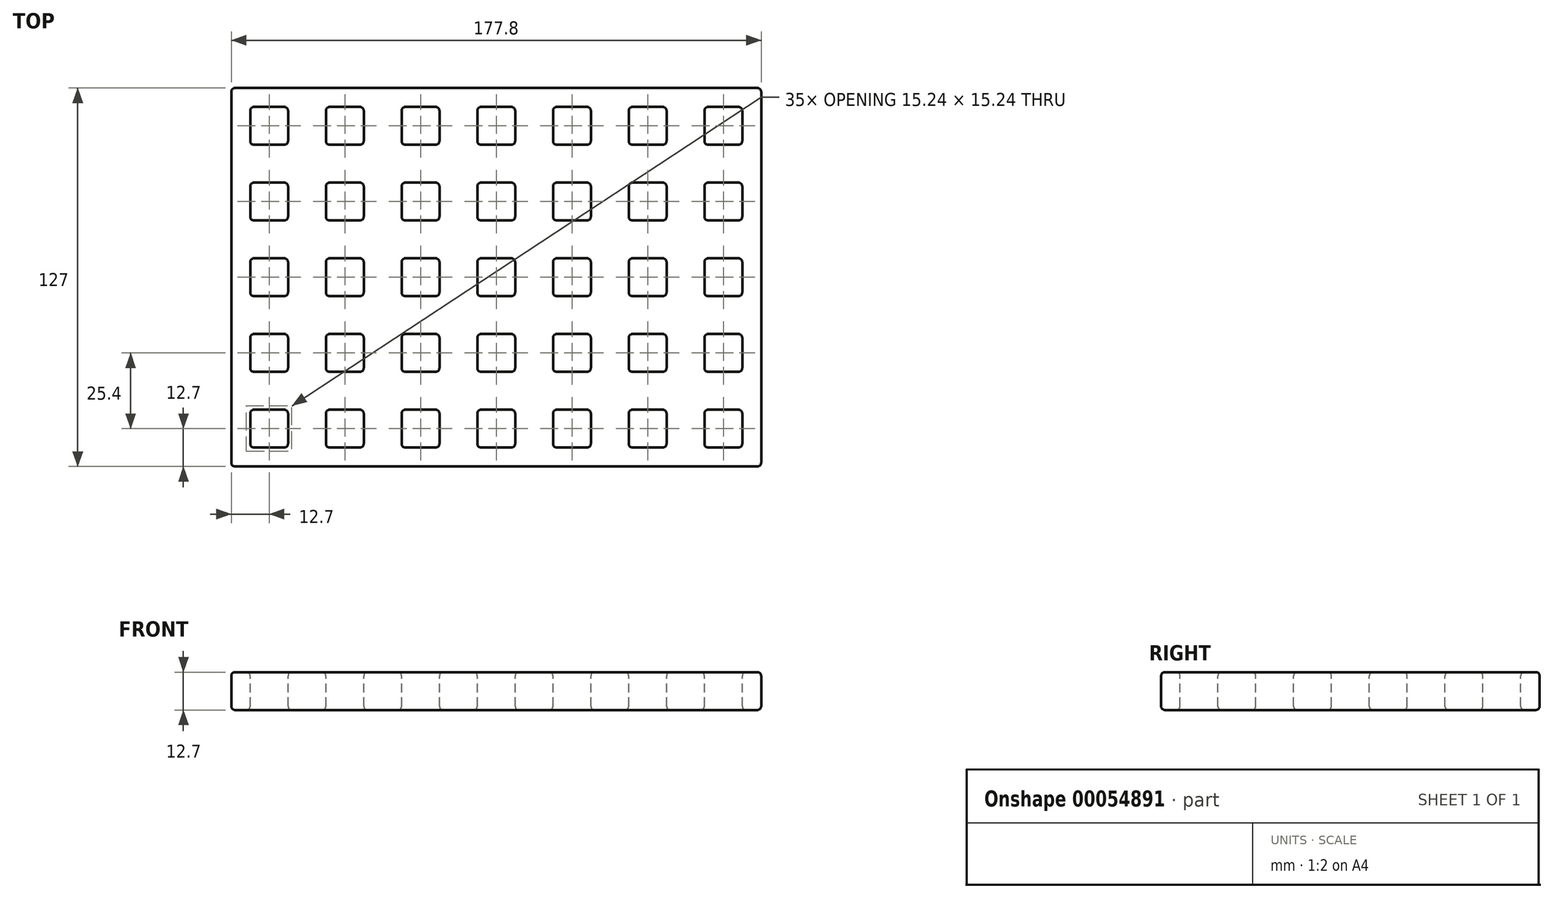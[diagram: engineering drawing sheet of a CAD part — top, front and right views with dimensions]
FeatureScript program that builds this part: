
annotation { "Feature Type Name" : "Feature", "Feature Type Description" : "" }
export const myFeature = defineFeature(function(context is Context, id is Id, definition is map)
    precondition{}
    {
        {
            var Q0;
            Q0=qCreatedBy(makeId("Top.planeOp"),FACE);
            var sketch = newSketch(context, id + "F0", { "sketchPlane" : qUnion([Q0])});
            skLineSegment(sketch, "E0.rect.bottom", {"start": v(88.9, 63.5) * mm, "end": v(-88.9, 63.5) * mm});
            skLineSegment(sketch, "E0.rect.top", {"start": v(88.9, -63.5) * mm, "end": v(-88.9, -63.5) * mm});
            skLineSegment(sketch, "E0.rect.left", {"start": v(88.9, 63.5) * mm, "end": v(88.9, -63.5) * mm});
            skLineSegment(sketch, "E0.rect.right", {"start": v(-88.9, 63.5) * mm, "end": v(-88.9, -63.5) * mm});
            skPoint(sketch, "E0.rect.middle", {"position": v(0, 0) * mm});
            skSolve(sketch);
        }
        {
            var Q0;
            Q0 = qSketchRegion(id + "F0", true);
            extrude(context, id + "F1", {"entities" : qUnion([Q0]), "depth" : 12.7 * mm});
        }
        {
            var Q0;
            Q0=makeQuery(id+"F1.opExtrude","CAP_FACE",FACE,{"disambiguationData":[OSD([sQuery(id+"F0.wireOp",EDGE,"E0.rect.bottom"),sQuery(id+"F0.wireOp",EDGE,"E0.rect.top"),sQuery(id+"F0.wireOp",EDGE,"E0.rect.left"),sQuery(id+"F0.wireOp",EDGE,"E0.rect.right")])],"isStart":false});
            var sketch = newSketch(context, id + "F2", { "sketchPlane" : qUnion([Q0])});
            skLineSegment(sketch, "E1.bottom", {"start": v(-82.55, 57.15) * mm, "end": v(-69.85, 57.15) * mm});
            skLineSegment(sketch, "E1.top", {"start": v(-82.55, 44.45) * mm, "end": v(-69.85, 44.45) * mm});
            skLineSegment(sketch, "E1.left", {"start": v(-82.55, 57.15) * mm, "end": v(-82.55, 44.45) * mm});
            skLineSegment(sketch, "E1.right", {"start": v(-69.85, 57.15) * mm, "end": v(-69.85, 44.45) * mm});
            skLineSegment(sketch, "E2.0.1.0", {"start": v(-82.55, 31.75) * mm, "end": v(-69.85, 31.75) * mm});
            skLineSegment(sketch, "E2.0.1.1", {"start": v(-82.55, 19.05) * mm, "end": v(-69.85, 19.05) * mm});
            skLineSegment(sketch, "E2.0.1.2", {"start": v(-82.55, 31.75) * mm, "end": v(-82.55, 19.05) * mm});
            skLineSegment(sketch, "E2.0.1.3", {"start": v(-69.85, 31.75) * mm, "end": v(-69.85, 19.05) * mm});
            skLineSegment(sketch, "E2.0.2.0", {"start": v(-82.55, 6.35) * mm, "end": v(-69.85, 6.35) * mm});
            skLineSegment(sketch, "E2.0.2.1", {"start": v(-82.55, -6.35) * mm, "end": v(-69.85, -6.35) * mm});
            skLineSegment(sketch, "E2.0.2.2", {"start": v(-82.55, 6.35) * mm, "end": v(-82.55, -6.35) * mm});
            skLineSegment(sketch, "E2.0.2.3", {"start": v(-69.85, 6.35) * mm, "end": v(-69.85, -6.35) * mm});
            skLineSegment(sketch, "E2.0.3.0", {"start": v(-82.55, -19.05) * mm, "end": v(-69.85, -19.05) * mm});
            skLineSegment(sketch, "E2.0.3.1", {"start": v(-82.55, -31.75) * mm, "end": v(-69.85, -31.75) * mm});
            skLineSegment(sketch, "E2.0.3.2", {"start": v(-82.55, -19.05) * mm, "end": v(-82.55, -31.75) * mm});
            skLineSegment(sketch, "E2.0.3.3", {"start": v(-69.85, -19.05) * mm, "end": v(-69.85, -31.75) * mm});
            skLineSegment(sketch, "E2.0.4.0", {"start": v(-82.55, -44.45) * mm, "end": v(-69.85, -44.45) * mm});
            skLineSegment(sketch, "E2.0.4.1", {"start": v(-82.55, -57.15) * mm, "end": v(-69.85, -57.15) * mm});
            skLineSegment(sketch, "E2.0.4.2", {"start": v(-82.55, -44.45) * mm, "end": v(-82.55, -57.15) * mm});
            skLineSegment(sketch, "E2.0.4.3", {"start": v(-69.85, -44.45) * mm, "end": v(-69.85, -57.15) * mm});
            skLineSegment(sketch, "E2.1.0.0", {"start": v(-57.15, 57.15) * mm, "end": v(-44.45, 57.15) * mm});
            skLineSegment(sketch, "E2.1.0.1", {"start": v(-57.15, 44.45) * mm, "end": v(-44.45, 44.45) * mm});
            skLineSegment(sketch, "E2.1.0.2", {"start": v(-57.15, 57.15) * mm, "end": v(-57.15, 44.45) * mm});
            skLineSegment(sketch, "E2.1.0.3", {"start": v(-44.45, 57.15) * mm, "end": v(-44.45, 44.45) * mm});
            skLineSegment(sketch, "E2.1.1.0", {"start": v(-57.15, 31.75) * mm, "end": v(-44.45, 31.75) * mm});
            skLineSegment(sketch, "E2.1.1.1", {"start": v(-57.15, 19.05) * mm, "end": v(-44.45, 19.05) * mm});
            skLineSegment(sketch, "E2.1.1.2", {"start": v(-57.15, 31.75) * mm, "end": v(-57.15, 19.05) * mm});
            skLineSegment(sketch, "E2.1.1.3", {"start": v(-44.45, 31.75) * mm, "end": v(-44.45, 19.05) * mm});
            skLineSegment(sketch, "E2.1.2.0", {"start": v(-57.15, 6.35) * mm, "end": v(-44.45, 6.35) * mm});
            skLineSegment(sketch, "E2.1.2.1", {"start": v(-57.15, -6.35) * mm, "end": v(-44.45, -6.35) * mm});
            skLineSegment(sketch, "E2.1.2.2", {"start": v(-57.15, 6.35) * mm, "end": v(-57.15, -6.35) * mm});
            skLineSegment(sketch, "E2.1.2.3", {"start": v(-44.45, 6.35) * mm, "end": v(-44.45, -6.35) * mm});
            skLineSegment(sketch, "E2.1.3.0", {"start": v(-57.15, -19.05) * mm, "end": v(-44.45, -19.05) * mm});
            skLineSegment(sketch, "E2.1.3.1", {"start": v(-57.15, -31.75) * mm, "end": v(-44.45, -31.75) * mm});
            skLineSegment(sketch, "E2.1.3.2", {"start": v(-57.15, -19.05) * mm, "end": v(-57.15, -31.75) * mm});
            skLineSegment(sketch, "E2.1.3.3", {"start": v(-44.45, -19.05) * mm, "end": v(-44.45, -31.75) * mm});
            skLineSegment(sketch, "E2.1.4.0", {"start": v(-57.15, -44.45) * mm, "end": v(-44.45, -44.45) * mm});
            skLineSegment(sketch, "E2.1.4.1", {"start": v(-57.15, -57.15) * mm, "end": v(-44.45, -57.15) * mm});
            skLineSegment(sketch, "E2.1.4.2", {"start": v(-57.15, -44.45) * mm, "end": v(-57.15, -57.15) * mm});
            skLineSegment(sketch, "E2.1.4.3", {"start": v(-44.45, -44.45) * mm, "end": v(-44.45, -57.15) * mm});
            skLineSegment(sketch, "E2.2.0.0", {"start": v(-31.75, 57.15) * mm, "end": v(-19.05, 57.15) * mm});
            skLineSegment(sketch, "E2.2.0.1", {"start": v(-31.75, 44.45) * mm, "end": v(-19.05, 44.45) * mm});
            skLineSegment(sketch, "E2.2.0.2", {"start": v(-31.75, 57.15) * mm, "end": v(-31.75, 44.45) * mm});
            skLineSegment(sketch, "E2.2.0.3", {"start": v(-19.05, 57.15) * mm, "end": v(-19.05, 44.45) * mm});
            skLineSegment(sketch, "E2.2.1.0", {"start": v(-31.75, 31.75) * mm, "end": v(-19.05, 31.75) * mm});
            skLineSegment(sketch, "E2.2.1.1", {"start": v(-31.75, 19.05) * mm, "end": v(-19.05, 19.05) * mm});
            skLineSegment(sketch, "E2.2.1.2", {"start": v(-31.75, 31.75) * mm, "end": v(-31.75, 19.05) * mm});
            skLineSegment(sketch, "E2.2.1.3", {"start": v(-19.05, 31.75) * mm, "end": v(-19.05, 19.05) * mm});
            skLineSegment(sketch, "E2.2.2.0", {"start": v(-31.75, 6.35) * mm, "end": v(-19.05, 6.35) * mm});
            skLineSegment(sketch, "E2.2.2.1", {"start": v(-31.75, -6.35) * mm, "end": v(-19.05, -6.35) * mm});
            skLineSegment(sketch, "E2.2.2.2", {"start": v(-31.75, 6.35) * mm, "end": v(-31.75, -6.35) * mm});
            skLineSegment(sketch, "E2.2.2.3", {"start": v(-19.05, 6.35) * mm, "end": v(-19.05, -6.35) * mm});
            skLineSegment(sketch, "E2.2.3.0", {"start": v(-31.75, -19.05) * mm, "end": v(-19.05, -19.05) * mm});
            skLineSegment(sketch, "E2.2.3.1", {"start": v(-31.75, -31.75) * mm, "end": v(-19.05, -31.75) * mm});
            skLineSegment(sketch, "E2.2.3.2", {"start": v(-31.75, -19.05) * mm, "end": v(-31.75, -31.75) * mm});
            skLineSegment(sketch, "E2.2.3.3", {"start": v(-19.05, -19.05) * mm, "end": v(-19.05, -31.75) * mm});
            skLineSegment(sketch, "E2.2.4.0", {"start": v(-31.75, -44.45) * mm, "end": v(-19.05, -44.45) * mm});
            skLineSegment(sketch, "E2.2.4.1", {"start": v(-31.75, -57.15) * mm, "end": v(-19.05, -57.15) * mm});
            skLineSegment(sketch, "E2.2.4.2", {"start": v(-31.75, -44.45) * mm, "end": v(-31.75, -57.15) * mm});
            skLineSegment(sketch, "E2.2.4.3", {"start": v(-19.05, -44.45) * mm, "end": v(-19.05, -57.15) * mm});
            skLineSegment(sketch, "E2.3.0.0", {"start": v(-6.35, 57.15) * mm, "end": v(6.35, 57.15) * mm});
            skLineSegment(sketch, "E2.3.0.1", {"start": v(-6.35, 44.45) * mm, "end": v(6.35, 44.45) * mm});
            skLineSegment(sketch, "E2.3.0.2", {"start": v(-6.35, 57.15) * mm, "end": v(-6.35, 44.45) * mm});
            skLineSegment(sketch, "E2.3.0.3", {"start": v(6.35, 57.15) * mm, "end": v(6.35, 44.45) * mm});
            skLineSegment(sketch, "E2.3.1.0", {"start": v(-6.35, 31.75) * mm, "end": v(6.35, 31.75) * mm});
            skLineSegment(sketch, "E2.3.1.1", {"start": v(-6.35, 19.05) * mm, "end": v(6.35, 19.05) * mm});
            skLineSegment(sketch, "E2.3.1.2", {"start": v(-6.35, 31.75) * mm, "end": v(-6.35, 19.05) * mm});
            skLineSegment(sketch, "E2.3.1.3", {"start": v(6.35, 31.75) * mm, "end": v(6.35, 19.05) * mm});
            skLineSegment(sketch, "E2.3.2.0", {"start": v(-6.35, 6.35) * mm, "end": v(6.35, 6.35) * mm});
            skLineSegment(sketch, "E2.3.2.1", {"start": v(-6.35, -6.35) * mm, "end": v(6.35, -6.35) * mm});
            skLineSegment(sketch, "E2.3.2.2", {"start": v(-6.35, 6.35) * mm, "end": v(-6.35, -6.35) * mm});
            skLineSegment(sketch, "E2.3.2.3", {"start": v(6.35, 6.35) * mm, "end": v(6.35, -6.35) * mm});
            skLineSegment(sketch, "E2.3.3.0", {"start": v(-6.35, -19.05) * mm, "end": v(6.35, -19.05) * mm});
            skLineSegment(sketch, "E2.3.3.1", {"start": v(-6.35, -31.75) * mm, "end": v(6.35, -31.75) * mm});
            skLineSegment(sketch, "E2.3.3.2", {"start": v(-6.35, -19.05) * mm, "end": v(-6.35, -31.75) * mm});
            skLineSegment(sketch, "E2.3.3.3", {"start": v(6.35, -19.05) * mm, "end": v(6.35, -31.75) * mm});
            skLineSegment(sketch, "E2.3.4.0", {"start": v(-6.35, -44.45) * mm, "end": v(6.35, -44.45) * mm});
            skLineSegment(sketch, "E2.3.4.1", {"start": v(-6.35, -57.15) * mm, "end": v(6.35, -57.15) * mm});
            skLineSegment(sketch, "E2.3.4.2", {"start": v(-6.35, -44.45) * mm, "end": v(-6.35, -57.15) * mm});
            skLineSegment(sketch, "E2.3.4.3", {"start": v(6.35, -44.45) * mm, "end": v(6.35, -57.15) * mm});
            skLineSegment(sketch, "E2.4.0.0", {"start": v(19.05, 57.15) * mm, "end": v(31.75, 57.15) * mm});
            skLineSegment(sketch, "E2.4.0.1", {"start": v(19.05, 44.45) * mm, "end": v(31.75, 44.45) * mm});
            skLineSegment(sketch, "E2.4.0.2", {"start": v(19.05, 57.15) * mm, "end": v(19.05, 44.45) * mm});
            skLineSegment(sketch, "E2.4.0.3", {"start": v(31.75, 57.15) * mm, "end": v(31.75, 44.45) * mm});
            skLineSegment(sketch, "E2.4.1.0", {"start": v(19.05, 31.75) * mm, "end": v(31.75, 31.75) * mm});
            skLineSegment(sketch, "E2.4.1.1", {"start": v(19.05, 19.05) * mm, "end": v(31.75, 19.05) * mm});
            skLineSegment(sketch, "E2.4.1.2", {"start": v(19.05, 31.75) * mm, "end": v(19.05, 19.05) * mm});
            skLineSegment(sketch, "E2.4.1.3", {"start": v(31.75, 31.75) * mm, "end": v(31.75, 19.05) * mm});
            skLineSegment(sketch, "E2.4.2.0", {"start": v(19.05, 6.35) * mm, "end": v(31.75, 6.35) * mm});
            skLineSegment(sketch, "E2.4.2.1", {"start": v(19.05, -6.35) * mm, "end": v(31.75, -6.35) * mm});
            skLineSegment(sketch, "E2.4.2.2", {"start": v(19.05, 6.35) * mm, "end": v(19.05, -6.35) * mm});
            skLineSegment(sketch, "E2.4.2.3", {"start": v(31.75, 6.35) * mm, "end": v(31.75, -6.35) * mm});
            skLineSegment(sketch, "E2.4.3.0", {"start": v(19.05, -19.05) * mm, "end": v(31.75, -19.05) * mm});
            skLineSegment(sketch, "E2.4.3.1", {"start": v(19.05, -31.75) * mm, "end": v(31.75, -31.75) * mm});
            skLineSegment(sketch, "E2.4.3.2", {"start": v(19.05, -19.05) * mm, "end": v(19.05, -31.75) * mm});
            skLineSegment(sketch, "E2.4.3.3", {"start": v(31.75, -19.05) * mm, "end": v(31.75, -31.75) * mm});
            skLineSegment(sketch, "E2.4.4.0", {"start": v(19.05, -44.45) * mm, "end": v(31.75, -44.45) * mm});
            skLineSegment(sketch, "E2.4.4.1", {"start": v(19.05, -57.15) * mm, "end": v(31.75, -57.15) * mm});
            skLineSegment(sketch, "E2.4.4.2", {"start": v(19.05, -44.45) * mm, "end": v(19.05, -57.15) * mm});
            skLineSegment(sketch, "E2.4.4.3", {"start": v(31.75, -44.45) * mm, "end": v(31.75, -57.15) * mm});
            skLineSegment(sketch, "E2.5.0.0", {"start": v(44.45, 57.15) * mm, "end": v(57.15, 57.15) * mm});
            skLineSegment(sketch, "E2.5.0.1", {"start": v(44.45, 44.45) * mm, "end": v(57.15, 44.45) * mm});
            skLineSegment(sketch, "E2.5.0.2", {"start": v(44.45, 57.15) * mm, "end": v(44.45, 44.45) * mm});
            skLineSegment(sketch, "E2.5.0.3", {"start": v(57.15, 57.15) * mm, "end": v(57.15, 44.45) * mm});
            skLineSegment(sketch, "E2.5.1.0", {"start": v(44.45, 31.75) * mm, "end": v(57.15, 31.75) * mm});
            skLineSegment(sketch, "E2.5.1.1", {"start": v(44.45, 19.05) * mm, "end": v(57.15, 19.05) * mm});
            skLineSegment(sketch, "E2.5.1.2", {"start": v(44.45, 31.75) * mm, "end": v(44.45, 19.05) * mm});
            skLineSegment(sketch, "E2.5.1.3", {"start": v(57.15, 31.75) * mm, "end": v(57.15, 19.05) * mm});
            skLineSegment(sketch, "E2.5.2.0", {"start": v(44.45, 6.35) * mm, "end": v(57.15, 6.35) * mm});
            skLineSegment(sketch, "E2.5.2.1", {"start": v(44.45, -6.35) * mm, "end": v(57.15, -6.35) * mm});
            skLineSegment(sketch, "E2.5.2.2", {"start": v(44.45, 6.35) * mm, "end": v(44.45, -6.35) * mm});
            skLineSegment(sketch, "E2.5.2.3", {"start": v(57.15, 6.35) * mm, "end": v(57.15, -6.35) * mm});
            skLineSegment(sketch, "E2.5.3.0", {"start": v(44.45, -19.05) * mm, "end": v(57.15, -19.05) * mm});
            skLineSegment(sketch, "E2.5.3.1", {"start": v(44.45, -31.75) * mm, "end": v(57.15, -31.75) * mm});
            skLineSegment(sketch, "E2.5.3.2", {"start": v(44.45, -19.05) * mm, "end": v(44.45, -31.75) * mm});
            skLineSegment(sketch, "E2.5.3.3", {"start": v(57.15, -19.05) * mm, "end": v(57.15, -31.75) * mm});
            skLineSegment(sketch, "E2.5.4.0", {"start": v(44.45, -44.45) * mm, "end": v(57.15, -44.45) * mm});
            skLineSegment(sketch, "E2.5.4.1", {"start": v(44.45, -57.15) * mm, "end": v(57.15, -57.15) * mm});
            skLineSegment(sketch, "E2.5.4.2", {"start": v(44.45, -44.45) * mm, "end": v(44.45, -57.15) * mm});
            skLineSegment(sketch, "E2.5.4.3", {"start": v(57.15, -44.45) * mm, "end": v(57.15, -57.15) * mm});
            skLineSegment(sketch, "E2.6.0.0", {"start": v(69.85, 57.15) * mm, "end": v(82.55, 57.15) * mm});
            skLineSegment(sketch, "E2.6.0.1", {"start": v(69.85, 44.45) * mm, "end": v(82.55, 44.45) * mm});
            skLineSegment(sketch, "E2.6.0.2", {"start": v(69.85, 57.15) * mm, "end": v(69.85, 44.45) * mm});
            skLineSegment(sketch, "E2.6.0.3", {"start": v(82.55, 57.15) * mm, "end": v(82.55, 44.45) * mm});
            skLineSegment(sketch, "E2.6.1.0", {"start": v(69.85, 31.75) * mm, "end": v(82.55, 31.75) * mm});
            skLineSegment(sketch, "E2.6.1.1", {"start": v(69.85, 19.05) * mm, "end": v(82.55, 19.05) * mm});
            skLineSegment(sketch, "E2.6.1.2", {"start": v(69.85, 31.75) * mm, "end": v(69.85, 19.05) * mm});
            skLineSegment(sketch, "E2.6.1.3", {"start": v(82.55, 31.75) * mm, "end": v(82.55, 19.05) * mm});
            skLineSegment(sketch, "E2.6.2.0", {"start": v(69.85, 6.35) * mm, "end": v(82.55, 6.35) * mm});
            skLineSegment(sketch, "E2.6.2.1", {"start": v(69.85, -6.35) * mm, "end": v(82.55, -6.35) * mm});
            skLineSegment(sketch, "E2.6.2.2", {"start": v(69.85, 6.35) * mm, "end": v(69.85, -6.35) * mm});
            skLineSegment(sketch, "E2.6.2.3", {"start": v(82.55, 6.35) * mm, "end": v(82.55, -6.35) * mm});
            skLineSegment(sketch, "E2.6.3.0", {"start": v(69.85, -19.05) * mm, "end": v(82.55, -19.05) * mm});
            skLineSegment(sketch, "E2.6.3.1", {"start": v(69.85, -31.75) * mm, "end": v(82.55, -31.75) * mm});
            skLineSegment(sketch, "E2.6.3.2", {"start": v(69.85, -19.05) * mm, "end": v(69.85, -31.75) * mm});
            skLineSegment(sketch, "E2.6.3.3", {"start": v(82.55, -19.05) * mm, "end": v(82.55, -31.75) * mm});
            skLineSegment(sketch, "E2.6.4.0", {"start": v(69.85, -44.45) * mm, "end": v(82.55, -44.45) * mm});
            skLineSegment(sketch, "E2.6.4.1", {"start": v(69.85, -57.15) * mm, "end": v(82.55, -57.15) * mm});
            skLineSegment(sketch, "E2.6.4.2", {"start": v(69.85, -44.45) * mm, "end": v(69.85, -57.15) * mm});
            skLineSegment(sketch, "E2.6.4.3", {"start": v(82.55, -44.45) * mm, "end": v(82.55, -57.15) * mm});
            skLineSegment(sketch, "E2.direction1", {"start": v(-82.55, 57.15) * mm, "end": v(-57.15, 57.15) * mm, "construction": true});
            skLineSegment(sketch, "E2.direction2", {"start": v(-82.55, 57.15) * mm, "end": v(-82.55, 31.75) * mm, "construction": true});
            skSolve(sketch);
        }
        {
            var Q0;
            Q0 = qSketchRegion(id + "F2", true);
            extrude(context, id + "F3", {"entities" : qUnion([Q0]), "operationType" : NewBodyOperationType.REMOVE, "oppositeDirection" : true, "depth" : 25.4 * mm});
        }
        {
            var Q0;
            Q0=makeQuery(id+"F3.boolean.opBoolean","COPY",EDGE,{"derivedFrom":makeQuery(id+"F3.opExtrude","CAP_EDGE",EDGE,{"disambiguationData":[OSD([sQuery(id+"F2.wireOp",EDGE,"E2.5.4.3")])],"isStart":true})});
            var Q1;
            Q1=makeQuery(id+"F3.boolean.opBoolean","COPY",EDGE,{"derivedFrom":makeQuery(id+"F3.opExtrude","CAP_EDGE",EDGE,{"disambiguationData":[OSD([sQuery(id+"F2.wireOp",EDGE,"E2.5.0.3")])],"isStart":true})});
            var Q2;
            Q2=makeQuery(id+"F3.boolean.opBoolean","COPY",FACE,{"derivedFrom":makeQuery(id+"F3.opExtrude","SWEPT_FACE",FACE,{"disambiguationData":[OSD([sQuery(id+"F2.wireOp",EDGE,"E2.5.3.2")])]})});
            var Q3;
            Q3=makeQuery(id+"F3.boolean.opBoolean","COPY",FACE,{"derivedFrom":makeQuery(id+"F3.opExtrude","SWEPT_FACE",FACE,{"disambiguationData":[OSD([sQuery(id+"F2.wireOp",EDGE,"E2.0.4.2")])]})});
            var Q4;
            Q4=makeQuery(id+"F3.boolean.opBoolean","COPY",FACE,{"derivedFrom":makeQuery(id+"F3.opExtrude","SWEPT_FACE",FACE,{"disambiguationData":[OSD([sQuery(id+"F2.wireOp",EDGE,"E2.6.4.0")])]})});
            var Q5;
            Q5=makeQuery(id+"F3.boolean.opBoolean","COPY",FACE,{"derivedFrom":makeQuery(id+"F3.opExtrude","SWEPT_FACE",FACE,{"disambiguationData":[OSD([sQuery(id+"F2.wireOp",EDGE,"E2.6.0.0")])]})});
            var Q6;
            Q6=makeQuery(id+"F3.boolean.opBoolean","COPY",FACE,{"derivedFrom":makeQuery(id+"F3.opExtrude","SWEPT_FACE",FACE,{"disambiguationData":[OSD([sQuery(id+"F2.wireOp",EDGE,"E2.3.3.0")])]})});
            var Q7;
            Q7=makeQuery(id+"F3.boolean.opBoolean","COPY",FACE,{"derivedFrom":makeQuery(id+"F3.opExtrude","SWEPT_FACE",FACE,{"disambiguationData":[OSD([sQuery(id+"F2.wireOp",EDGE,"E2.2.4.0")])]})});
            var Q8;
            Q8=makeQuery(id+"F3.boolean.opBoolean","COPY",EDGE,{"derivedFrom":makeQuery(id+"F3.opExtrude","CAP_EDGE",EDGE,{"disambiguationData":[OSD([sQuery(id+"F2.wireOp",EDGE,"E2.0.3.1")])],"isStart":true})});
            var Q9;
            Q9=makeQuery(id+"F3.boolean.opBoolean","COPY",EDGE,{"derivedFrom":makeQuery(id+"F3.opExtrude","CAP_EDGE",EDGE,{"disambiguationData":[OSD([sQuery(id+"F2.wireOp",EDGE,"E2.0.2.2")])],"isStart":true})});
            var Q10;
            Q10=makeQuery(id+"F3.boolean.opBoolean","COPY",EDGE,{"derivedFrom":makeQuery(id+"F3.opExtrude","CAP_EDGE",EDGE,{"disambiguationData":[OSD([sQuery(id+"F2.wireOp",EDGE,"E2.3.3.2")])],"isStart":true})});
            var Q11;
            Q11=makeQuery(id+"F3.boolean.opBoolean","COPY",EDGE,{"derivedFrom":makeQuery(id+"F3.opExtrude","CAP_EDGE",EDGE,{"disambiguationData":[OSD([sQuery(id+"F2.wireOp",EDGE,"E2.2.4.2")])],"isStart":true})});
            var Q12;
            Q12=makeQuery(id+"F3.boolean.opBoolean","COPY",EDGE,{"derivedFrom":makeQuery(id+"F3.opExtrude","CAP_EDGE",EDGE,{"disambiguationData":[OSD([sQuery(id+"F2.wireOp",EDGE,"E2.6.4.2")])],"isStart":true})});
            var Q13;
            Q13=makeQuery(id+"F3.boolean.opBoolean","COPY",EDGE,{"derivedFrom":makeQuery(id+"F3.opExtrude","CAP_EDGE",EDGE,{"disambiguationData":[OSD([sQuery(id+"F2.wireOp",EDGE,"E2.6.0.2")])],"isStart":true})});
            var Q14;
            Q14=makeQuery(id+"F3.boolean.opBoolean","COPY",FACE,{"derivedFrom":makeQuery(id+"F3.opExtrude","SWEPT_FACE",FACE,{"disambiguationData":[OSD([sQuery(id+"F2.wireOp",EDGE,"E2.1.4.2")])]})});
            var Q15;
            Q15=makeQuery(id+"F3.boolean.opBoolean","COPY",FACE,{"derivedFrom":makeQuery(id+"F3.opExtrude","SWEPT_FACE",FACE,{"disambiguationData":[OSD([sQuery(id+"F2.wireOp",EDGE,"E2.2.3.2")])]})});
            var Q16;
            Q16=makeQuery(id+"F3.boolean.opBoolean","COPY",FACE,{"derivedFrom":makeQuery(id+"F3.opExtrude","SWEPT_FACE",FACE,{"disambiguationData":[OSD([sQuery(id+"F2.wireOp",EDGE,"E2.6.3.2")])]})});
            var Q17;
            Q17=makeQuery(id+"F3.boolean.opBoolean","COPY",FACE,{"derivedFrom":makeQuery(id+"F3.opExtrude","SWEPT_FACE",FACE,{"disambiguationData":[OSD([sQuery(id+"F2.wireOp",EDGE,"E2.5.4.2")])]})});
            var Q18;
            Q18=makeQuery(id+"F3.boolean.opBoolean","COPY",EDGE,{"derivedFrom":makeQuery(id+"F3.opExtrude","CAP_EDGE",EDGE,{"disambiguationData":[OSD([sQuery(id+"F2.wireOp",EDGE,"E2.3.4.1")])],"isStart":true})});
            var Q19;
            Q19=makeQuery(id+"F3.boolean.opBoolean","COPY",EDGE,{"derivedFrom":makeQuery(id+"F3.opExtrude","CAP_EDGE",EDGE,{"disambiguationData":[OSD([sQuery(id+"F2.wireOp",EDGE,"E2.1.2.1")])],"isStart":true})});
            var Q20;
            Q20=makeQuery(id+"F3.boolean.opBoolean","COPY",EDGE,{"derivedFrom":makeQuery(id+"F3.opExtrude","CAP_EDGE",EDGE,{"disambiguationData":[OSD([sQuery(id+"F2.wireOp",EDGE,"E2.6.1.1")])],"isStart":true})});
            var Q21;
            Q21=makeQuery(id+"F3.boolean.opBoolean","COPY",EDGE,{"derivedFrom":makeQuery(id+"F3.opExtrude","CAP_EDGE",EDGE,{"disambiguationData":[OSD([sQuery(id+"F2.wireOp",EDGE,"E2.5.2.1")])],"isStart":true})});
            var Q22;
            Q22=makeQuery(id+"F3.boolean.opBoolean","COPY",FACE,{"derivedFrom":makeQuery(id+"F3.opExtrude","SWEPT_FACE",FACE,{"disambiguationData":[OSD([sQuery(id+"F2.wireOp",EDGE,"E2.2.4.1")])]})});
            var Q23;
            Q23=makeQuery(id+"F3.boolean.opBoolean","COPY",FACE,{"derivedFrom":makeQuery(id+"F3.opExtrude","SWEPT_FACE",FACE,{"disambiguationData":[OSD([sQuery(id+"F2.wireOp",EDGE,"E2.6.4.1")])]})});
            var Q24;
            Q24=makeQuery(id+"F3.boolean.opBoolean","COPY",FACE,{"derivedFrom":makeQuery(id+"F3.opExtrude","SWEPT_FACE",FACE,{"disambiguationData":[OSD([sQuery(id+"F2.wireOp",EDGE,"E2.6.0.1")])]})});
            var Q25;
            Q25=makeQuery(id+"F3.boolean.opBoolean","COPY",EDGE,{"derivedFrom":makeQuery(id+"F3.opExtrude","CAP_EDGE",EDGE,{"disambiguationData":[OSD([sQuery(id+"F2.wireOp",EDGE,"E2.0.3.2")])],"isStart":true})});
            var Q26;
            Q26=makeQuery(id+"F3.boolean.opBoolean","COPY",EDGE,{"derivedFrom":makeQuery(id+"F3.opExtrude","CAP_EDGE",EDGE,{"disambiguationData":[OSD([sQuery(id+"F2.wireOp",EDGE,"E2.3.4.2")])],"isStart":true})});
            var Q27;
            Q27=makeQuery(id+"F3.boolean.opBoolean","COPY",EDGE,{"derivedFrom":makeQuery(id+"F3.opExtrude","CAP_EDGE",EDGE,{"disambiguationData":[OSD([sQuery(id+"F2.wireOp",EDGE,"E2.6.1.2")])],"isStart":true})});
            var Q28;
            Q28=makeQuery(id+"F3.boolean.opBoolean","COPY",FACE,{"derivedFrom":makeQuery(id+"F3.opExtrude","SWEPT_FACE",FACE,{"disambiguationData":[OSD([sQuery(id+"F2.wireOp",EDGE,"E2.3.3.2")])]})});
            var Q29;
            Q29=makeQuery(id+"F3.boolean.opBoolean","COPY",FACE,{"derivedFrom":makeQuery(id+"F3.opExtrude","SWEPT_FACE",FACE,{"disambiguationData":[OSD([sQuery(id+"F2.wireOp",EDGE,"E2.2.4.2")])]})});
            var Q30;
            Q30=makeQuery(id+"F3.boolean.opBoolean","COPY",FACE,{"derivedFrom":makeQuery(id+"F3.opExtrude","SWEPT_FACE",FACE,{"disambiguationData":[OSD([sQuery(id+"F2.wireOp",EDGE,"E2.6.4.2")])]})});
            var Q31;
            Q31=makeQuery(id+"F3.boolean.opBoolean","COPY",FACE,{"derivedFrom":makeQuery(id+"F3.opExtrude","SWEPT_FACE",FACE,{"disambiguationData":[OSD([sQuery(id+"F2.wireOp",EDGE,"E2.6.0.2")])]})});
            var Q32;
            Q32=makeQuery(id+"F3.boolean.opBoolean","COPY",FACE,{"derivedFrom":makeQuery(id+"F3.opExtrude","SWEPT_FACE",FACE,{"disambiguationData":[OSD([sQuery(id+"F2.wireOp",EDGE,"E2.2.4.3")])]})});
            var Q33;
            Q33=makeQuery(id+"F3.boolean.opBoolean","COPY",FACE,{"derivedFrom":makeQuery(id+"F3.opExtrude","SWEPT_FACE",FACE,{"disambiguationData":[OSD([sQuery(id+"F2.wireOp",EDGE,"E2.6.0.3")])]})});
            var Q34;
            Q34=makeQuery(id+"F3.boolean.opBoolean","COPY",FACE,{"derivedFrom":makeQuery(id+"F3.opExtrude","SWEPT_FACE",FACE,{"disambiguationData":[OSD([sQuery(id+"F2.wireOp",EDGE,"E2.6.4.3")])]})});
            var Q35;
            Q35=makeQuery(id+"F3.boolean.opBoolean","COPY",EDGE,{"derivedFrom":makeQuery(id+"F3.opExtrude","CAP_EDGE",EDGE,{"disambiguationData":[OSD([sQuery(id+"F2.wireOp",EDGE,"E2.0.4.0")])],"isStart":true})});
            var Q36;
            Q36=makeQuery(id+"F3.boolean.opBoolean","COPY",EDGE,{"derivedFrom":makeQuery(id+"F3.opExtrude","CAP_EDGE",EDGE,{"disambiguationData":[OSD([sQuery(id+"F2.wireOp",EDGE,"E2.4.4.0")])],"isStart":true})});
            var Q37;
            Q37=makeQuery(id+"F3.boolean.opBoolean","COPY",FACE,{"derivedFrom":makeQuery(id+"F3.opExtrude","SWEPT_FACE",FACE,{"disambiguationData":[OSD([sQuery(id+"F2.wireOp",EDGE,"E2.4.3.0")])]})});
            var Q38;
            Q38=makeQuery(id+"F3.boolean.opBoolean","COPY",FACE,{"derivedFrom":makeQuery(id+"F3.opExtrude","SWEPT_FACE",FACE,{"disambiguationData":[OSD([sQuery(id+"F2.wireOp",EDGE,"E2.3.4.0")])]})});
            var Q39;
            Q39=makeQuery(id+"F1.opExtrude","CAP_FACE",FACE,{"disambiguationData":[OSD([sQuery(id+"F0.wireOp",EDGE,"E0.rect.bottom"),sQuery(id+"F0.wireOp",EDGE,"E0.rect.top"),sQuery(id+"F0.wireOp",EDGE,"E0.rect.left"),sQuery(id+"F0.wireOp",EDGE,"E0.rect.right")])],"isStart":true});
            var Q40;
            Q40=makeQuery(id+"F3.boolean.opBoolean","COPY",FACE,{"derivedFrom":makeQuery(id+"F3.opExtrude","SWEPT_FACE",FACE,{"disambiguationData":[OSD([sQuery(id+"F2.wireOp",EDGE,"E2.6.1.0")])]})});
            var Q41;
            Q41=makeQuery(id+"F3.boolean.opBoolean","COPY",FACE,{"derivedFrom":makeQuery(id+"F3.opExtrude","SWEPT_FACE",FACE,{"disambiguationData":[OSD([sQuery(id+"F2.wireOp",EDGE,"E2.3.4.3")])]})});
            var Q42;
            Q42=makeQuery(id+"F3.boolean.opBoolean","COPY",FACE,{"derivedFrom":makeQuery(id+"F3.opExtrude","SWEPT_FACE",FACE,{"disambiguationData":[OSD([sQuery(id+"F2.wireOp",EDGE,"E2.6.1.3")])]})});
            var Q43;
            Q43=makeQuery(id+"F3.boolean.opBoolean","COPY",FACE,{"derivedFrom":makeQuery(id+"F3.opExtrude","SWEPT_FACE",FACE,{"disambiguationData":[OSD([sQuery(id+"F2.wireOp",EDGE,"E2.4.3.3")])]})});
            var Q44;
            Q44=makeQuery(id+"F3.boolean.opBoolean","COPY",EDGE,{"derivedFrom":makeQuery(id+"F3.opExtrude","CAP_EDGE",EDGE,{"disambiguationData":[OSD([sQuery(id+"F2.wireOp",EDGE,"E2.6.2.1")])],"isStart":true})});
            var Q45;
            Q45=makeQuery(id+"F3.boolean.opBoolean","COPY",EDGE,{"derivedFrom":makeQuery(id+"F3.opExtrude","CAP_EDGE",EDGE,{"disambiguationData":[OSD([sQuery(id+"F2.wireOp",EDGE,"E2.5.3.1")])],"isStart":true})});
            var Q46;
            Q46=makeQuery(id+"F3.boolean.opBoolean","COPY",FACE,{"derivedFrom":makeQuery(id+"F3.opExtrude","SWEPT_FACE",FACE,{"disambiguationData":[OSD([sQuery(id+"F2.wireOp",EDGE,"E2.1.2.1")])]})});
            var Q47;
            Q47=makeQuery(id+"F3.boolean.opBoolean","COPY",FACE,{"derivedFrom":makeQuery(id+"F3.opExtrude","SWEPT_FACE",FACE,{"disambiguationData":[OSD([sQuery(id+"F2.wireOp",EDGE,"E2.6.1.1")])]})});
            var Q48;
            Q48=makeQuery(id+"F3.boolean.opBoolean","COPY",FACE,{"derivedFrom":makeQuery(id+"F3.opExtrude","SWEPT_FACE",FACE,{"disambiguationData":[OSD([sQuery(id+"F2.wireOp",EDGE,"E2.5.0.3")])]})});
            var Q49;
            Q49=makeQuery(id+"F1.opExtrude","CAP_FACE",FACE,{"disambiguationData":[OSD([sQuery(id+"F0.wireOp",EDGE,"E0.rect.bottom"),sQuery(id+"F0.wireOp",EDGE,"E0.rect.top"),sQuery(id+"F0.wireOp",EDGE,"E0.rect.left"),sQuery(id+"F0.wireOp",EDGE,"E0.rect.right")])],"isStart":false});
            var Q50;
            Q50=makeQuery(id+"F3.boolean.opBoolean","COPY",EDGE,{"derivedFrom":makeQuery(id+"F3.opExtrude","CAP_EDGE",EDGE,{"disambiguationData":[OSD([sQuery(id+"F2.wireOp",EDGE,"E2.1.3.1")])],"isStart":true})});
            var Q51;
            Q51=makeQuery(id+"F3.boolean.opBoolean","COPY",EDGE,{"derivedFrom":makeQuery(id+"F3.opExtrude","CAP_EDGE",EDGE,{"disambiguationData":[OSD([sQuery(id+"F2.wireOp",EDGE,"E2.0.4.1")])],"isStart":true})});
            var Q52;
            Q52=makeQuery(id+"F3.boolean.opBoolean","COPY",EDGE,{"derivedFrom":makeQuery(id+"F3.opExtrude","CAP_EDGE",EDGE,{"disambiguationData":[OSD([sQuery(id+"F2.wireOp",EDGE,"E2.4.4.1")])],"isStart":true})});
            var Q53;
            Q53=makeQuery(id+"F3.boolean.opBoolean","COPY",EDGE,{"derivedFrom":makeQuery(id+"F3.opExtrude","CAP_EDGE",EDGE,{"disambiguationData":[OSD([sQuery(id+"F2.wireOp",EDGE,"E2.2.2.1")])],"isStart":true})});
            var Q54;
            Q54=makeQuery(id+"F3.boolean.opBoolean","COPY",FACE,{"derivedFrom":makeQuery(id+"F3.opExtrude","SWEPT_FACE",FACE,{"disambiguationData":[OSD([sQuery(id+"F2.wireOp",EDGE,"E2.6.1.2")])]})});
            var Q55;
            Q55=makeQuery(id+"F3.boolean.opBoolean","COPY",FACE,{"derivedFrom":makeQuery(id+"F3.opExtrude","SWEPT_FACE",FACE,{"disambiguationData":[OSD([sQuery(id+"F2.wireOp",EDGE,"E2.2.3.3")])]})});
            var Q56;
            Q56=makeQuery(id+"F3.boolean.opBoolean","COPY",FACE,{"derivedFrom":makeQuery(id+"F3.opExtrude","SWEPT_FACE",FACE,{"disambiguationData":[OSD([sQuery(id+"F2.wireOp",EDGE,"E2.6.3.3")])]})});
            var Q57;
            Q57=makeQuery(id+"F3.boolean.opBoolean","COPY",FACE,{"derivedFrom":makeQuery(id+"F3.opExtrude","SWEPT_FACE",FACE,{"disambiguationData":[OSD([sQuery(id+"F2.wireOp",EDGE,"E2.5.4.3")])]})});
            var Q58;
            Q58=makeQuery(id+"F3.boolean.opBoolean","COPY",FACE,{"derivedFrom":makeQuery(id+"F3.opExtrude","SWEPT_FACE",FACE,{"disambiguationData":[OSD([sQuery(id+"F2.wireOp",EDGE,"E2.3.4.2")])]})});
            var Q59;
            Q59=makeQuery(id+"F3.boolean.opBoolean","COPY",EDGE,{"derivedFrom":makeQuery(id+"F3.opExtrude","CAP_EDGE",EDGE,{"disambiguationData":[OSD([sQuery(id+"F2.wireOp",EDGE,"E2.2.4.3")])],"isStart":true})});
            var Q60;
            Q60=makeQuery(id+"F3.boolean.opBoolean","COPY",EDGE,{"derivedFrom":makeQuery(id+"F3.opExtrude","CAP_EDGE",EDGE,{"disambiguationData":[OSD([sQuery(id+"F2.wireOp",EDGE,"E2.1.3.2")])],"isStart":true})});
            var Q61;
            Q61=makeQuery(id+"F3.boolean.opBoolean","COPY",EDGE,{"derivedFrom":makeQuery(id+"F3.opExtrude","CAP_EDGE",EDGE,{"disambiguationData":[OSD([sQuery(id+"F2.wireOp",EDGE,"E2.0.4.2")])],"isStart":true})});
            var Q62;
            Q62=makeQuery(id+"F3.boolean.opBoolean","COPY",EDGE,{"derivedFrom":makeQuery(id+"F3.opExtrude","CAP_EDGE",EDGE,{"disambiguationData":[OSD([sQuery(id+"F2.wireOp",EDGE,"E2.4.4.2")])],"isStart":true})});
            var Q63;
            Q63=makeQuery(id+"F3.boolean.opBoolean","COPY",EDGE,{"derivedFrom":makeQuery(id+"F3.opExtrude","CAP_EDGE",EDGE,{"disambiguationData":[OSD([sQuery(id+"F2.wireOp",EDGE,"E2.5.3.2")])],"isStart":true})});
            var Q64;
            Q64=makeQuery(id+"F3.boolean.opBoolean","COPY",FACE,{"derivedFrom":makeQuery(id+"F3.opExtrude","SWEPT_FACE",FACE,{"disambiguationData":[OSD([sQuery(id+"F2.wireOp",EDGE,"E2.1.4.3")])]})});
            var Q65;
            Q65=makeQuery(id+"F3.boolean.opBoolean","COPY",EDGE,{"derivedFrom":makeQuery(id+"F3.opExtrude","CAP_EDGE",EDGE,{"disambiguationData":[OSD([sQuery(id+"F2.wireOp",EDGE,"E2.5.3.3")])],"isStart":true})});
            var Q66;
            Q66=makeQuery(id+"F3.boolean.opBoolean","COPY",FACE,{"derivedFrom":makeQuery(id+"F3.opExtrude","SWEPT_FACE",FACE,{"disambiguationData":[OSD([sQuery(id+"F2.wireOp",EDGE,"E2.1.3.0")])]})});
            var Q67;
            Q67=makeQuery(id+"F3.boolean.opBoolean","COPY",FACE,{"derivedFrom":makeQuery(id+"F3.opExtrude","SWEPT_FACE",FACE,{"disambiguationData":[OSD([sQuery(id+"F2.wireOp",EDGE,"E2.0.4.0")])]})});
            var Q68;
            Q68=makeQuery(id+"F3.boolean.opBoolean","COPY",FACE,{"derivedFrom":makeQuery(id+"F3.opExtrude","SWEPT_FACE",FACE,{"disambiguationData":[OSD([sQuery(id+"F2.wireOp",EDGE,"E2.6.2.0")])]})});
            var Q69;
            Q69=makeQuery(id+"F3.boolean.opBoolean","COPY",FACE,{"derivedFrom":makeQuery(id+"F3.opExtrude","SWEPT_FACE",FACE,{"disambiguationData":[OSD([sQuery(id+"F2.wireOp",EDGE,"E2.4.4.0")])]})});
            var Q70;
            Q70=makeQuery(id+"F3.boolean.opBoolean","COPY",FACE,{"derivedFrom":makeQuery(id+"F3.opExtrude","SWEPT_FACE",FACE,{"disambiguationData":[OSD([sQuery(id+"F2.wireOp",EDGE,"E2.5.3.0")])]})});
            var Q71;
            Q71=makeQuery(id+"F3.boolean.opBoolean","COPY",EDGE,{"derivedFrom":makeQuery(id+"F3.opExtrude","CAP_EDGE",EDGE,{"disambiguationData":[OSD([sQuery(id+"F2.wireOp",EDGE,"E2.1.4.1")])],"isStart":true})});
            var Q72;
            Q72=makeQuery(id+"F3.boolean.opBoolean","COPY",EDGE,{"derivedFrom":makeQuery(id+"F3.opExtrude","CAP_EDGE",EDGE,{"disambiguationData":[OSD([sQuery(id+"F2.wireOp",EDGE,"E2.3.2.1")])],"isStart":true})});
            var Q73;
            Q73=makeQuery(id+"F3.boolean.opBoolean","COPY",EDGE,{"derivedFrom":makeQuery(id+"F3.opExtrude","CAP_EDGE",EDGE,{"disambiguationData":[OSD([sQuery(id+"F2.wireOp",EDGE,"E2.2.3.1")])],"isStart":true})});
            var Q74;
            Q74=makeQuery(id+"F3.boolean.opBoolean","COPY",EDGE,{"derivedFrom":makeQuery(id+"F3.opExtrude","CAP_EDGE",EDGE,{"disambiguationData":[OSD([sQuery(id+"F2.wireOp",EDGE,"E2.6.3.1")])],"isStart":true})});
            var Q75;
            Q75=makeQuery(id+"F3.boolean.opBoolean","COPY",EDGE,{"derivedFrom":makeQuery(id+"F3.opExtrude","CAP_EDGE",EDGE,{"disambiguationData":[OSD([sQuery(id+"F2.wireOp",EDGE,"E2.5.4.1")])],"isStart":true})});
            var Q76;
            Q76=makeQuery(id+"F3.boolean.opBoolean","COPY",FACE,{"derivedFrom":makeQuery(id+"F3.opExtrude","SWEPT_FACE",FACE,{"disambiguationData":[OSD([sQuery(id+"F2.wireOp",EDGE,"E2.2.2.1")])]})});
            var Q77;
            Q77=makeQuery(id+"F3.boolean.opBoolean","COPY",FACE,{"derivedFrom":makeQuery(id+"F3.opExtrude","SWEPT_FACE",FACE,{"disambiguationData":[OSD([sQuery(id+"F2.wireOp",EDGE,"E2.1.3.1")])]})});
            var Q78;
            Q78=makeQuery(id+"F3.boolean.opBoolean","COPY",FACE,{"derivedFrom":makeQuery(id+"F3.opExtrude","SWEPT_FACE",FACE,{"disambiguationData":[OSD([sQuery(id+"F2.wireOp",EDGE,"E2.6.2.1")])]})});
            var Q79;
            Q79=makeQuery(id+"F3.boolean.opBoolean","COPY",EDGE,{"derivedFrom":makeQuery(id+"F3.opExtrude","CAP_EDGE",EDGE,{"disambiguationData":[OSD([sQuery(id+"F2.wireOp",EDGE,"E2.1.4.2")])],"isStart":true})});
            var Q80;
            Q80=makeQuery(id+"F3.boolean.opBoolean","COPY",EDGE,{"derivedFrom":makeQuery(id+"F3.opExtrude","CAP_EDGE",EDGE,{"disambiguationData":[OSD([sQuery(id+"F2.wireOp",EDGE,"E2.2.3.2")])],"isStart":true})});
            var Q81;
            Q81=makeQuery(id+"F3.boolean.opBoolean","COPY",EDGE,{"derivedFrom":makeQuery(id+"F3.opExtrude","CAP_EDGE",EDGE,{"disambiguationData":[OSD([sQuery(id+"F2.wireOp",EDGE,"E2.6.3.2")])],"isStart":true})});
            var Q82;
            Q82=makeQuery(id+"F3.boolean.opBoolean","COPY",EDGE,{"derivedFrom":makeQuery(id+"F3.opExtrude","CAP_EDGE",EDGE,{"disambiguationData":[OSD([sQuery(id+"F2.wireOp",EDGE,"E2.5.4.2")])],"isStart":true})});
            var Q83;
            Q83=makeQuery(id+"F3.boolean.opBoolean","COPY",FACE,{"derivedFrom":makeQuery(id+"F3.opExtrude","SWEPT_FACE",FACE,{"disambiguationData":[OSD([sQuery(id+"F2.wireOp",EDGE,"E2.1.3.2")])]})});
            var Q84;
            Q84=makeQuery(id+"F3.boolean.opBoolean","COPY",FACE,{"derivedFrom":makeQuery(id+"F3.opExtrude","SWEPT_FACE",FACE,{"disambiguationData":[OSD([sQuery(id+"F2.wireOp",EDGE,"E2.4.4.2")])]})});
            var Q85;
            Q85=makeQuery(id+"F3.boolean.opBoolean","COPY",EDGE,{"derivedFrom":makeQuery(id+"F3.opExtrude","CAP_EDGE",EDGE,{"disambiguationData":[OSD([sQuery(id+"F2.wireOp",EDGE,"E2.2.3.3")])],"isStart":true})});
            var Q86;
            Q86=makeQuery(id+"F1.opExtrude","SWEPT_FACE",FACE,{"disambiguationData":[OSD([sQuery(id+"F0.wireOp",EDGE,"E0.rect.bottom")])]});
            var Q87;
            Q87=makeQuery(id+"F1.opExtrude","SWEPT_FACE",FACE,{"disambiguationData":[OSD([sQuery(id+"F0.wireOp",EDGE,"E0.rect.top")])]});
            var Q88;
            Q88=makeQuery(id+"F1.opExtrude","SWEPT_FACE",FACE,{"disambiguationData":[OSD([sQuery(id+"F0.wireOp",EDGE,"E0.rect.left")])]});
            var Q89;
            Q89=makeQuery(id+"F3.boolean.opBoolean","COPY",FACE,{"derivedFrom":makeQuery(id+"F3.opExtrude","SWEPT_FACE",FACE,{"disambiguationData":[OSD([sQuery(id+"F2.wireOp",EDGE,"E2.2.2.3")])]})});
            var Q90;
            Q90=makeQuery(id+"F3.boolean.opBoolean","COPY",FACE,{"derivedFrom":makeQuery(id+"F3.opExtrude","SWEPT_FACE",FACE,{"disambiguationData":[OSD([sQuery(id+"F2.wireOp",EDGE,"E2.1.3.3")])]})});
            var Q91;
            Q91=makeQuery(id+"F3.boolean.opBoolean","COPY",FACE,{"derivedFrom":makeQuery(id+"F3.opExtrude","SWEPT_FACE",FACE,{"disambiguationData":[OSD([sQuery(id+"F2.wireOp",EDGE,"E2.0.4.3")])]})});
            var Q92;
            Q92=makeQuery(id+"F3.boolean.opBoolean","COPY",FACE,{"derivedFrom":makeQuery(id+"F3.opExtrude","SWEPT_FACE",FACE,{"disambiguationData":[OSD([sQuery(id+"F2.wireOp",EDGE,"E2.6.2.3")])]})});
            var Q93;
            Q93=makeQuery(id+"F3.boolean.opBoolean","COPY",FACE,{"derivedFrom":makeQuery(id+"F3.opExtrude","SWEPT_FACE",FACE,{"disambiguationData":[OSD([sQuery(id+"F2.wireOp",EDGE,"E2.5.3.3")])]})});
            var Q94;
            Q94=makeQuery(id+"F1.opExtrude","CAP_EDGE",EDGE,{"disambiguationData":[OSD([sQuery(id+"F0.wireOp",EDGE,"E0.rect.bottom")])],"isStart":false});
            var Q95;
            Q95=makeQuery(id+"F3.boolean.opBoolean","COPY",FACE,{"derivedFrom":makeQuery(id+"F3.opExtrude","SWEPT_FACE",FACE,{"disambiguationData":[OSD([sQuery(id+"F2.wireOp",EDGE,"E2.4.4.3")])]})});
            var Q96;
            Q96=makeQuery(id+"F1.opExtrude","CAP_EDGE",EDGE,{"disambiguationData":[OSD([sQuery(id+"F0.wireOp",EDGE,"E0.rect.top")])],"isStart":true});
            var Q97;
            Q97=makeQuery(id+"F1.opExtrude","CAP_EDGE",EDGE,{"disambiguationData":[OSD([sQuery(id+"F0.wireOp",EDGE,"E0.rect.top")])],"isStart":false});
            var Q98;
            Q98=makeQuery(id+"F1.opExtrude","CAP_EDGE",EDGE,{"disambiguationData":[OSD([sQuery(id+"F0.wireOp",EDGE,"E0.rect.left")])],"isStart":true});
            var Q99;
            Q99=makeQuery(id+"F1.opExtrude","CAP_EDGE",EDGE,{"disambiguationData":[OSD([sQuery(id+"F0.wireOp",EDGE,"E0.rect.left")])],"isStart":false});
            var Q100;
            Q100=makeQuery(id+"F1.opExtrude","CAP_EDGE",EDGE,{"disambiguationData":[OSD([sQuery(id+"F0.wireOp",EDGE,"E0.rect.right")])],"isStart":false});
            var Q101;
            Q101=makeQuery(id+"F3.boolean.opBoolean","COPY",FACE,{"derivedFrom":makeQuery(id+"F3.opExtrude","SWEPT_FACE",FACE,{"disambiguationData":[OSD([sQuery(id+"F2.wireOp",EDGE,"E2.0.3.3")])]})});
            var Q102;
            Q102=makeQuery(id+"F3.boolean.opBoolean","COPY",FACE,{"derivedFrom":makeQuery(id+"F3.opExtrude","SWEPT_FACE",FACE,{"disambiguationData":[OSD([sQuery(id+"F2.wireOp",EDGE,"E2.0.3.1")])]})});
            var Q103;
            Q103=makeQuery(id+"F3.boolean.opBoolean","COPY",FACE,{"derivedFrom":makeQuery(id+"F3.opExtrude","SWEPT_FACE",FACE,{"disambiguationData":[OSD([sQuery(id+"F2.wireOp",EDGE,"E2.0.3.2")])]})});
            var Q104;
            Q104=makeQuery(id+"F3.boolean.opBoolean","COPY",FACE,{"derivedFrom":makeQuery(id+"F3.opExtrude","SWEPT_FACE",FACE,{"disambiguationData":[OSD([sQuery(id+"F2.wireOp",EDGE,"E2.2.3.0")])]})});
            var Q105;
            Q105=makeQuery(id+"F3.boolean.opBoolean","COPY",FACE,{"derivedFrom":makeQuery(id+"F3.opExtrude","SWEPT_FACE",FACE,{"disambiguationData":[OSD([sQuery(id+"F2.wireOp",EDGE,"E2.1.4.0")])]})});
            var Q106;
            Q106=makeQuery(id+"F3.boolean.opBoolean","COPY",FACE,{"derivedFrom":makeQuery(id+"F3.opExtrude","SWEPT_FACE",FACE,{"disambiguationData":[OSD([sQuery(id+"F2.wireOp",EDGE,"E2.6.3.0")])]})});
            var Q107;
            Q107=makeQuery(id+"F3.boolean.opBoolean","COPY",FACE,{"derivedFrom":makeQuery(id+"F3.opExtrude","SWEPT_FACE",FACE,{"disambiguationData":[OSD([sQuery(id+"F2.wireOp",EDGE,"E2.5.4.0")])]})});
            var Q108;
            Q108=makeQuery(id+"F3.boolean.opBoolean","COPY",FACE,{"derivedFrom":makeQuery(id+"F3.opExtrude","SWEPT_FACE",FACE,{"disambiguationData":[OSD([sQuery(id+"F2.wireOp",EDGE,"E2.5.0.0")])]})});
            var Q109;
            Q109=makeQuery(id+"F3.boolean.opBoolean","COPY",FACE,{"derivedFrom":makeQuery(id+"F3.opExtrude","SWEPT_FACE",FACE,{"disambiguationData":[OSD([sQuery(id+"F2.wireOp",EDGE,"E2.0.2.1")])]})});
            var Q110;
            Q110=makeQuery(id+"F3.boolean.opBoolean","COPY",FACE,{"derivedFrom":makeQuery(id+"F3.opExtrude","SWEPT_FACE",FACE,{"disambiguationData":[OSD([sQuery(id+"F2.wireOp",EDGE,"E2.0.2.2")])]})});
            var Q111;
            Q111=makeQuery(id+"F3.boolean.opBoolean","COPY",FACE,{"derivedFrom":makeQuery(id+"F3.opExtrude","SWEPT_FACE",FACE,{"disambiguationData":[OSD([sQuery(id+"F2.wireOp",EDGE,"E2.0.3.0")])]})});
            var Q112;
            Q112=makeQuery(id+"F3.boolean.opBoolean","COPY",FACE,{"derivedFrom":makeQuery(id+"F3.opExtrude","SWEPT_FACE",FACE,{"disambiguationData":[OSD([sQuery(id+"F2.wireOp",EDGE,"E2.6.3.1")])]})});
            var Q113;
            Q113=makeQuery(id+"F3.boolean.opBoolean","COPY",FACE,{"derivedFrom":makeQuery(id+"F3.opExtrude","SWEPT_FACE",FACE,{"disambiguationData":[OSD([sQuery(id+"F2.wireOp",EDGE,"E2.5.0.1")])]})});
            var Q114;
            Q114=makeQuery(id+"F3.boolean.opBoolean","COPY",EDGE,{"derivedFrom":makeQuery(id+"F3.opExtrude","CAP_EDGE",EDGE,{"disambiguationData":[OSD([sQuery(id+"F2.wireOp",EDGE,"E2.0.2.1")])],"isStart":true})});
            var Q115;
            Q115=makeQuery(id+"F3.boolean.opBoolean","COPY",EDGE,{"derivedFrom":makeQuery(id+"F3.opExtrude","CAP_EDGE",EDGE,{"disambiguationData":[OSD([sQuery(id+"F2.wireOp",EDGE,"E2.4.2.1")])],"isStart":true})});
            var Q116;
            Q116=makeQuery(id+"F3.boolean.opBoolean","COPY",EDGE,{"derivedFrom":makeQuery(id+"F3.opExtrude","CAP_EDGE",EDGE,{"disambiguationData":[OSD([sQuery(id+"F2.wireOp",EDGE,"E2.3.3.1")])],"isStart":true})});
            var Q117;
            Q117=makeQuery(id+"F3.boolean.opBoolean","COPY",EDGE,{"derivedFrom":makeQuery(id+"F3.opExtrude","CAP_EDGE",EDGE,{"disambiguationData":[OSD([sQuery(id+"F2.wireOp",EDGE,"E2.2.4.1")])],"isStart":true})});
            var Q118;
            Q118=makeQuery(id+"F3.boolean.opBoolean","COPY",EDGE,{"derivedFrom":makeQuery(id+"F3.opExtrude","CAP_EDGE",EDGE,{"disambiguationData":[OSD([sQuery(id+"F2.wireOp",EDGE,"E2.6.4.1")])],"isStart":true})});
            var Q119;
            Q119=makeQuery(id+"F3.boolean.opBoolean","COPY",EDGE,{"derivedFrom":makeQuery(id+"F3.opExtrude","CAP_EDGE",EDGE,{"disambiguationData":[OSD([sQuery(id+"F2.wireOp",EDGE,"E2.6.0.1")])],"isStart":true})});
            var Q120;
            Q120=makeQuery(id+"F3.boolean.opBoolean","COPY",EDGE,{"derivedFrom":makeQuery(id+"F3.opExtrude","CAP_EDGE",EDGE,{"disambiguationData":[OSD([sQuery(id+"F2.wireOp",EDGE,"E2.6.3.3")])],"isStart":true})});
            var Q121;
            Q121=makeQuery(id+"F3.boolean.opBoolean","COPY",FACE,{"derivedFrom":makeQuery(id+"F3.opExtrude","SWEPT_FACE",FACE,{"disambiguationData":[OSD([sQuery(id+"F2.wireOp",EDGE,"E2.6.2.2")])]})});
            var Q122;
            Q122=makeQuery(id+"F3.boolean.opBoolean","INTERSECT",EDGE,{"derivedFrom":[makeQuery(id+"F1.opExtrude","CAP_FACE",FACE,{"disambiguationData":[OSD([sQuery(id+"F0.wireOp",EDGE,"E0.rect.bottom"),sQuery(id+"F0.wireOp",EDGE,"E0.rect.top"),sQuery(id+"F0.wireOp",EDGE,"E0.rect.left"),sQuery(id+"F0.wireOp",EDGE,"E0.rect.right")])],"isStart":true}),makeQuery(id+"F3.opExtrude","SWEPT_FACE",FACE,{"disambiguationData":[OSD([sQuery(id+"F2.wireOp",EDGE,"E2.6.4.2")])]})]});
            var Q123;
            Q123=makeQuery(id+"F3.boolean.opBoolean","COPY",EDGE,{"derivedFrom":makeQuery(id+"F3.opExtrude","SWEPT_EDGE",EDGE,{"disambiguationData":[OSD([sQuery(id+"F2.wireOp",EDGE,"E2.6.4.0"),sQuery(id+"F2.wireOp",EDGE,"E2.6.4.2")])]})});
            var Q124;
            Q124=makeQuery(id+"F3.boolean.opBoolean","COPY",EDGE,{"derivedFrom":makeQuery(id+"F3.opExtrude","CAP_EDGE",EDGE,{"disambiguationData":[OSD([sQuery(id+"F2.wireOp",EDGE,"E2.0.3.0")])],"isStart":true})});
            var Q125;
            Q125=makeQuery(id+"F3.boolean.opBoolean","COPY",EDGE,{"derivedFrom":makeQuery(id+"F3.opExtrude","SWEPT_EDGE",EDGE,{"disambiguationData":[OSD([sQuery(id+"F2.wireOp",EDGE,"E2.6.0.0"),sQuery(id+"F2.wireOp",EDGE,"E2.6.0.2")])]})});
            var Q126;
            Q126=makeQuery(id+"F3.boolean.opBoolean","COPY",EDGE,{"derivedFrom":makeQuery(id+"F3.opExtrude","CAP_EDGE",EDGE,{"disambiguationData":[OSD([sQuery(id+"F2.wireOp",EDGE,"E2.3.4.0")])],"isStart":true})});
            var Q127;
            Q127=makeQuery(id+"F3.boolean.opBoolean","COPY",EDGE,{"derivedFrom":makeQuery(id+"F3.opExtrude","CAP_EDGE",EDGE,{"disambiguationData":[OSD([sQuery(id+"F2.wireOp",EDGE,"E2.6.1.0")])],"isStart":true})});
            var Q128;
            Q128=makeQuery(id+"F3.boolean.opBoolean","COPY",EDGE,{"derivedFrom":makeQuery(id+"F3.opExtrude","CAP_EDGE",EDGE,{"disambiguationData":[OSD([sQuery(id+"F2.wireOp",EDGE,"E2.4.3.0")])],"isStart":true})});
            var Q129;
            Q129=makeQuery(id+"F3.boolean.opBoolean","INTERSECT",EDGE,{"derivedFrom":[makeQuery(id+"F1.opExtrude","CAP_FACE",FACE,{"disambiguationData":[OSD([sQuery(id+"F0.wireOp",EDGE,"E0.rect.bottom"),sQuery(id+"F0.wireOp",EDGE,"E0.rect.top"),sQuery(id+"F0.wireOp",EDGE,"E0.rect.left"),sQuery(id+"F0.wireOp",EDGE,"E0.rect.right")])],"isStart":true}),makeQuery(id+"F3.opExtrude","SWEPT_FACE",FACE,{"disambiguationData":[OSD([sQuery(id+"F2.wireOp",EDGE,"E2.1.3.0")])]})]});
            var Q130;
            Q130=makeQuery(id+"F3.boolean.opBoolean","INTERSECT",EDGE,{"derivedFrom":[makeQuery(id+"F1.opExtrude","CAP_FACE",FACE,{"disambiguationData":[OSD([sQuery(id+"F0.wireOp",EDGE,"E0.rect.bottom"),sQuery(id+"F0.wireOp",EDGE,"E0.rect.top"),sQuery(id+"F0.wireOp",EDGE,"E0.rect.left"),sQuery(id+"F0.wireOp",EDGE,"E0.rect.right")])],"isStart":true}),makeQuery(id+"F3.opExtrude","SWEPT_FACE",FACE,{"disambiguationData":[OSD([sQuery(id+"F2.wireOp",EDGE,"E2.0.4.0")])]})]});
            var Q131;
            Q131=makeQuery(id+"F3.boolean.opBoolean","INTERSECT",EDGE,{"derivedFrom":[makeQuery(id+"F1.opExtrude","CAP_FACE",FACE,{"disambiguationData":[OSD([sQuery(id+"F0.wireOp",EDGE,"E0.rect.bottom"),sQuery(id+"F0.wireOp",EDGE,"E0.rect.top"),sQuery(id+"F0.wireOp",EDGE,"E0.rect.left"),sQuery(id+"F0.wireOp",EDGE,"E0.rect.right")])],"isStart":true}),makeQuery(id+"F3.opExtrude","SWEPT_FACE",FACE,{"disambiguationData":[OSD([sQuery(id+"F2.wireOp",EDGE,"E2.6.2.0")])]})]});
            var Q132;
            Q132=makeQuery(id+"F3.boolean.opBoolean","INTERSECT",EDGE,{"derivedFrom":[makeQuery(id+"F1.opExtrude","CAP_FACE",FACE,{"disambiguationData":[OSD([sQuery(id+"F0.wireOp",EDGE,"E0.rect.bottom"),sQuery(id+"F0.wireOp",EDGE,"E0.rect.top"),sQuery(id+"F0.wireOp",EDGE,"E0.rect.left"),sQuery(id+"F0.wireOp",EDGE,"E0.rect.right")])],"isStart":true}),makeQuery(id+"F3.opExtrude","SWEPT_FACE",FACE,{"disambiguationData":[OSD([sQuery(id+"F2.wireOp",EDGE,"E2.5.3.0")])]})]});
            var Q133;
            Q133=makeQuery(id+"F3.boolean.opBoolean","INTERSECT",EDGE,{"derivedFrom":[makeQuery(id+"F1.opExtrude","CAP_FACE",FACE,{"disambiguationData":[OSD([sQuery(id+"F0.wireOp",EDGE,"E0.rect.bottom"),sQuery(id+"F0.wireOp",EDGE,"E0.rect.top"),sQuery(id+"F0.wireOp",EDGE,"E0.rect.left"),sQuery(id+"F0.wireOp",EDGE,"E0.rect.right")])],"isStart":true}),makeQuery(id+"F3.opExtrude","SWEPT_FACE",FACE,{"disambiguationData":[OSD([sQuery(id+"F2.wireOp",EDGE,"E2.4.4.0")])]})]});
            var Q134;
            Q134=makeQuery(id+"F3.boolean.opBoolean","COPY",FACE,{"derivedFrom":makeQuery(id+"F3.opExtrude","SWEPT_FACE",FACE,{"disambiguationData":[OSD([sQuery(id+"F2.wireOp",EDGE,"E2.2.0.0")])]})});
            var Q135;
            Q135=makeQuery(id+"F3.boolean.opBoolean","COPY",FACE,{"derivedFrom":makeQuery(id+"F3.opExtrude","SWEPT_FACE",FACE,{"disambiguationData":[OSD([sQuery(id+"F2.wireOp",EDGE,"E2.1.1.0")])]})});
            var Q136;
            Q136=makeQuery(id+"F3.boolean.opBoolean","COPY",FACE,{"derivedFrom":makeQuery(id+"F3.opExtrude","SWEPT_FACE",FACE,{"disambiguationData":[OSD([sQuery(id+"F2.wireOp",EDGE,"E2.5.1.0")])]})});
            var Q137;
            Q137=makeQuery(id+"F3.boolean.opBoolean","COPY",FACE,{"derivedFrom":makeQuery(id+"F3.opExtrude","SWEPT_FACE",FACE,{"disambiguationData":[OSD([sQuery(id+"F2.wireOp",EDGE,"E2.4.2.0")])]})});
            var Q138;
            Q138=makeQuery(id+"F3.boolean.opBoolean","COPY",EDGE,{"derivedFrom":makeQuery(id+"F3.opExtrude","SWEPT_EDGE",EDGE,{"disambiguationData":[OSD([sQuery(id+"F2.wireOp",EDGE,"E2.1.1.0"),sQuery(id+"F2.wireOp",EDGE,"E2.1.1.3")])]})});
            var Q139;
            Q139=makeQuery(id+"F3.boolean.opBoolean","COPY",EDGE,{"derivedFrom":makeQuery(id+"F3.opExtrude","SWEPT_EDGE",EDGE,{"disambiguationData":[OSD([sQuery(id+"F2.wireOp",EDGE,"E2.4.2.0"),sQuery(id+"F2.wireOp",EDGE,"E2.4.2.3")])]})});
            var Q140;
            Q140=makeQuery(id+"F3.boolean.opBoolean","INTERSECT",EDGE,{"derivedFrom":[makeQuery(id+"F1.opExtrude","CAP_FACE",FACE,{"disambiguationData":[OSD([sQuery(id+"F0.wireOp",EDGE,"E0.rect.bottom"),sQuery(id+"F0.wireOp",EDGE,"E0.rect.top"),sQuery(id+"F0.wireOp",EDGE,"E0.rect.left"),sQuery(id+"F0.wireOp",EDGE,"E0.rect.right")])],"isStart":true}),makeQuery(id+"F3.opExtrude","SWEPT_FACE",FACE,{"disambiguationData":[OSD([sQuery(id+"F2.wireOp",EDGE,"E2.6.1.2")])]})]});
            var Q141;
            Q141=makeQuery(id+"F3.boolean.opBoolean","COPY",EDGE,{"derivedFrom":makeQuery(id+"F3.opExtrude","SWEPT_EDGE",EDGE,{"disambiguationData":[OSD([sQuery(id+"F2.wireOp",EDGE,"E2.3.3.0"),sQuery(id+"F2.wireOp",EDGE,"E2.3.3.3")])]})});
            var Q142;
            Q142=makeQuery(id+"F3.boolean.opBoolean","COPY",EDGE,{"derivedFrom":makeQuery(id+"F3.opExtrude","SWEPT_EDGE",EDGE,{"disambiguationData":[OSD([sQuery(id+"F2.wireOp",EDGE,"E2.2.0.0"),sQuery(id+"F2.wireOp",EDGE,"E2.2.0.3")])]})});
            var Q143;
            Q143=makeQuery(id+"F3.boolean.opBoolean","COPY",EDGE,{"derivedFrom":makeQuery(id+"F3.opExtrude","SWEPT_EDGE",EDGE,{"disambiguationData":[OSD([sQuery(id+"F2.wireOp",EDGE,"E2.2.4.0"),sQuery(id+"F2.wireOp",EDGE,"E2.2.4.3")])]})});
            var Q144;
            Q144=makeQuery(id+"F3.boolean.opBoolean","COPY",EDGE,{"derivedFrom":makeQuery(id+"F3.opExtrude","SWEPT_EDGE",EDGE,{"disambiguationData":[OSD([sQuery(id+"F2.wireOp",EDGE,"E2.6.4.0"),sQuery(id+"F2.wireOp",EDGE,"E2.6.4.3")])]})});
            var Q145;
            Q145=makeQuery(id+"F3.boolean.opBoolean","COPY",EDGE,{"derivedFrom":makeQuery(id+"F3.opExtrude","SWEPT_EDGE",EDGE,{"disambiguationData":[OSD([sQuery(id+"F2.wireOp",EDGE,"E2.6.0.0"),sQuery(id+"F2.wireOp",EDGE,"E2.6.0.3")])]})});
            var Q146;
            Q146=makeQuery(id+"F3.boolean.opBoolean","COPY",EDGE,{"derivedFrom":makeQuery(id+"F3.opExtrude","SWEPT_EDGE",EDGE,{"disambiguationData":[OSD([sQuery(id+"F2.wireOp",EDGE,"E2.5.1.0"),sQuery(id+"F2.wireOp",EDGE,"E2.5.1.3")])]})});
            var Q147;
            Q147=makeQuery(id+"F3.boolean.opBoolean","COPY",EDGE,{"derivedFrom":makeQuery(id+"F3.opExtrude","CAP_EDGE",EDGE,{"disambiguationData":[OSD([sQuery(id+"F2.wireOp",EDGE,"E2.2.0.2")])],"isStart":true})});
            var Q148;
            Q148=makeQuery(id+"F3.boolean.opBoolean","COPY",EDGE,{"derivedFrom":makeQuery(id+"F3.opExtrude","CAP_EDGE",EDGE,{"disambiguationData":[OSD([sQuery(id+"F2.wireOp",EDGE,"E2.1.1.2")])],"isStart":true})});
            var Q149;
            Q149=makeQuery(id+"F3.boolean.opBoolean","COPY",EDGE,{"derivedFrom":makeQuery(id+"F3.opExtrude","SWEPT_EDGE",EDGE,{"disambiguationData":[OSD([sQuery(id+"F2.wireOp",EDGE,"E2.6.3.1"),sQuery(id+"F2.wireOp",EDGE,"E2.6.3.2")])]})});
            var Q150;
            Q150=makeQuery(id+"F3.boolean.opBoolean","COPY",EDGE,{"derivedFrom":makeQuery(id+"F3.opExtrude","CAP_EDGE",EDGE,{"disambiguationData":[OSD([sQuery(id+"F2.wireOp",EDGE,"E2.5.1.2")])],"isStart":true})});
            var Q151;
            Q151=makeQuery(id+"F3.boolean.opBoolean","COPY",EDGE,{"derivedFrom":makeQuery(id+"F3.opExtrude","CAP_EDGE",EDGE,{"disambiguationData":[OSD([sQuery(id+"F2.wireOp",EDGE,"E2.4.2.2")])],"isStart":true})});
            var Q152;
            Q152=makeQuery(id+"F3.boolean.opBoolean","INTERSECT",EDGE,{"derivedFrom":[makeQuery(id+"F1.opExtrude","CAP_FACE",FACE,{"disambiguationData":[OSD([sQuery(id+"F0.wireOp",EDGE,"E0.rect.bottom"),sQuery(id+"F0.wireOp",EDGE,"E0.rect.top"),sQuery(id+"F0.wireOp",EDGE,"E0.rect.left"),sQuery(id+"F0.wireOp",EDGE,"E0.rect.right")])],"isStart":true}),makeQuery(id+"F3.opExtrude","SWEPT_FACE",FACE,{"disambiguationData":[OSD([sQuery(id+"F2.wireOp",EDGE,"E2.1.2.2")])]})]});
            var Q153;
            Q153=makeQuery(id+"F3.boolean.opBoolean","INTERSECT",EDGE,{"derivedFrom":[makeQuery(id+"F1.opExtrude","CAP_FACE",FACE,{"disambiguationData":[OSD([sQuery(id+"F0.wireOp",EDGE,"E0.rect.bottom"),sQuery(id+"F0.wireOp",EDGE,"E0.rect.top"),sQuery(id+"F0.wireOp",EDGE,"E0.rect.left"),sQuery(id+"F0.wireOp",EDGE,"E0.rect.right")])],"isStart":true}),makeQuery(id+"F3.opExtrude","SWEPT_FACE",FACE,{"disambiguationData":[OSD([sQuery(id+"F2.wireOp",EDGE,"E2.0.3.2")])]})]});
            var Q154;
            Q154=makeQuery(id+"F3.boolean.opBoolean","COPY",FACE,{"derivedFrom":makeQuery(id+"F3.opExtrude","SWEPT_FACE",FACE,{"disambiguationData":[OSD([sQuery(id+"F2.wireOp",EDGE,"E2.5.0.2")])]})});
            var Q155;
            Q155=makeQuery(id+"F3.boolean.opBoolean","COPY",FACE,{"derivedFrom":makeQuery(id+"F3.opExtrude","SWEPT_FACE",FACE,{"disambiguationData":[OSD([sQuery(id+"F2.wireOp",EDGE,"E2.1.0.2")])]})});
            var Q156;
            Q156=makeQuery(id+"F3.boolean.opBoolean","COPY",FACE,{"derivedFrom":makeQuery(id+"F3.opExtrude","SWEPT_FACE",FACE,{"disambiguationData":[OSD([sQuery(id+"F2.wireOp",EDGE,"E2.4.1.2")])]})});
            var Q157;
            Q157=makeQuery(id+"F3.boolean.opBoolean","COPY",FACE,{"derivedFrom":makeQuery(id+"F3.opExtrude","SWEPT_FACE",FACE,{"disambiguationData":[OSD([sQuery(id+"F2.wireOp",EDGE,"E2.3.2.2")])]})});
            var Q158;
            Q158=makeQuery(id+"F3.boolean.opBoolean","COPY",EDGE,{"derivedFrom":makeQuery(id+"F3.opExtrude","CAP_EDGE",EDGE,{"disambiguationData":[OSD([sQuery(id+"F2.wireOp",EDGE,"E2.3.0.1")])],"isStart":true})});
            var Q159;
            Q159=makeQuery(id+"F3.boolean.opBoolean","COPY",EDGE,{"derivedFrom":makeQuery(id+"F3.opExtrude","CAP_EDGE",EDGE,{"disambiguationData":[OSD([sQuery(id+"F2.wireOp",EDGE,"E2.2.1.1")])],"isStart":true})});
            var Q160;
            Q160=makeQuery(id+"F3.boolean.opBoolean","INTERSECT",EDGE,{"derivedFrom":[makeQuery(id+"F1.opExtrude","CAP_FACE",FACE,{"disambiguationData":[OSD([sQuery(id+"F0.wireOp",EDGE,"E0.rect.bottom"),sQuery(id+"F0.wireOp",EDGE,"E0.rect.top"),sQuery(id+"F0.wireOp",EDGE,"E0.rect.left"),sQuery(id+"F0.wireOp",EDGE,"E0.rect.right")])],"isStart":true}),makeQuery(id+"F3.opExtrude","SWEPT_FACE",FACE,{"disambiguationData":[OSD([sQuery(id+"F2.wireOp",EDGE,"E1.top")])]})]});
            var Q161;
            Q161=makeQuery(id+"F3.boolean.opBoolean","COPY",EDGE,{"derivedFrom":makeQuery(id+"F3.opExtrude","CAP_EDGE",EDGE,{"disambiguationData":[OSD([sQuery(id+"F2.wireOp",EDGE,"E2.4.3.1")])],"isStart":true})});
            var Q162;
            Q162=makeQuery(id+"F3.boolean.opBoolean","INTERSECT",EDGE,{"derivedFrom":[makeQuery(id+"F1.opExtrude","CAP_FACE",FACE,{"disambiguationData":[OSD([sQuery(id+"F0.wireOp",EDGE,"E0.rect.bottom"),sQuery(id+"F0.wireOp",EDGE,"E0.rect.top"),sQuery(id+"F0.wireOp",EDGE,"E0.rect.left"),sQuery(id+"F0.wireOp",EDGE,"E0.rect.right")])],"isStart":true}),makeQuery(id+"F3.opExtrude","SWEPT_FACE",FACE,{"disambiguationData":[OSD([sQuery(id+"F2.wireOp",EDGE,"E2.3.1.1")])]})]});
            var Q163;
            Q163=makeQuery(id+"F3.boolean.opBoolean","INTERSECT",EDGE,{"derivedFrom":[makeQuery(id+"F1.opExtrude","CAP_FACE",FACE,{"disambiguationData":[OSD([sQuery(id+"F0.wireOp",EDGE,"E0.rect.bottom"),sQuery(id+"F0.wireOp",EDGE,"E0.rect.top"),sQuery(id+"F0.wireOp",EDGE,"E0.rect.left"),sQuery(id+"F0.wireOp",EDGE,"E0.rect.right")])],"isStart":true}),makeQuery(id+"F3.opExtrude","SWEPT_FACE",FACE,{"disambiguationData":[OSD([sQuery(id+"F2.wireOp",EDGE,"E2.2.2.1")])]})]});
            var Q164;
            Q164=makeQuery(id+"F3.boolean.opBoolean","INTERSECT",EDGE,{"derivedFrom":[makeQuery(id+"F1.opExtrude","CAP_FACE",FACE,{"disambiguationData":[OSD([sQuery(id+"F0.wireOp",EDGE,"E0.rect.bottom"),sQuery(id+"F0.wireOp",EDGE,"E0.rect.top"),sQuery(id+"F0.wireOp",EDGE,"E0.rect.left"),sQuery(id+"F0.wireOp",EDGE,"E0.rect.right")])],"isStart":true}),makeQuery(id+"F3.opExtrude","SWEPT_FACE",FACE,{"disambiguationData":[OSD([sQuery(id+"F2.wireOp",EDGE,"E2.1.3.1")])]})]});
            var Q165;
            Q165=makeQuery(id+"F3.boolean.opBoolean","INTERSECT",EDGE,{"derivedFrom":[makeQuery(id+"F1.opExtrude","CAP_FACE",FACE,{"disambiguationData":[OSD([sQuery(id+"F0.wireOp",EDGE,"E0.rect.bottom"),sQuery(id+"F0.wireOp",EDGE,"E0.rect.top"),sQuery(id+"F0.wireOp",EDGE,"E0.rect.left"),sQuery(id+"F0.wireOp",EDGE,"E0.rect.right")])],"isStart":true}),makeQuery(id+"F3.opExtrude","SWEPT_FACE",FACE,{"disambiguationData":[OSD([sQuery(id+"F2.wireOp",EDGE,"E2.0.4.1")])]})]});
            var Q166;
            Q166=makeQuery(id+"F3.boolean.opBoolean","INTERSECT",EDGE,{"derivedFrom":[makeQuery(id+"F1.opExtrude","CAP_FACE",FACE,{"disambiguationData":[OSD([sQuery(id+"F0.wireOp",EDGE,"E0.rect.bottom"),sQuery(id+"F0.wireOp",EDGE,"E0.rect.top"),sQuery(id+"F0.wireOp",EDGE,"E0.rect.left"),sQuery(id+"F0.wireOp",EDGE,"E0.rect.right")])],"isStart":true}),makeQuery(id+"F3.opExtrude","SWEPT_FACE",FACE,{"disambiguationData":[OSD([sQuery(id+"F2.wireOp",EDGE,"E2.6.2.1")])]})]});
            var Q167;
            Q167=makeQuery(id+"F3.boolean.opBoolean","INTERSECT",EDGE,{"derivedFrom":[makeQuery(id+"F1.opExtrude","CAP_FACE",FACE,{"disambiguationData":[OSD([sQuery(id+"F0.wireOp",EDGE,"E0.rect.bottom"),sQuery(id+"F0.wireOp",EDGE,"E0.rect.top"),sQuery(id+"F0.wireOp",EDGE,"E0.rect.left"),sQuery(id+"F0.wireOp",EDGE,"E0.rect.right")])],"isStart":true}),makeQuery(id+"F3.opExtrude","SWEPT_FACE",FACE,{"disambiguationData":[OSD([sQuery(id+"F2.wireOp",EDGE,"E2.5.3.1")])]})]});
            var Q168;
            Q168=makeQuery(id+"F3.boolean.opBoolean","INTERSECT",EDGE,{"derivedFrom":[makeQuery(id+"F1.opExtrude","CAP_FACE",FACE,{"disambiguationData":[OSD([sQuery(id+"F0.wireOp",EDGE,"E0.rect.bottom"),sQuery(id+"F0.wireOp",EDGE,"E0.rect.top"),sQuery(id+"F0.wireOp",EDGE,"E0.rect.left"),sQuery(id+"F0.wireOp",EDGE,"E0.rect.right")])],"isStart":true}),makeQuery(id+"F3.opExtrude","SWEPT_FACE",FACE,{"disambiguationData":[OSD([sQuery(id+"F2.wireOp",EDGE,"E2.4.4.1")])]})]});
            var Q169;
            Q169=makeQuery(id+"F3.boolean.opBoolean","INTERSECT",EDGE,{"derivedFrom":[makeQuery(id+"F1.opExtrude","CAP_FACE",FACE,{"disambiguationData":[OSD([sQuery(id+"F0.wireOp",EDGE,"E0.rect.bottom"),sQuery(id+"F0.wireOp",EDGE,"E0.rect.top"),sQuery(id+"F0.wireOp",EDGE,"E0.rect.left"),sQuery(id+"F0.wireOp",EDGE,"E0.rect.right")])],"isStart":true}),makeQuery(id+"F3.opExtrude","SWEPT_FACE",FACE,{"disambiguationData":[OSD([sQuery(id+"F2.wireOp",EDGE,"E2.4.0.1")])]})]});
            var Q170;
            Q170=makeQuery(id+"F3.boolean.opBoolean","COPY",FACE,{"derivedFrom":makeQuery(id+"F3.opExtrude","SWEPT_FACE",FACE,{"disambiguationData":[OSD([sQuery(id+"F2.wireOp",EDGE,"E2.2.0.1")])]})});
            var Q171;
            Q171=makeQuery(id+"F3.boolean.opBoolean","COPY",FACE,{"derivedFrom":makeQuery(id+"F3.opExtrude","SWEPT_FACE",FACE,{"disambiguationData":[OSD([sQuery(id+"F2.wireOp",EDGE,"E2.1.1.1")])]})});
            var Q172;
            Q172=makeQuery(id+"F3.boolean.opBoolean","COPY",FACE,{"derivedFrom":makeQuery(id+"F3.opExtrude","SWEPT_FACE",FACE,{"disambiguationData":[OSD([sQuery(id+"F2.wireOp",EDGE,"E2.5.1.1")])]})});
            var Q173;
            Q173=makeQuery(id+"F3.boolean.opBoolean","COPY",FACE,{"derivedFrom":makeQuery(id+"F3.opExtrude","SWEPT_FACE",FACE,{"disambiguationData":[OSD([sQuery(id+"F2.wireOp",EDGE,"E2.4.2.1")])]})});
            var Q174;
            Q174=makeQuery(id+"F3.boolean.opBoolean","COPY",FACE,{"derivedFrom":makeQuery(id+"F3.opExtrude","SWEPT_FACE",FACE,{"disambiguationData":[OSD([sQuery(id+"F2.wireOp",EDGE,"E2.3.3.1")])]})});
            var Q175;
            Q175=makeQuery(id+"F3.boolean.opBoolean","COPY",EDGE,{"derivedFrom":makeQuery(id+"F3.opExtrude","SWEPT_EDGE",EDGE,{"disambiguationData":[OSD([sQuery(id+"F2.wireOp",EDGE,"E2.2.4.1"),sQuery(id+"F2.wireOp",EDGE,"E2.2.4.2")])]})});
            var Q176;
            Q176=makeQuery(id+"F3.boolean.opBoolean","COPY",EDGE,{"derivedFrom":makeQuery(id+"F3.opExtrude","SWEPT_EDGE",EDGE,{"disambiguationData":[OSD([sQuery(id+"F2.wireOp",EDGE,"E2.6.4.1"),sQuery(id+"F2.wireOp",EDGE,"E2.6.4.2")])]})});
            var Q177;
            Q177=makeQuery(id+"F3.boolean.opBoolean","COPY",EDGE,{"derivedFrom":makeQuery(id+"F3.opExtrude","SWEPT_EDGE",EDGE,{"disambiguationData":[OSD([sQuery(id+"F2.wireOp",EDGE,"E2.6.0.1"),sQuery(id+"F2.wireOp",EDGE,"E2.6.0.2")])]})});
            var Q178;
            Q178=makeQuery(id+"F3.boolean.opBoolean","COPY",EDGE,{"derivedFrom":makeQuery(id+"F3.opExtrude","CAP_EDGE",EDGE,{"disambiguationData":[OSD([sQuery(id+"F2.wireOp",EDGE,"E2.3.0.2")])],"isStart":true})});
            var Q179;
            Q179=makeQuery(id+"F3.boolean.opBoolean","COPY",EDGE,{"derivedFrom":makeQuery(id+"F3.opExtrude","CAP_EDGE",EDGE,{"disambiguationData":[OSD([sQuery(id+"F2.wireOp",EDGE,"E2.2.1.2")])],"isStart":true})});
            var Q180;
            Q180=makeQuery(id+"F3.boolean.opBoolean","COPY",EDGE,{"derivedFrom":makeQuery(id+"F3.opExtrude","CAP_EDGE",EDGE,{"disambiguationData":[OSD([sQuery(id+"F2.wireOp",EDGE,"E2.1.2.2")])],"isStart":true})});
            var Q181;
            Q181=makeQuery(id+"F3.boolean.opBoolean","COPY",EDGE,{"derivedFrom":makeQuery(id+"F3.opExtrude","CAP_EDGE",EDGE,{"disambiguationData":[OSD([sQuery(id+"F2.wireOp",EDGE,"E2.5.2.2")])],"isStart":true})});
            var Q182;
            Q182=makeQuery(id+"F3.boolean.opBoolean","COPY",EDGE,{"derivedFrom":makeQuery(id+"F3.opExtrude","CAP_EDGE",EDGE,{"disambiguationData":[OSD([sQuery(id+"F2.wireOp",EDGE,"E2.4.3.2")])],"isStart":true})});
            var Q183;
            Q183=makeQuery(id+"F3.boolean.opBoolean","INTERSECT",EDGE,{"derivedFrom":[makeQuery(id+"F1.opExtrude","CAP_FACE",FACE,{"disambiguationData":[OSD([sQuery(id+"F0.wireOp",EDGE,"E0.rect.bottom"),sQuery(id+"F0.wireOp",EDGE,"E0.rect.top"),sQuery(id+"F0.wireOp",EDGE,"E0.rect.left"),sQuery(id+"F0.wireOp",EDGE,"E0.rect.right")])],"isStart":true}),makeQuery(id+"F3.opExtrude","SWEPT_FACE",FACE,{"disambiguationData":[OSD([sQuery(id+"F2.wireOp",EDGE,"E2.2.2.2")])]})]});
            var Q184;
            Q184=makeQuery(id+"F3.boolean.opBoolean","INTERSECT",EDGE,{"derivedFrom":[makeQuery(id+"F1.opExtrude","CAP_FACE",FACE,{"disambiguationData":[OSD([sQuery(id+"F0.wireOp",EDGE,"E0.rect.bottom"),sQuery(id+"F0.wireOp",EDGE,"E0.rect.top"),sQuery(id+"F0.wireOp",EDGE,"E0.rect.left"),sQuery(id+"F0.wireOp",EDGE,"E0.rect.right")])],"isStart":true}),makeQuery(id+"F3.opExtrude","SWEPT_FACE",FACE,{"disambiguationData":[OSD([sQuery(id+"F2.wireOp",EDGE,"E2.1.3.2")])]})]});
            var Q185;
            Q185=makeQuery(id+"F3.boolean.opBoolean","INTERSECT",EDGE,{"derivedFrom":[makeQuery(id+"F1.opExtrude","CAP_FACE",FACE,{"disambiguationData":[OSD([sQuery(id+"F0.wireOp",EDGE,"E0.rect.bottom"),sQuery(id+"F0.wireOp",EDGE,"E0.rect.top"),sQuery(id+"F0.wireOp",EDGE,"E0.rect.left"),sQuery(id+"F0.wireOp",EDGE,"E0.rect.right")])],"isStart":true}),makeQuery(id+"F3.opExtrude","SWEPT_FACE",FACE,{"disambiguationData":[OSD([sQuery(id+"F2.wireOp",EDGE,"E2.6.2.2")])]})]});
            var Q186;
            Q186=makeQuery(id+"F3.boolean.opBoolean","COPY",FACE,{"derivedFrom":makeQuery(id+"F3.opExtrude","SWEPT_FACE",FACE,{"disambiguationData":[OSD([sQuery(id+"F2.wireOp",EDGE,"E2.2.0.2")])]})});
            var Q187;
            Q187=makeQuery(id+"F3.boolean.opBoolean","COPY",FACE,{"derivedFrom":makeQuery(id+"F3.opExtrude","SWEPT_FACE",FACE,{"disambiguationData":[OSD([sQuery(id+"F2.wireOp",EDGE,"E2.1.1.2")])]})});
            var Q188;
            Q188=makeQuery(id+"F3.boolean.opBoolean","COPY",FACE,{"derivedFrom":makeQuery(id+"F3.opExtrude","SWEPT_FACE",FACE,{"disambiguationData":[OSD([sQuery(id+"F2.wireOp",EDGE,"E2.5.1.2")])]})});
            var Q189;
            Q189=makeQuery(id+"F3.boolean.opBoolean","COPY",FACE,{"derivedFrom":makeQuery(id+"F3.opExtrude","SWEPT_FACE",FACE,{"disambiguationData":[OSD([sQuery(id+"F2.wireOp",EDGE,"E2.4.2.2")])]})});
            var Q190;
            Q190=makeQuery(id+"F3.boolean.opBoolean","COPY",EDGE,{"derivedFrom":makeQuery(id+"F3.opExtrude","SWEPT_EDGE",EDGE,{"disambiguationData":[OSD([sQuery(id+"F2.wireOp",EDGE,"E2.2.4.1"),sQuery(id+"F2.wireOp",EDGE,"E2.2.4.3")])]})});
            var Q191;
            Q191=makeQuery(id+"F3.boolean.opBoolean","COPY",EDGE,{"derivedFrom":makeQuery(id+"F3.opExtrude","CAP_EDGE",EDGE,{"disambiguationData":[OSD([sQuery(id+"F2.wireOp",EDGE,"E2.0.3.3")])],"isStart":true})});
            var Q192;
            Q192=makeQuery(id+"F3.boolean.opBoolean","COPY",EDGE,{"derivedFrom":makeQuery(id+"F3.opExtrude","SWEPT_EDGE",EDGE,{"disambiguationData":[OSD([sQuery(id+"F2.wireOp",EDGE,"E2.6.4.1"),sQuery(id+"F2.wireOp",EDGE,"E2.6.4.3")])]})});
            var Q193;
            Q193=makeQuery(id+"F3.boolean.opBoolean","COPY",EDGE,{"derivedFrom":makeQuery(id+"F3.opExtrude","SWEPT_EDGE",EDGE,{"disambiguationData":[OSD([sQuery(id+"F2.wireOp",EDGE,"E2.6.0.1"),sQuery(id+"F2.wireOp",EDGE,"E2.6.0.3")])]})});
            var Q194;
            Q194=makeQuery(id+"F3.boolean.opBoolean","COPY",EDGE,{"derivedFrom":makeQuery(id+"F3.opExtrude","CAP_EDGE",EDGE,{"disambiguationData":[OSD([sQuery(id+"F2.wireOp",EDGE,"E2.3.4.3")])],"isStart":true})});
            var Q195;
            Q195=makeQuery(id+"F3.boolean.opBoolean","COPY",EDGE,{"derivedFrom":makeQuery(id+"F3.opExtrude","CAP_EDGE",EDGE,{"disambiguationData":[OSD([sQuery(id+"F2.wireOp",EDGE,"E2.2.1.3")])],"isStart":true})});
            var Q196;
            Q196=makeQuery(id+"F3.boolean.opBoolean","COPY",EDGE,{"derivedFrom":makeQuery(id+"F3.opExtrude","CAP_EDGE",EDGE,{"disambiguationData":[OSD([sQuery(id+"F2.wireOp",EDGE,"E2.1.2.3")])],"isStart":true})});
            var Q197;
            Q197=makeQuery(id+"F3.boolean.opBoolean","COPY",EDGE,{"derivedFrom":makeQuery(id+"F3.opExtrude","CAP_EDGE",EDGE,{"disambiguationData":[OSD([sQuery(id+"F2.wireOp",EDGE,"E2.6.1.3")])],"isStart":true})});
            var Q198;
            Q198=makeQuery(id+"F3.boolean.opBoolean","COPY",EDGE,{"derivedFrom":makeQuery(id+"F3.opExtrude","CAP_EDGE",EDGE,{"disambiguationData":[OSD([sQuery(id+"F2.wireOp",EDGE,"E2.5.2.3")])],"isStart":true})});
            var Q199;
            Q199=makeQuery(id+"F3.boolean.opBoolean","COPY",EDGE,{"derivedFrom":makeQuery(id+"F3.opExtrude","CAP_EDGE",EDGE,{"disambiguationData":[OSD([sQuery(id+"F2.wireOp",EDGE,"E2.4.3.3")])],"isStart":true})});
            var Q200;
            Q200=makeQuery(id+"F3.boolean.opBoolean","INTERSECT",EDGE,{"derivedFrom":[makeQuery(id+"F1.opExtrude","CAP_FACE",FACE,{"disambiguationData":[OSD([sQuery(id+"F0.wireOp",EDGE,"E0.rect.bottom"),sQuery(id+"F0.wireOp",EDGE,"E0.rect.top"),sQuery(id+"F0.wireOp",EDGE,"E0.rect.left"),sQuery(id+"F0.wireOp",EDGE,"E0.rect.right")])],"isStart":true}),makeQuery(id+"F3.opExtrude","SWEPT_FACE",FACE,{"disambiguationData":[OSD([sQuery(id+"F2.wireOp",EDGE,"E2.2.2.3")])]})]});
            var Q201;
            Q201=makeQuery(id+"F3.boolean.opBoolean","INTERSECT",EDGE,{"derivedFrom":[makeQuery(id+"F1.opExtrude","CAP_FACE",FACE,{"disambiguationData":[OSD([sQuery(id+"F0.wireOp",EDGE,"E0.rect.bottom"),sQuery(id+"F0.wireOp",EDGE,"E0.rect.top"),sQuery(id+"F0.wireOp",EDGE,"E0.rect.left"),sQuery(id+"F0.wireOp",EDGE,"E0.rect.right")])],"isStart":true}),makeQuery(id+"F3.opExtrude","SWEPT_FACE",FACE,{"disambiguationData":[OSD([sQuery(id+"F2.wireOp",EDGE,"E2.1.3.3")])]})]});
            var Q202;
            Q202=makeQuery(id+"F3.boolean.opBoolean","INTERSECT",EDGE,{"derivedFrom":[makeQuery(id+"F1.opExtrude","CAP_FACE",FACE,{"disambiguationData":[OSD([sQuery(id+"F0.wireOp",EDGE,"E0.rect.bottom"),sQuery(id+"F0.wireOp",EDGE,"E0.rect.top"),sQuery(id+"F0.wireOp",EDGE,"E0.rect.left"),sQuery(id+"F0.wireOp",EDGE,"E0.rect.right")])],"isStart":true}),makeQuery(id+"F3.opExtrude","SWEPT_FACE",FACE,{"disambiguationData":[OSD([sQuery(id+"F2.wireOp",EDGE,"E2.0.4.3")])]})]});
            var Q203;
            Q203=makeQuery(id+"F3.boolean.opBoolean","INTERSECT",EDGE,{"derivedFrom":[makeQuery(id+"F1.opExtrude","CAP_FACE",FACE,{"disambiguationData":[OSD([sQuery(id+"F0.wireOp",EDGE,"E0.rect.bottom"),sQuery(id+"F0.wireOp",EDGE,"E0.rect.top"),sQuery(id+"F0.wireOp",EDGE,"E0.rect.left"),sQuery(id+"F0.wireOp",EDGE,"E0.rect.right")])],"isStart":true}),makeQuery(id+"F3.opExtrude","SWEPT_FACE",FACE,{"disambiguationData":[OSD([sQuery(id+"F2.wireOp",EDGE,"E2.6.2.3")])]})]});
            var Q204;
            Q204=makeQuery(id+"F3.boolean.opBoolean","INTERSECT",EDGE,{"derivedFrom":[makeQuery(id+"F1.opExtrude","CAP_FACE",FACE,{"disambiguationData":[OSD([sQuery(id+"F0.wireOp",EDGE,"E0.rect.bottom"),sQuery(id+"F0.wireOp",EDGE,"E0.rect.top"),sQuery(id+"F0.wireOp",EDGE,"E0.rect.left"),sQuery(id+"F0.wireOp",EDGE,"E0.rect.right")])],"isStart":true}),makeQuery(id+"F3.opExtrude","SWEPT_FACE",FACE,{"disambiguationData":[OSD([sQuery(id+"F2.wireOp",EDGE,"E2.5.3.3")])]})]});
            var Q205;
            Q205=makeQuery(id+"F3.boolean.opBoolean","INTERSECT",EDGE,{"derivedFrom":[makeQuery(id+"F1.opExtrude","CAP_FACE",FACE,{"disambiguationData":[OSD([sQuery(id+"F0.wireOp",EDGE,"E0.rect.bottom"),sQuery(id+"F0.wireOp",EDGE,"E0.rect.top"),sQuery(id+"F0.wireOp",EDGE,"E0.rect.left"),sQuery(id+"F0.wireOp",EDGE,"E0.rect.right")])],"isStart":true}),makeQuery(id+"F3.opExtrude","SWEPT_FACE",FACE,{"disambiguationData":[OSD([sQuery(id+"F2.wireOp",EDGE,"E2.4.4.3")])]})]});
            var Q206;
            Q206=makeQuery(id+"F3.boolean.opBoolean","COPY",FACE,{"derivedFrom":makeQuery(id+"F3.opExtrude","SWEPT_FACE",FACE,{"disambiguationData":[OSD([sQuery(id+"F2.wireOp",EDGE,"E2.2.0.3")])]})});
            var Q207;
            Q207=makeQuery(id+"F3.boolean.opBoolean","COPY",FACE,{"derivedFrom":makeQuery(id+"F3.opExtrude","SWEPT_FACE",FACE,{"disambiguationData":[OSD([sQuery(id+"F2.wireOp",EDGE,"E2.1.1.3")])]})});
            var Q208;
            Q208=makeQuery(id+"F3.boolean.opBoolean","COPY",FACE,{"derivedFrom":makeQuery(id+"F3.opExtrude","SWEPT_FACE",FACE,{"disambiguationData":[OSD([sQuery(id+"F2.wireOp",EDGE,"E2.5.1.3")])]})});
            var Q209;
            Q209=makeQuery(id+"F3.boolean.opBoolean","COPY",FACE,{"derivedFrom":makeQuery(id+"F3.opExtrude","SWEPT_FACE",FACE,{"disambiguationData":[OSD([sQuery(id+"F2.wireOp",EDGE,"E2.4.2.3")])]})});
            var Q210;
            Q210=makeQuery(id+"F3.boolean.opBoolean","COPY",FACE,{"derivedFrom":makeQuery(id+"F3.opExtrude","SWEPT_FACE",FACE,{"disambiguationData":[OSD([sQuery(id+"F2.wireOp",EDGE,"E2.3.3.3")])]})});
            var Q211;
            Q211=makeQuery(id+"F3.boolean.opBoolean","COPY",EDGE,{"derivedFrom":makeQuery(id+"F3.opExtrude","SWEPT_EDGE",EDGE,{"disambiguationData":[OSD([sQuery(id+"F2.wireOp",EDGE,"E2.3.4.0"),sQuery(id+"F2.wireOp",EDGE,"E2.3.4.2")])]})});
            var Q212;
            Q212=makeQuery(id+"F3.boolean.opBoolean","COPY",EDGE,{"derivedFrom":makeQuery(id+"F3.opExtrude","SWEPT_EDGE",EDGE,{"disambiguationData":[OSD([sQuery(id+"F2.wireOp",EDGE,"E2.6.1.0"),sQuery(id+"F2.wireOp",EDGE,"E2.6.1.2")])]})});
            var Q213;
            Q213=makeQuery(id+"F3.boolean.opBoolean","COPY",EDGE,{"derivedFrom":makeQuery(id+"F3.opExtrude","CAP_EDGE",EDGE,{"disambiguationData":[OSD([sQuery(id+"F2.wireOp",EDGE,"E2.2.2.0")])],"isStart":true})});
            var Q214;
            Q214=makeQuery(id+"F3.boolean.opBoolean","COPY",EDGE,{"derivedFrom":makeQuery(id+"F3.opExtrude","CAP_EDGE",EDGE,{"disambiguationData":[OSD([sQuery(id+"F2.wireOp",EDGE,"E2.1.3.0")])],"isStart":true})});
            var Q215;
            Q215=makeQuery(id+"F3.boolean.opBoolean","COPY",EDGE,{"derivedFrom":makeQuery(id+"F3.opExtrude","CAP_EDGE",EDGE,{"disambiguationData":[OSD([sQuery(id+"F2.wireOp",EDGE,"E2.6.2.0")])],"isStart":true})});
            var Q216;
            Q216=makeQuery(id+"F3.boolean.opBoolean","COPY",EDGE,{"derivedFrom":makeQuery(id+"F3.opExtrude","CAP_EDGE",EDGE,{"disambiguationData":[OSD([sQuery(id+"F2.wireOp",EDGE,"E2.5.3.0")])],"isStart":true})});
            var Q217;
            Q217=makeQuery(id+"F3.boolean.opBoolean","INTERSECT",EDGE,{"derivedFrom":[makeQuery(id+"F1.opExtrude","CAP_FACE",FACE,{"disambiguationData":[OSD([sQuery(id+"F0.wireOp",EDGE,"E0.rect.bottom"),sQuery(id+"F0.wireOp",EDGE,"E0.rect.top"),sQuery(id+"F0.wireOp",EDGE,"E0.rect.left"),sQuery(id+"F0.wireOp",EDGE,"E0.rect.right")])],"isStart":true}),makeQuery(id+"F3.opExtrude","SWEPT_FACE",FACE,{"disambiguationData":[OSD([sQuery(id+"F2.wireOp",EDGE,"E2.2.3.0")])]})]});
            var Q218;
            Q218=makeQuery(id+"F3.boolean.opBoolean","INTERSECT",EDGE,{"derivedFrom":[makeQuery(id+"F1.opExtrude","CAP_FACE",FACE,{"disambiguationData":[OSD([sQuery(id+"F0.wireOp",EDGE,"E0.rect.bottom"),sQuery(id+"F0.wireOp",EDGE,"E0.rect.top"),sQuery(id+"F0.wireOp",EDGE,"E0.rect.left"),sQuery(id+"F0.wireOp",EDGE,"E0.rect.right")])],"isStart":true}),makeQuery(id+"F3.opExtrude","SWEPT_FACE",FACE,{"disambiguationData":[OSD([sQuery(id+"F2.wireOp",EDGE,"E2.1.4.0")])]})]});
            var Q219;
            Q219=makeQuery(id+"F3.boolean.opBoolean","INTERSECT",EDGE,{"derivedFrom":[makeQuery(id+"F1.opExtrude","CAP_FACE",FACE,{"disambiguationData":[OSD([sQuery(id+"F0.wireOp",EDGE,"E0.rect.bottom"),sQuery(id+"F0.wireOp",EDGE,"E0.rect.top"),sQuery(id+"F0.wireOp",EDGE,"E0.rect.left"),sQuery(id+"F0.wireOp",EDGE,"E0.rect.right")])],"isStart":true}),makeQuery(id+"F3.opExtrude","SWEPT_FACE",FACE,{"disambiguationData":[OSD([sQuery(id+"F2.wireOp",EDGE,"E2.6.3.0")])]})]});
            var Q220;
            Q220=makeQuery(id+"F3.boolean.opBoolean","INTERSECT",EDGE,{"derivedFrom":[makeQuery(id+"F1.opExtrude","CAP_FACE",FACE,{"disambiguationData":[OSD([sQuery(id+"F0.wireOp",EDGE,"E0.rect.bottom"),sQuery(id+"F0.wireOp",EDGE,"E0.rect.top"),sQuery(id+"F0.wireOp",EDGE,"E0.rect.left"),sQuery(id+"F0.wireOp",EDGE,"E0.rect.right")])],"isStart":true}),makeQuery(id+"F3.opExtrude","SWEPT_FACE",FACE,{"disambiguationData":[OSD([sQuery(id+"F2.wireOp",EDGE,"E2.5.4.0")])]})]});
            var Q221;
            Q221=makeQuery(id+"F3.boolean.opBoolean","INTERSECT",EDGE,{"derivedFrom":[makeQuery(id+"F1.opExtrude","CAP_FACE",FACE,{"disambiguationData":[OSD([sQuery(id+"F0.wireOp",EDGE,"E0.rect.bottom"),sQuery(id+"F0.wireOp",EDGE,"E0.rect.top"),sQuery(id+"F0.wireOp",EDGE,"E0.rect.left"),sQuery(id+"F0.wireOp",EDGE,"E0.rect.right")])],"isStart":true}),makeQuery(id+"F3.opExtrude","SWEPT_FACE",FACE,{"disambiguationData":[OSD([sQuery(id+"F2.wireOp",EDGE,"E2.5.0.0")])]})]});
            var Q222;
            Q222=makeQuery(id+"F3.boolean.opBoolean","COPY",FACE,{"derivedFrom":makeQuery(id+"F3.opExtrude","SWEPT_FACE",FACE,{"disambiguationData":[OSD([sQuery(id+"F2.wireOp",EDGE,"E2.2.1.0")])]})});
            var Q223;
            Q223=makeQuery(id+"F3.boolean.opBoolean","COPY",FACE,{"derivedFrom":makeQuery(id+"F3.opExtrude","SWEPT_FACE",FACE,{"disambiguationData":[OSD([sQuery(id+"F2.wireOp",EDGE,"E2.5.2.0")])]})});
            var Q224;
            Q224=makeQuery(id+"F3.boolean.opBoolean","COPY",FACE,{"derivedFrom":makeQuery(id+"F3.opExtrude","SWEPT_FACE",FACE,{"disambiguationData":[OSD([sQuery(id+"F2.wireOp",EDGE,"E2.1.2.0")])]})});
            var Q225;
            Q225=makeQuery(id+"F3.boolean.opBoolean","COPY",FACE,{"derivedFrom":makeQuery(id+"F3.opExtrude","SWEPT_FACE",FACE,{"disambiguationData":[OSD([sQuery(id+"F2.wireOp",EDGE,"E2.3.0.0")])]})});
            var Q226;
            Q226=makeQuery(id+"F3.boolean.opBoolean","COPY",FACE,{"derivedFrom":makeQuery(id+"F3.opExtrude","SWEPT_FACE",FACE,{"disambiguationData":[OSD([sQuery(id+"F2.wireOp",EDGE,"E2.3.0.3")])]})});
            var Q227;
            Q227=makeQuery(id+"F3.boolean.opBoolean","COPY",FACE,{"derivedFrom":makeQuery(id+"F3.opExtrude","SWEPT_FACE",FACE,{"disambiguationData":[OSD([sQuery(id+"F2.wireOp",EDGE,"E2.2.1.3")])]})});
            var Q228;
            Q228=makeQuery(id+"F3.boolean.opBoolean","COPY",FACE,{"derivedFrom":makeQuery(id+"F3.opExtrude","SWEPT_FACE",FACE,{"disambiguationData":[OSD([sQuery(id+"F2.wireOp",EDGE,"E2.1.2.3")])]})});
            var Q229;
            Q229=makeQuery(id+"F3.boolean.opBoolean","COPY",FACE,{"derivedFrom":makeQuery(id+"F3.opExtrude","SWEPT_FACE",FACE,{"disambiguationData":[OSD([sQuery(id+"F2.wireOp",EDGE,"E2.5.2.3")])]})});
            var Q230;
            Q230=makeQuery(id+"F3.boolean.opBoolean","INTERSECT",EDGE,{"derivedFrom":[makeQuery(id+"F1.opExtrude","CAP_FACE",FACE,{"disambiguationData":[OSD([sQuery(id+"F0.wireOp",EDGE,"E0.rect.bottom"),sQuery(id+"F0.wireOp",EDGE,"E0.rect.top"),sQuery(id+"F0.wireOp",EDGE,"E0.rect.left"),sQuery(id+"F0.wireOp",EDGE,"E0.rect.right")])],"isStart":true}),makeQuery(id+"F3.opExtrude","SWEPT_FACE",FACE,{"disambiguationData":[OSD([sQuery(id+"F2.wireOp",EDGE,"E2.1.0.1")])]})]});
            var Q231;
            Q231=makeQuery(id+"F3.boolean.opBoolean","INTERSECT",EDGE,{"derivedFrom":[makeQuery(id+"F1.opExtrude","CAP_FACE",FACE,{"disambiguationData":[OSD([sQuery(id+"F0.wireOp",EDGE,"E0.rect.bottom"),sQuery(id+"F0.wireOp",EDGE,"E0.rect.top"),sQuery(id+"F0.wireOp",EDGE,"E0.rect.left"),sQuery(id+"F0.wireOp",EDGE,"E0.rect.right")])],"isStart":true}),makeQuery(id+"F3.opExtrude","SWEPT_FACE",FACE,{"disambiguationData":[OSD([sQuery(id+"F2.wireOp",EDGE,"E2.0.1.1")])]})]});
            var Q232;
            Q232=makeQuery(id+"F3.boolean.opBoolean","INTERSECT",EDGE,{"derivedFrom":[makeQuery(id+"F1.opExtrude","CAP_FACE",FACE,{"disambiguationData":[OSD([sQuery(id+"F0.wireOp",EDGE,"E0.rect.bottom"),sQuery(id+"F0.wireOp",EDGE,"E0.rect.top"),sQuery(id+"F0.wireOp",EDGE,"E0.rect.left"),sQuery(id+"F0.wireOp",EDGE,"E0.rect.right")])],"isStart":true}),makeQuery(id+"F3.opExtrude","SWEPT_FACE",FACE,{"disambiguationData":[OSD([sQuery(id+"F2.wireOp",EDGE,"E2.4.1.1")])]})]});
            var Q233;
            Q233=makeQuery(id+"F3.boolean.opBoolean","INTERSECT",EDGE,{"derivedFrom":[makeQuery(id+"F1.opExtrude","CAP_FACE",FACE,{"disambiguationData":[OSD([sQuery(id+"F0.wireOp",EDGE,"E0.rect.bottom"),sQuery(id+"F0.wireOp",EDGE,"E0.rect.top"),sQuery(id+"F0.wireOp",EDGE,"E0.rect.left"),sQuery(id+"F0.wireOp",EDGE,"E0.rect.right")])],"isStart":true}),makeQuery(id+"F3.opExtrude","SWEPT_FACE",FACE,{"disambiguationData":[OSD([sQuery(id+"F2.wireOp",EDGE,"E2.3.2.1")])]})]});
            var Q234;
            Q234=makeQuery(id+"F3.boolean.opBoolean","INTERSECT",EDGE,{"derivedFrom":[makeQuery(id+"F1.opExtrude","CAP_FACE",FACE,{"disambiguationData":[OSD([sQuery(id+"F0.wireOp",EDGE,"E0.rect.bottom"),sQuery(id+"F0.wireOp",EDGE,"E0.rect.top"),sQuery(id+"F0.wireOp",EDGE,"E0.rect.left"),sQuery(id+"F0.wireOp",EDGE,"E0.rect.right")])],"isStart":true}),makeQuery(id+"F3.opExtrude","SWEPT_FACE",FACE,{"disambiguationData":[OSD([sQuery(id+"F2.wireOp",EDGE,"E2.2.3.1")])]})]});
            var Q235;
            Q235=makeQuery(id+"F3.boolean.opBoolean","INTERSECT",EDGE,{"derivedFrom":[makeQuery(id+"F1.opExtrude","CAP_FACE",FACE,{"disambiguationData":[OSD([sQuery(id+"F0.wireOp",EDGE,"E0.rect.bottom"),sQuery(id+"F0.wireOp",EDGE,"E0.rect.top"),sQuery(id+"F0.wireOp",EDGE,"E0.rect.left"),sQuery(id+"F0.wireOp",EDGE,"E0.rect.right")])],"isStart":true}),makeQuery(id+"F3.opExtrude","SWEPT_FACE",FACE,{"disambiguationData":[OSD([sQuery(id+"F2.wireOp",EDGE,"E2.1.4.1")])]})]});
            var Q236;
            Q236=makeQuery(id+"F3.boolean.opBoolean","INTERSECT",EDGE,{"derivedFrom":[makeQuery(id+"F1.opExtrude","CAP_FACE",FACE,{"disambiguationData":[OSD([sQuery(id+"F0.wireOp",EDGE,"E0.rect.bottom"),sQuery(id+"F0.wireOp",EDGE,"E0.rect.top"),sQuery(id+"F0.wireOp",EDGE,"E0.rect.left"),sQuery(id+"F0.wireOp",EDGE,"E0.rect.right")])],"isStart":true}),makeQuery(id+"F3.opExtrude","SWEPT_FACE",FACE,{"disambiguationData":[OSD([sQuery(id+"F2.wireOp",EDGE,"E2.6.3.1")])]})]});
            var Q237;
            Q237=makeQuery(id+"F3.boolean.opBoolean","INTERSECT",EDGE,{"derivedFrom":[makeQuery(id+"F1.opExtrude","CAP_FACE",FACE,{"disambiguationData":[OSD([sQuery(id+"F0.wireOp",EDGE,"E0.rect.bottom"),sQuery(id+"F0.wireOp",EDGE,"E0.rect.top"),sQuery(id+"F0.wireOp",EDGE,"E0.rect.left"),sQuery(id+"F0.wireOp",EDGE,"E0.rect.right")])],"isStart":true}),makeQuery(id+"F3.opExtrude","SWEPT_FACE",FACE,{"disambiguationData":[OSD([sQuery(id+"F2.wireOp",EDGE,"E2.5.4.1")])]})]});
            var Q238;
            Q238=makeQuery(id+"F3.boolean.opBoolean","INTERSECT",EDGE,{"derivedFrom":[makeQuery(id+"F1.opExtrude","CAP_FACE",FACE,{"disambiguationData":[OSD([sQuery(id+"F0.wireOp",EDGE,"E0.rect.bottom"),sQuery(id+"F0.wireOp",EDGE,"E0.rect.top"),sQuery(id+"F0.wireOp",EDGE,"E0.rect.left"),sQuery(id+"F0.wireOp",EDGE,"E0.rect.right")])],"isStart":true}),makeQuery(id+"F3.opExtrude","SWEPT_FACE",FACE,{"disambiguationData":[OSD([sQuery(id+"F2.wireOp",EDGE,"E2.5.0.1")])]})]});
            var Q239;
            Q239=makeQuery(id+"F3.boolean.opBoolean","COPY",FACE,{"derivedFrom":makeQuery(id+"F3.opExtrude","SWEPT_FACE",FACE,{"disambiguationData":[OSD([sQuery(id+"F2.wireOp",EDGE,"E2.3.0.1")])]})});
            var Q240;
            Q240=makeQuery(id+"F3.boolean.opBoolean","COPY",FACE,{"derivedFrom":makeQuery(id+"F3.opExtrude","SWEPT_FACE",FACE,{"disambiguationData":[OSD([sQuery(id+"F2.wireOp",EDGE,"E2.2.1.1")])]})});
            var Q241;
            Q241=makeQuery(id+"F3.boolean.opBoolean","COPY",FACE,{"derivedFrom":makeQuery(id+"F3.opExtrude","SWEPT_FACE",FACE,{"disambiguationData":[OSD([sQuery(id+"F2.wireOp",EDGE,"E2.5.2.1")])]})});
            var Q242;
            Q242=makeQuery(id+"F3.boolean.opBoolean","COPY",FACE,{"derivedFrom":makeQuery(id+"F3.opExtrude","SWEPT_FACE",FACE,{"disambiguationData":[OSD([sQuery(id+"F2.wireOp",EDGE,"E2.4.3.1")])]})});
            var Q243;
            Q243=makeQuery(id+"F3.boolean.opBoolean","COPY",FACE,{"derivedFrom":makeQuery(id+"F3.opExtrude","SWEPT_FACE",FACE,{"disambiguationData":[OSD([sQuery(id+"F2.wireOp",EDGE,"E2.3.4.1")])]})});
            var Q244;
            Q244=makeQuery(id+"F3.boolean.opBoolean","COPY",EDGE,{"derivedFrom":makeQuery(id+"F3.opExtrude","SWEPT_EDGE",EDGE,{"disambiguationData":[OSD([sQuery(id+"F2.wireOp",EDGE,"E2.2.1.0"),sQuery(id+"F2.wireOp",EDGE,"E2.2.1.3")])]})});
            var Q245;
            Q245=makeQuery(id+"F3.boolean.opBoolean","COPY",EDGE,{"derivedFrom":makeQuery(id+"F3.opExtrude","SWEPT_EDGE",EDGE,{"disambiguationData":[OSD([sQuery(id+"F2.wireOp",EDGE,"E2.1.2.0"),sQuery(id+"F2.wireOp",EDGE,"E2.1.2.3")])]})});
            var Q246;
            Q246=makeQuery(id+"F3.boolean.opBoolean","COPY",EDGE,{"derivedFrom":makeQuery(id+"F3.opExtrude","SWEPT_EDGE",EDGE,{"disambiguationData":[OSD([sQuery(id+"F2.wireOp",EDGE,"E2.5.2.0"),sQuery(id+"F2.wireOp",EDGE,"E2.5.2.3")])]})});
            var Q247;
            Q247=makeQuery(id+"F3.boolean.opBoolean","COPY",EDGE,{"derivedFrom":makeQuery(id+"F3.opExtrude","SWEPT_EDGE",EDGE,{"disambiguationData":[OSD([sQuery(id+"F2.wireOp",EDGE,"E2.4.3.0"),sQuery(id+"F2.wireOp",EDGE,"E2.4.3.3")])]})});
            var Q248;
            Q248=makeQuery(id+"F3.boolean.opBoolean","COPY",EDGE,{"derivedFrom":makeQuery(id+"F3.opExtrude","SWEPT_EDGE",EDGE,{"disambiguationData":[OSD([sQuery(id+"F2.wireOp",EDGE,"E2.3.4.0"),sQuery(id+"F2.wireOp",EDGE,"E2.3.4.3")])]})});
            var Q249;
            Q249=makeQuery(id+"F3.boolean.opBoolean","COPY",EDGE,{"derivedFrom":makeQuery(id+"F3.opExtrude","SWEPT_EDGE",EDGE,{"disambiguationData":[OSD([sQuery(id+"F2.wireOp",EDGE,"E2.3.0.0"),sQuery(id+"F2.wireOp",EDGE,"E2.3.0.3")])]})});
            var Q250;
            Q250=makeQuery(id+"F3.boolean.opBoolean","COPY",EDGE,{"derivedFrom":makeQuery(id+"F3.opExtrude","CAP_EDGE",EDGE,{"disambiguationData":[OSD([sQuery(id+"F2.wireOp",EDGE,"E1.top")])],"isStart":true})});
            var Q251;
            Q251=makeQuery(id+"F3.boolean.opBoolean","COPY",EDGE,{"derivedFrom":makeQuery(id+"F3.opExtrude","SWEPT_EDGE",EDGE,{"disambiguationData":[OSD([sQuery(id+"F2.wireOp",EDGE,"E2.6.1.0"),sQuery(id+"F2.wireOp",EDGE,"E2.6.1.3")])]})});
            var Q252;
            Q252=makeQuery(id+"F3.boolean.opBoolean","COPY",EDGE,{"derivedFrom":makeQuery(id+"F3.opExtrude","CAP_EDGE",EDGE,{"disambiguationData":[OSD([sQuery(id+"F2.wireOp",EDGE,"E2.4.0.1")])],"isStart":true})});
            var Q253;
            Q253=makeQuery(id+"F3.boolean.opBoolean","COPY",EDGE,{"derivedFrom":makeQuery(id+"F3.opExtrude","CAP_EDGE",EDGE,{"disambiguationData":[OSD([sQuery(id+"F2.wireOp",EDGE,"E2.3.1.1")])],"isStart":true})});
            var Q254;
            Q254=makeQuery(id+"F3.boolean.opBoolean","COPY",FACE,{"derivedFrom":makeQuery(id+"F3.opExtrude","SWEPT_FACE",FACE,{"disambiguationData":[OSD([sQuery(id+"F2.wireOp",EDGE,"E2.4.1.3")])]})});
            var Q255;
            Q255=makeQuery(id+"F3.boolean.opBoolean","COPY",FACE,{"derivedFrom":makeQuery(id+"F3.opExtrude","SWEPT_FACE",FACE,{"disambiguationData":[OSD([sQuery(id+"F2.wireOp",EDGE,"E2.3.2.3")])]})});
            var Q256;
            Q256=makeQuery(id+"F3.boolean.opBoolean","INTERSECT",EDGE,{"derivedFrom":[makeQuery(id+"F1.opExtrude","CAP_FACE",FACE,{"disambiguationData":[OSD([sQuery(id+"F0.wireOp",EDGE,"E0.rect.bottom"),sQuery(id+"F0.wireOp",EDGE,"E0.rect.top"),sQuery(id+"F0.wireOp",EDGE,"E0.rect.left"),sQuery(id+"F0.wireOp",EDGE,"E0.rect.right")])],"isStart":true}),makeQuery(id+"F3.opExtrude","SWEPT_FACE",FACE,{"disambiguationData":[OSD([sQuery(id+"F2.wireOp",EDGE,"E2.6.3.2")])]})]});
            var Q257;
            Q257=makeQuery(id+"F3.boolean.opBoolean","INTERSECT",EDGE,{"derivedFrom":[makeQuery(id+"F1.opExtrude","CAP_FACE",FACE,{"disambiguationData":[OSD([sQuery(id+"F0.wireOp",EDGE,"E0.rect.bottom"),sQuery(id+"F0.wireOp",EDGE,"E0.rect.top"),sQuery(id+"F0.wireOp",EDGE,"E0.rect.left"),sQuery(id+"F0.wireOp",EDGE,"E0.rect.right")])],"isStart":true}),makeQuery(id+"F3.opExtrude","SWEPT_FACE",FACE,{"disambiguationData":[OSD([sQuery(id+"F2.wireOp",EDGE,"E2.5.0.2")])]})]});
            var Q258;
            Q258=makeQuery(id+"F3.boolean.opBoolean","COPY",FACE,{"derivedFrom":makeQuery(id+"F3.opExtrude","SWEPT_FACE",FACE,{"disambiguationData":[OSD([sQuery(id+"F2.wireOp",EDGE,"E2.3.0.2")])]})});
            var Q259;
            Q259=makeQuery(id+"F3.boolean.opBoolean","COPY",FACE,{"derivedFrom":makeQuery(id+"F3.opExtrude","SWEPT_FACE",FACE,{"disambiguationData":[OSD([sQuery(id+"F2.wireOp",EDGE,"E2.2.1.2")])]})});
            var Q260;
            Q260=makeQuery(id+"F3.boolean.opBoolean","COPY",FACE,{"derivedFrom":makeQuery(id+"F3.opExtrude","SWEPT_FACE",FACE,{"disambiguationData":[OSD([sQuery(id+"F2.wireOp",EDGE,"E2.1.2.2")])]})});
            var Q261;
            Q261=makeQuery(id+"F3.boolean.opBoolean","COPY",FACE,{"derivedFrom":makeQuery(id+"F3.opExtrude","SWEPT_FACE",FACE,{"disambiguationData":[OSD([sQuery(id+"F2.wireOp",EDGE,"E2.5.2.2")])]})});
            var Q262;
            Q262=makeQuery(id+"F3.boolean.opBoolean","COPY",FACE,{"derivedFrom":makeQuery(id+"F3.opExtrude","SWEPT_FACE",FACE,{"disambiguationData":[OSD([sQuery(id+"F2.wireOp",EDGE,"E2.4.3.2")])]})});
            var Q263;
            Q263=makeQuery(id+"F3.boolean.opBoolean","COPY",EDGE,{"derivedFrom":makeQuery(id+"F3.opExtrude","SWEPT_EDGE",EDGE,{"disambiguationData":[OSD([sQuery(id+"F2.wireOp",EDGE,"E2.6.3.1"),sQuery(id+"F2.wireOp",EDGE,"E2.6.3.3")])]})});
            var Q264;
            Q264=makeQuery(id+"F3.boolean.opBoolean","COPY",EDGE,{"derivedFrom":makeQuery(id+"F3.opExtrude","SWEPT_EDGE",EDGE,{"disambiguationData":[OSD([sQuery(id+"F2.wireOp",EDGE,"E2.5.0.1"),sQuery(id+"F2.wireOp",EDGE,"E2.5.0.3")])]})});
            var Q265;
            Q265=makeQuery(id+"F3.boolean.opBoolean","COPY",EDGE,{"derivedFrom":makeQuery(id+"F3.opExtrude","CAP_EDGE",EDGE,{"disambiguationData":[OSD([sQuery(id+"F2.wireOp",EDGE,"E2.2.0.3")])],"isStart":true})});
            var Q266;
            Q266=makeQuery(id+"F3.boolean.opBoolean","COPY",EDGE,{"derivedFrom":makeQuery(id+"F3.opExtrude","CAP_EDGE",EDGE,{"disambiguationData":[OSD([sQuery(id+"F2.wireOp",EDGE,"E2.1.1.3")])],"isStart":true})});
            var Q267;
            Q267=makeQuery(id+"F3.boolean.opBoolean","COPY",EDGE,{"derivedFrom":makeQuery(id+"F3.opExtrude","CAP_EDGE",EDGE,{"disambiguationData":[OSD([sQuery(id+"F2.wireOp",EDGE,"E2.6.4.3")])],"isStart":true})});
            var Q268;
            Q268=makeQuery(id+"F3.boolean.opBoolean","COPY",EDGE,{"derivedFrom":makeQuery(id+"F3.opExtrude","CAP_EDGE",EDGE,{"disambiguationData":[OSD([sQuery(id+"F2.wireOp",EDGE,"E2.6.0.3")])],"isStart":true})});
            var Q269;
            Q269=makeQuery(id+"F3.boolean.opBoolean","COPY",EDGE,{"derivedFrom":makeQuery(id+"F3.opExtrude","CAP_EDGE",EDGE,{"disambiguationData":[OSD([sQuery(id+"F2.wireOp",EDGE,"E2.5.1.3")])],"isStart":true})});
            var Q270;
            Q270=makeQuery(id+"F3.boolean.opBoolean","COPY",EDGE,{"derivedFrom":makeQuery(id+"F3.opExtrude","CAP_EDGE",EDGE,{"disambiguationData":[OSD([sQuery(id+"F2.wireOp",EDGE,"E2.4.2.3")])],"isStart":true})});
            var Q271;
            Q271=makeQuery(id+"F3.boolean.opBoolean","INTERSECT",EDGE,{"derivedFrom":[makeQuery(id+"F1.opExtrude","CAP_FACE",FACE,{"disambiguationData":[OSD([sQuery(id+"F0.wireOp",EDGE,"E0.rect.bottom"),sQuery(id+"F0.wireOp",EDGE,"E0.rect.top"),sQuery(id+"F0.wireOp",EDGE,"E0.rect.left"),sQuery(id+"F0.wireOp",EDGE,"E0.rect.right")])],"isStart":true}),makeQuery(id+"F3.opExtrude","SWEPT_FACE",FACE,{"disambiguationData":[OSD([sQuery(id+"F2.wireOp",EDGE,"E2.0.3.3")])]})]});
            var Q272;
            Q272=makeQuery(id+"F3.boolean.opBoolean","INTERSECT",EDGE,{"derivedFrom":[makeQuery(id+"F1.opExtrude","CAP_FACE",FACE,{"disambiguationData":[OSD([sQuery(id+"F0.wireOp",EDGE,"E0.rect.bottom"),sQuery(id+"F0.wireOp",EDGE,"E0.rect.top"),sQuery(id+"F0.wireOp",EDGE,"E0.rect.left"),sQuery(id+"F0.wireOp",EDGE,"E0.rect.right")])],"isStart":true}),makeQuery(id+"F3.opExtrude","SWEPT_FACE",FACE,{"disambiguationData":[OSD([sQuery(id+"F2.wireOp",EDGE,"E2.6.1.3")])]})]});
            var Q273;
            Q273=makeQuery(id+"F3.boolean.opBoolean","COPY",EDGE,{"derivedFrom":makeQuery(id+"F3.opExtrude","CAP_EDGE",EDGE,{"disambiguationData":[OSD([sQuery(id+"F2.wireOp",EDGE,"E1.left")])],"isStart":true})});
            var Q274;
            Q274=makeQuery(id+"F3.boolean.opBoolean","COPY",EDGE,{"derivedFrom":makeQuery(id+"F3.opExtrude","SWEPT_EDGE",EDGE,{"disambiguationData":[OSD([sQuery(id+"F2.wireOp",EDGE,"E2.6.1.1"),sQuery(id+"F2.wireOp",EDGE,"E2.6.1.2")])]})});
            var Q275;
            Q275=makeQuery(id+"F3.boolean.opBoolean","COPY",EDGE,{"derivedFrom":makeQuery(id+"F3.opExtrude","CAP_EDGE",EDGE,{"disambiguationData":[OSD([sQuery(id+"F2.wireOp",EDGE,"E2.4.0.2")])],"isStart":true})});
            var Q276;
            Q276=makeQuery(id+"F3.boolean.opBoolean","COPY",EDGE,{"derivedFrom":makeQuery(id+"F3.opExtrude","CAP_EDGE",EDGE,{"disambiguationData":[OSD([sQuery(id+"F2.wireOp",EDGE,"E2.3.1.2")])],"isStart":true})});
            var Q277;
            Q277=makeQuery(id+"F3.boolean.opBoolean","COPY",EDGE,{"derivedFrom":makeQuery(id+"F3.opExtrude","CAP_EDGE",EDGE,{"disambiguationData":[OSD([sQuery(id+"F2.wireOp",EDGE,"E2.2.2.2")])],"isStart":true})});
            var Q278;
            Q278=makeQuery(id+"F3.boolean.opBoolean","COPY",EDGE,{"derivedFrom":makeQuery(id+"F3.opExtrude","CAP_EDGE",EDGE,{"disambiguationData":[OSD([sQuery(id+"F2.wireOp",EDGE,"E2.6.2.2")])],"isStart":true})});
            var Q279;
            Q279=makeQuery(id+"F3.boolean.opBoolean","INTERSECT",EDGE,{"derivedFrom":[makeQuery(id+"F1.opExtrude","CAP_FACE",FACE,{"disambiguationData":[OSD([sQuery(id+"F0.wireOp",EDGE,"E0.rect.bottom"),sQuery(id+"F0.wireOp",EDGE,"E0.rect.top"),sQuery(id+"F0.wireOp",EDGE,"E0.rect.left"),sQuery(id+"F0.wireOp",EDGE,"E0.rect.right")])],"isStart":true}),makeQuery(id+"F3.opExtrude","SWEPT_FACE",FACE,{"disambiguationData":[OSD([sQuery(id+"F2.wireOp",EDGE,"E2.5.2.3")])]})]});
            var Q280;
            Q280=makeQuery(id+"F3.boolean.opBoolean","INTERSECT",EDGE,{"derivedFrom":[makeQuery(id+"F1.opExtrude","CAP_FACE",FACE,{"disambiguationData":[OSD([sQuery(id+"F0.wireOp",EDGE,"E0.rect.bottom"),sQuery(id+"F0.wireOp",EDGE,"E0.rect.top"),sQuery(id+"F0.wireOp",EDGE,"E0.rect.left"),sQuery(id+"F0.wireOp",EDGE,"E0.rect.right")])],"isStart":true}),makeQuery(id+"F3.opExtrude","SWEPT_FACE",FACE,{"disambiguationData":[OSD([sQuery(id+"F2.wireOp",EDGE,"E2.4.3.3")])]})]});
            var Q281;
            Q281=makeQuery(id+"F3.boolean.opBoolean","INTERSECT",EDGE,{"derivedFrom":[makeQuery(id+"F1.opExtrude","CAP_FACE",FACE,{"disambiguationData":[OSD([sQuery(id+"F0.wireOp",EDGE,"E0.rect.bottom"),sQuery(id+"F0.wireOp",EDGE,"E0.rect.top"),sQuery(id+"F0.wireOp",EDGE,"E0.rect.left"),sQuery(id+"F0.wireOp",EDGE,"E0.rect.right")])],"isStart":true}),makeQuery(id+"F3.opExtrude","SWEPT_FACE",FACE,{"disambiguationData":[OSD([sQuery(id+"F2.wireOp",EDGE,"E2.3.4.3")])]})]});
            var Q282;
            Q282=makeQuery(id+"F3.boolean.opBoolean","COPY",FACE,{"derivedFrom":makeQuery(id+"F3.opExtrude","SWEPT_FACE",FACE,{"disambiguationData":[OSD([sQuery(id+"F2.wireOp",EDGE,"E2.1.0.3")])]})});
            var Q283;
            Q283=makeQuery(id+"F3.boolean.opBoolean","COPY",EDGE,{"derivedFrom":makeQuery(id+"F3.opExtrude","SWEPT_EDGE",EDGE,{"disambiguationData":[OSD([sQuery(id+"F2.wireOp",EDGE,"E2.3.3.0"),sQuery(id+"F2.wireOp",EDGE,"E2.3.3.2")])]})});
            var Q284;
            Q284=makeQuery(id+"F3.boolean.opBoolean","COPY",EDGE,{"derivedFrom":makeQuery(id+"F3.opExtrude","SWEPT_EDGE",EDGE,{"disambiguationData":[OSD([sQuery(id+"F2.wireOp",EDGE,"E2.2.4.0"),sQuery(id+"F2.wireOp",EDGE,"E2.2.4.2")])]})});
            var Q285;
            Q285=makeQuery(id+"F3.boolean.opBoolean","INTERSECT",EDGE,{"derivedFrom":[makeQuery(id+"F1.opExtrude","CAP_FACE",FACE,{"disambiguationData":[OSD([sQuery(id+"F0.wireOp",EDGE,"E0.rect.bottom"),sQuery(id+"F0.wireOp",EDGE,"E0.rect.top"),sQuery(id+"F0.wireOp",EDGE,"E0.rect.left"),sQuery(id+"F0.wireOp",EDGE,"E0.rect.right")])],"isStart":true}),makeQuery(id+"F3.opExtrude","SWEPT_FACE",FACE,{"disambiguationData":[OSD([sQuery(id+"F2.wireOp",EDGE,"E2.6.3.3")])]})]});
            var Q286;
            Q286=makeQuery(id+"F3.boolean.opBoolean","INTERSECT",EDGE,{"derivedFrom":[makeQuery(id+"F1.opExtrude","CAP_FACE",FACE,{"disambiguationData":[OSD([sQuery(id+"F0.wireOp",EDGE,"E0.rect.bottom"),sQuery(id+"F0.wireOp",EDGE,"E0.rect.top"),sQuery(id+"F0.wireOp",EDGE,"E0.rect.left"),sQuery(id+"F0.wireOp",EDGE,"E0.rect.right")])],"isStart":true}),makeQuery(id+"F3.opExtrude","SWEPT_FACE",FACE,{"disambiguationData":[OSD([sQuery(id+"F2.wireOp",EDGE,"E2.5.4.3")])]})]});
            var Q287;
            Q287=makeQuery(id+"F3.boolean.opBoolean","INTERSECT",EDGE,{"derivedFrom":[makeQuery(id+"F1.opExtrude","CAP_FACE",FACE,{"disambiguationData":[OSD([sQuery(id+"F0.wireOp",EDGE,"E0.rect.bottom"),sQuery(id+"F0.wireOp",EDGE,"E0.rect.top"),sQuery(id+"F0.wireOp",EDGE,"E0.rect.left"),sQuery(id+"F0.wireOp",EDGE,"E0.rect.right")])],"isStart":true}),makeQuery(id+"F3.opExtrude","SWEPT_FACE",FACE,{"disambiguationData":[OSD([sQuery(id+"F2.wireOp",EDGE,"E2.5.0.3")])]})]});
            var Q288;
            Q288=makeQuery(id+"F3.boolean.opBoolean","COPY",EDGE,{"derivedFrom":makeQuery(id+"F3.opExtrude","SWEPT_EDGE",EDGE,{"disambiguationData":[OSD([sQuery(id+"F2.wireOp",EDGE,"E2.1.2.1"),sQuery(id+"F2.wireOp",EDGE,"E2.1.2.3")])]})});
            var Q289;
            Q289=makeQuery(id+"F3.boolean.opBoolean","COPY",EDGE,{"derivedFrom":makeQuery(id+"F3.opExtrude","CAP_EDGE",EDGE,{"disambiguationData":[OSD([sQuery(id+"F2.wireOp",EDGE,"E2.1.3.3")])],"isStart":true})});
            var Q290;
            Q290=makeQuery(id+"F3.boolean.opBoolean","COPY",EDGE,{"derivedFrom":makeQuery(id+"F3.opExtrude","CAP_EDGE",EDGE,{"disambiguationData":[OSD([sQuery(id+"F2.wireOp",EDGE,"E2.0.4.3")])],"isStart":true})});
            var Q291;
            Q291=makeQuery(id+"F3.boolean.opBoolean","COPY",EDGE,{"derivedFrom":makeQuery(id+"F3.opExtrude","SWEPT_EDGE",EDGE,{"disambiguationData":[OSD([sQuery(id+"F2.wireOp",EDGE,"E2.6.1.1"),sQuery(id+"F2.wireOp",EDGE,"E2.6.1.3")])]})});
            var Q292;
            Q292=makeQuery(id+"F3.boolean.opBoolean","COPY",EDGE,{"derivedFrom":makeQuery(id+"F3.opExtrude","CAP_EDGE",EDGE,{"disambiguationData":[OSD([sQuery(id+"F2.wireOp",EDGE,"E2.4.4.3")])],"isStart":true})});
            var Q293;
            Q293=makeQuery(id+"F3.boolean.opBoolean","COPY",EDGE,{"derivedFrom":makeQuery(id+"F3.opExtrude","CAP_EDGE",EDGE,{"disambiguationData":[OSD([sQuery(id+"F2.wireOp",EDGE,"E2.2.2.3")])],"isStart":true})});
            var Q294;
            Q294=makeQuery(id+"F3.boolean.opBoolean","COPY",EDGE,{"derivedFrom":makeQuery(id+"F3.opExtrude","CAP_EDGE",EDGE,{"disambiguationData":[OSD([sQuery(id+"F2.wireOp",EDGE,"E2.6.2.3")])],"isStart":true})});
            var Q295;
            Q295=makeQuery(id+"F3.boolean.opBoolean","INTERSECT",EDGE,{"derivedFrom":[makeQuery(id+"F1.opExtrude","CAP_FACE",FACE,{"disambiguationData":[OSD([sQuery(id+"F0.wireOp",EDGE,"E0.rect.bottom"),sQuery(id+"F0.wireOp",EDGE,"E0.rect.top"),sQuery(id+"F0.wireOp",EDGE,"E0.rect.left"),sQuery(id+"F0.wireOp",EDGE,"E0.rect.right")])],"isStart":true}),makeQuery(id+"F3.opExtrude","SWEPT_FACE",FACE,{"disambiguationData":[OSD([sQuery(id+"F2.wireOp",EDGE,"E2.2.3.3")])]})]});
            var Q296;
            Q296=makeQuery(id+"F3.boolean.opBoolean","INTERSECT",EDGE,{"derivedFrom":[makeQuery(id+"F1.opExtrude","CAP_FACE",FACE,{"disambiguationData":[OSD([sQuery(id+"F0.wireOp",EDGE,"E0.rect.bottom"),sQuery(id+"F0.wireOp",EDGE,"E0.rect.top"),sQuery(id+"F0.wireOp",EDGE,"E0.rect.left"),sQuery(id+"F0.wireOp",EDGE,"E0.rect.right")])],"isStart":true}),makeQuery(id+"F3.opExtrude","SWEPT_FACE",FACE,{"disambiguationData":[OSD([sQuery(id+"F2.wireOp",EDGE,"E2.1.4.3")])]})]});
            var Q297;
            Q297=makeQuery(id+"F3.boolean.opBoolean","COPY",EDGE,{"derivedFrom":makeQuery(id+"F3.opExtrude","SWEPT_EDGE",EDGE,{"disambiguationData":[OSD([sQuery(id+"F2.wireOp",EDGE,"E2.1.3.0"),sQuery(id+"F2.wireOp",EDGE,"E2.1.3.2")])]})});
            var Q298;
            Q298=makeQuery(id+"F3.boolean.opBoolean","COPY",EDGE,{"derivedFrom":makeQuery(id+"F3.opExtrude","SWEPT_EDGE",EDGE,{"disambiguationData":[OSD([sQuery(id+"F2.wireOp",EDGE,"E2.0.4.0"),sQuery(id+"F2.wireOp",EDGE,"E2.0.4.2")])]})});
            var Q299;
            Q299=makeQuery(id+"F3.boolean.opBoolean","COPY",EDGE,{"derivedFrom":makeQuery(id+"F3.opExtrude","SWEPT_EDGE",EDGE,{"disambiguationData":[OSD([sQuery(id+"F2.wireOp",EDGE,"E2.5.3.0"),sQuery(id+"F2.wireOp",EDGE,"E2.5.3.2")])]})});
            var Q300;
            Q300=makeQuery(id+"F3.boolean.opBoolean","COPY",EDGE,{"derivedFrom":makeQuery(id+"F3.opExtrude","SWEPT_EDGE",EDGE,{"disambiguationData":[OSD([sQuery(id+"F2.wireOp",EDGE,"E2.4.4.0"),sQuery(id+"F2.wireOp",EDGE,"E2.4.4.2")])]})});
            var Q301;
            Q301=makeQuery(id+"F3.boolean.opBoolean","COPY",EDGE,{"derivedFrom":makeQuery(id+"F3.opExtrude","CAP_EDGE",EDGE,{"disambiguationData":[OSD([sQuery(id+"F2.wireOp",EDGE,"E2.1.4.0")])],"isStart":true})});
            var Q302;
            Q302=makeQuery(id+"F3.boolean.opBoolean","COPY",EDGE,{"derivedFrom":makeQuery(id+"F3.opExtrude","CAP_EDGE",EDGE,{"disambiguationData":[OSD([sQuery(id+"F2.wireOp",EDGE,"E2.5.0.0")])],"isStart":true})});
            var Q303;
            Q303=makeQuery(id+"F3.boolean.opBoolean","COPY",EDGE,{"derivedFrom":makeQuery(id+"F3.opExtrude","CAP_EDGE",EDGE,{"disambiguationData":[OSD([sQuery(id+"F2.wireOp",EDGE,"E2.2.3.0")])],"isStart":true})});
            var Q304;
            Q304=makeQuery(id+"F3.boolean.opBoolean","COPY",EDGE,{"derivedFrom":makeQuery(id+"F3.opExtrude","CAP_EDGE",EDGE,{"disambiguationData":[OSD([sQuery(id+"F2.wireOp",EDGE,"E2.6.3.0")])],"isStart":true})});
            var Q305;
            Q305=makeQuery(id+"F3.boolean.opBoolean","COPY",EDGE,{"derivedFrom":makeQuery(id+"F3.opExtrude","CAP_EDGE",EDGE,{"disambiguationData":[OSD([sQuery(id+"F2.wireOp",EDGE,"E2.5.4.0")])],"isStart":true})});
            var Q306;
            Q306=makeQuery(id+"F3.boolean.opBoolean","INTERSECT",EDGE,{"derivedFrom":[makeQuery(id+"F1.opExtrude","CAP_FACE",FACE,{"disambiguationData":[OSD([sQuery(id+"F0.wireOp",EDGE,"E0.rect.bottom"),sQuery(id+"F0.wireOp",EDGE,"E0.rect.top"),sQuery(id+"F0.wireOp",EDGE,"E0.rect.left"),sQuery(id+"F0.wireOp",EDGE,"E0.rect.right")])],"isStart":true}),makeQuery(id+"F3.opExtrude","SWEPT_FACE",FACE,{"disambiguationData":[OSD([sQuery(id+"F2.wireOp",EDGE,"E2.2.4.0")])]})]});
            var Q307;
            Q307=makeQuery(id+"F3.boolean.opBoolean","INTERSECT",EDGE,{"derivedFrom":[makeQuery(id+"F1.opExtrude","CAP_FACE",FACE,{"disambiguationData":[OSD([sQuery(id+"F0.wireOp",EDGE,"E0.rect.bottom"),sQuery(id+"F0.wireOp",EDGE,"E0.rect.top"),sQuery(id+"F0.wireOp",EDGE,"E0.rect.left"),sQuery(id+"F0.wireOp",EDGE,"E0.rect.right")])],"isStart":true}),makeQuery(id+"F3.opExtrude","SWEPT_FACE",FACE,{"disambiguationData":[OSD([sQuery(id+"F2.wireOp",EDGE,"E2.6.0.0")])]})]});
            var Q308;
            Q308=makeQuery(id+"F3.boolean.opBoolean","COPY",FACE,{"derivedFrom":makeQuery(id+"F3.opExtrude","SWEPT_FACE",FACE,{"disambiguationData":[OSD([sQuery(id+"F2.wireOp",EDGE,"E2.3.1.0")])]})});
            var Q309;
            Q309=makeQuery(id+"F3.boolean.opBoolean","COPY",FACE,{"derivedFrom":makeQuery(id+"F3.opExtrude","SWEPT_FACE",FACE,{"disambiguationData":[OSD([sQuery(id+"F2.wireOp",EDGE,"E2.2.2.0")])]})});
            var Q310;
            Q310=makeQuery(id+"F3.boolean.opBoolean","INTERSECT",EDGE,{"derivedFrom":[makeQuery(id+"F1.opExtrude","CAP_FACE",FACE,{"disambiguationData":[OSD([sQuery(id+"F0.wireOp",EDGE,"E0.rect.bottom"),sQuery(id+"F0.wireOp",EDGE,"E0.rect.top"),sQuery(id+"F0.wireOp",EDGE,"E0.rect.left"),sQuery(id+"F0.wireOp",EDGE,"E0.rect.right")])],"isStart":true}),makeQuery(id+"F3.opExtrude","SWEPT_FACE",FACE,{"disambiguationData":[OSD([sQuery(id+"F2.wireOp",EDGE,"E2.6.4.0")])]})]});
            var Q311;
            Q311=makeQuery(id+"F3.boolean.opBoolean","COPY",FACE,{"derivedFrom":makeQuery(id+"F3.opExtrude","SWEPT_FACE",FACE,{"disambiguationData":[OSD([sQuery(id+"F2.wireOp",EDGE,"E2.4.0.0")])]})});
            var Q312;
            Q312=makeQuery(id+"F3.boolean.opBoolean","COPY",EDGE,{"derivedFrom":makeQuery(id+"F3.opExtrude","SWEPT_EDGE",EDGE,{"disambiguationData":[OSD([sQuery(id+"F2.wireOp",EDGE,"E2.5.3.0"),sQuery(id+"F2.wireOp",EDGE,"E2.5.3.3")])]})});
            var Q313;
            Q313=makeQuery(id+"F3.boolean.opBoolean","COPY",EDGE,{"derivedFrom":makeQuery(id+"F3.opExtrude","SWEPT_EDGE",EDGE,{"disambiguationData":[OSD([sQuery(id+"F2.wireOp",EDGE,"E2.4.4.0"),sQuery(id+"F2.wireOp",EDGE,"E2.4.4.3")])]})});
            var Q314;
            Q314=makeQuery(id+"F3.boolean.opBoolean","COPY",EDGE,{"derivedFrom":makeQuery(id+"F3.opExtrude","SWEPT_EDGE",EDGE,{"disambiguationData":[OSD([sQuery(id+"F2.wireOp",EDGE,"E2.4.0.0"),sQuery(id+"F2.wireOp",EDGE,"E2.4.0.3")])]})});
            var Q315;
            Q315=makeQuery(id+"F3.boolean.opBoolean","COPY",EDGE,{"derivedFrom":makeQuery(id+"F3.opExtrude","SWEPT_EDGE",EDGE,{"disambiguationData":[OSD([sQuery(id+"F2.wireOp",EDGE,"E2.3.1.0"),sQuery(id+"F2.wireOp",EDGE,"E2.3.1.3")])]})});
            var Q316;
            Q316=makeQuery(id+"F3.boolean.opBoolean","COPY",EDGE,{"derivedFrom":makeQuery(id+"F3.opExtrude","CAP_EDGE",EDGE,{"disambiguationData":[OSD([sQuery(id+"F2.wireOp",EDGE,"E2.1.0.1")])],"isStart":true})});
            var Q317;
            Q317=makeQuery(id+"F3.boolean.opBoolean","COPY",EDGE,{"derivedFrom":makeQuery(id+"F3.opExtrude","CAP_EDGE",EDGE,{"disambiguationData":[OSD([sQuery(id+"F2.wireOp",EDGE,"E2.0.1.1")])],"isStart":true})});
            var Q318;
            Q318=makeQuery(id+"F3.boolean.opBoolean","COPY",EDGE,{"derivedFrom":makeQuery(id+"F3.opExtrude","SWEPT_EDGE",EDGE,{"disambiguationData":[OSD([sQuery(id+"F2.wireOp",EDGE,"E2.6.2.0"),sQuery(id+"F2.wireOp",EDGE,"E2.6.2.3")])]})});
            var Q319;
            Q319=makeQuery(id+"F3.boolean.opBoolean","COPY",EDGE,{"derivedFrom":makeQuery(id+"F3.opExtrude","CAP_EDGE",EDGE,{"disambiguationData":[OSD([sQuery(id+"F2.wireOp",EDGE,"E2.5.0.1")])],"isStart":true})});
            var Q320;
            Q320=makeQuery(id+"F3.boolean.opBoolean","COPY",EDGE,{"derivedFrom":makeQuery(id+"F3.opExtrude","CAP_EDGE",EDGE,{"disambiguationData":[OSD([sQuery(id+"F2.wireOp",EDGE,"E2.4.1.1")])],"isStart":true})});
            var Q321;
            Q321=makeQuery(id+"F3.boolean.opBoolean","INTERSECT",EDGE,{"derivedFrom":[makeQuery(id+"F1.opExtrude","CAP_FACE",FACE,{"disambiguationData":[OSD([sQuery(id+"F0.wireOp",EDGE,"E0.rect.bottom"),sQuery(id+"F0.wireOp",EDGE,"E0.rect.top"),sQuery(id+"F0.wireOp",EDGE,"E0.rect.left"),sQuery(id+"F0.wireOp",EDGE,"E0.rect.right")])],"isStart":true}),makeQuery(id+"F3.opExtrude","SWEPT_FACE",FACE,{"disambiguationData":[OSD([sQuery(id+"F2.wireOp",EDGE,"E2.1.1.1")])]})]});
            var Q322;
            Q322=makeQuery(id+"F3.boolean.opBoolean","INTERSECT",EDGE,{"derivedFrom":[makeQuery(id+"F1.opExtrude","CAP_FACE",FACE,{"disambiguationData":[OSD([sQuery(id+"F0.wireOp",EDGE,"E0.rect.bottom"),sQuery(id+"F0.wireOp",EDGE,"E0.rect.top"),sQuery(id+"F0.wireOp",EDGE,"E0.rect.left"),sQuery(id+"F0.wireOp",EDGE,"E0.rect.right")])],"isStart":true}),makeQuery(id+"F3.opExtrude","SWEPT_FACE",FACE,{"disambiguationData":[OSD([sQuery(id+"F2.wireOp",EDGE,"E2.0.2.1")])]})]});
            var Q323;
            Q323=makeQuery(id+"F3.boolean.opBoolean","INTERSECT",EDGE,{"derivedFrom":[makeQuery(id+"F1.opExtrude","CAP_FACE",FACE,{"disambiguationData":[OSD([sQuery(id+"F0.wireOp",EDGE,"E0.rect.bottom"),sQuery(id+"F0.wireOp",EDGE,"E0.rect.top"),sQuery(id+"F0.wireOp",EDGE,"E0.rect.left"),sQuery(id+"F0.wireOp",EDGE,"E0.rect.right")])],"isStart":true}),makeQuery(id+"F3.opExtrude","SWEPT_FACE",FACE,{"disambiguationData":[OSD([sQuery(id+"F2.wireOp",EDGE,"E2.4.2.1")])]})]});
            var Q324;
            Q324=makeQuery(id+"F3.boolean.opBoolean","INTERSECT",EDGE,{"derivedFrom":[makeQuery(id+"F1.opExtrude","CAP_FACE",FACE,{"disambiguationData":[OSD([sQuery(id+"F0.wireOp",EDGE,"E0.rect.bottom"),sQuery(id+"F0.wireOp",EDGE,"E0.rect.top"),sQuery(id+"F0.wireOp",EDGE,"E0.rect.left"),sQuery(id+"F0.wireOp",EDGE,"E0.rect.right")])],"isStart":true}),makeQuery(id+"F3.opExtrude","SWEPT_FACE",FACE,{"disambiguationData":[OSD([sQuery(id+"F2.wireOp",EDGE,"E2.2.4.1")])]})]});
            var Q325;
            Q325=makeQuery(id+"F3.boolean.opBoolean","INTERSECT",EDGE,{"derivedFrom":[makeQuery(id+"F1.opExtrude","CAP_FACE",FACE,{"disambiguationData":[OSD([sQuery(id+"F0.wireOp",EDGE,"E0.rect.bottom"),sQuery(id+"F0.wireOp",EDGE,"E0.rect.top"),sQuery(id+"F0.wireOp",EDGE,"E0.rect.left"),sQuery(id+"F0.wireOp",EDGE,"E0.rect.right")])],"isStart":true}),makeQuery(id+"F3.opExtrude","SWEPT_FACE",FACE,{"disambiguationData":[OSD([sQuery(id+"F2.wireOp",EDGE,"E2.3.3.1")])]})]});
            var Q326;
            Q326=makeQuery(id+"F3.boolean.opBoolean","INTERSECT",EDGE,{"derivedFrom":[makeQuery(id+"F1.opExtrude","CAP_FACE",FACE,{"disambiguationData":[OSD([sQuery(id+"F0.wireOp",EDGE,"E0.rect.bottom"),sQuery(id+"F0.wireOp",EDGE,"E0.rect.top"),sQuery(id+"F0.wireOp",EDGE,"E0.rect.left"),sQuery(id+"F0.wireOp",EDGE,"E0.rect.right")])],"isStart":true}),makeQuery(id+"F3.opExtrude","SWEPT_FACE",FACE,{"disambiguationData":[OSD([sQuery(id+"F2.wireOp",EDGE,"E2.2.0.1")])]})]});
            var Q327;
            Q327=makeQuery(id+"F3.boolean.opBoolean","INTERSECT",EDGE,{"derivedFrom":[makeQuery(id+"F1.opExtrude","CAP_FACE",FACE,{"disambiguationData":[OSD([sQuery(id+"F0.wireOp",EDGE,"E0.rect.bottom"),sQuery(id+"F0.wireOp",EDGE,"E0.rect.top"),sQuery(id+"F0.wireOp",EDGE,"E0.rect.left"),sQuery(id+"F0.wireOp",EDGE,"E0.rect.right")])],"isStart":true}),makeQuery(id+"F3.opExtrude","SWEPT_FACE",FACE,{"disambiguationData":[OSD([sQuery(id+"F2.wireOp",EDGE,"E2.6.0.1")])]})]});
            var Q328;
            Q328=makeQuery(id+"F3.boolean.opBoolean","INTERSECT",EDGE,{"derivedFrom":[makeQuery(id+"F1.opExtrude","CAP_FACE",FACE,{"disambiguationData":[OSD([sQuery(id+"F0.wireOp",EDGE,"E0.rect.bottom"),sQuery(id+"F0.wireOp",EDGE,"E0.rect.top"),sQuery(id+"F0.wireOp",EDGE,"E0.rect.left"),sQuery(id+"F0.wireOp",EDGE,"E0.rect.right")])],"isStart":true}),makeQuery(id+"F3.opExtrude","SWEPT_FACE",FACE,{"disambiguationData":[OSD([sQuery(id+"F2.wireOp",EDGE,"E2.5.1.1")])]})]});
            var Q329;
            Q329=makeQuery(id+"F3.boolean.opBoolean","COPY",FACE,{"derivedFrom":makeQuery(id+"F3.opExtrude","SWEPT_FACE",FACE,{"disambiguationData":[OSD([sQuery(id+"F2.wireOp",EDGE,"E2.3.1.1")])]})});
            var Q330;
            Q330=makeQuery(id+"F3.boolean.opBoolean","INTERSECT",EDGE,{"derivedFrom":[makeQuery(id+"F1.opExtrude","CAP_FACE",FACE,{"disambiguationData":[OSD([sQuery(id+"F0.wireOp",EDGE,"E0.rect.bottom"),sQuery(id+"F0.wireOp",EDGE,"E0.rect.top"),sQuery(id+"F0.wireOp",EDGE,"E0.rect.left"),sQuery(id+"F0.wireOp",EDGE,"E0.rect.right")])],"isStart":true}),makeQuery(id+"F3.opExtrude","SWEPT_FACE",FACE,{"disambiguationData":[OSD([sQuery(id+"F2.wireOp",EDGE,"E2.6.4.1")])]})]});
            var Q331;
            Q331=makeQuery(id+"F3.boolean.opBoolean","COPY",FACE,{"derivedFrom":makeQuery(id+"F3.opExtrude","SWEPT_FACE",FACE,{"disambiguationData":[OSD([sQuery(id+"F2.wireOp",EDGE,"E2.0.4.1")])]})});
            var Q332;
            Q332=makeQuery(id+"F3.boolean.opBoolean","COPY",EDGE,{"derivedFrom":makeQuery(id+"F3.opExtrude","SWEPT_EDGE",EDGE,{"disambiguationData":[OSD([sQuery(id+"F2.wireOp",EDGE,"E2.2.2.0"),sQuery(id+"F2.wireOp",EDGE,"E2.2.2.3")])]})});
            var Q333;
            Q333=makeQuery(id+"F3.boolean.opBoolean","COPY",EDGE,{"derivedFrom":makeQuery(id+"F3.opExtrude","SWEPT_EDGE",EDGE,{"disambiguationData":[OSD([sQuery(id+"F2.wireOp",EDGE,"E2.1.3.0"),sQuery(id+"F2.wireOp",EDGE,"E2.1.3.3")])]})});
            var Q334;
            Q334=makeQuery(id+"F3.boolean.opBoolean","COPY",EDGE,{"derivedFrom":makeQuery(id+"F3.opExtrude","SWEPT_EDGE",EDGE,{"disambiguationData":[OSD([sQuery(id+"F2.wireOp",EDGE,"E2.0.4.0"),sQuery(id+"F2.wireOp",EDGE,"E2.0.4.3")])]})});
            var Q335;
            Q335=makeQuery(id+"F3.boolean.opBoolean","COPY",FACE,{"derivedFrom":makeQuery(id+"F3.opExtrude","SWEPT_FACE",FACE,{"disambiguationData":[OSD([sQuery(id+"F2.wireOp",EDGE,"E2.5.3.1")])]})});
            var Q336;
            Q336=makeQuery(id+"F3.boolean.opBoolean","COPY",FACE,{"derivedFrom":makeQuery(id+"F3.opExtrude","SWEPT_FACE",FACE,{"disambiguationData":[OSD([sQuery(id+"F2.wireOp",EDGE,"E2.4.4.1")])]})});
            var Q337;
            Q337=makeQuery(id+"F3.boolean.opBoolean","COPY",FACE,{"derivedFrom":makeQuery(id+"F3.opExtrude","SWEPT_FACE",FACE,{"disambiguationData":[OSD([sQuery(id+"F2.wireOp",EDGE,"E2.4.0.1")])]})});
            var Q338;
            Q338=makeQuery(id+"F3.boolean.opBoolean","COPY",EDGE,{"derivedFrom":makeQuery(id+"F3.opExtrude","CAP_EDGE",EDGE,{"disambiguationData":[OSD([sQuery(id+"F2.wireOp",EDGE,"E2.1.0.2")])],"isStart":true})});
            var Q339;
            Q339=makeQuery(id+"F3.boolean.opBoolean","COPY",EDGE,{"derivedFrom":makeQuery(id+"F3.opExtrude","CAP_EDGE",EDGE,{"disambiguationData":[OSD([sQuery(id+"F2.wireOp",EDGE,"E2.0.1.2")])],"isStart":true})});
            var Q340;
            Q340=makeQuery(id+"F3.boolean.opBoolean","COPY",EDGE,{"derivedFrom":makeQuery(id+"F3.opExtrude","CAP_EDGE",EDGE,{"disambiguationData":[OSD([sQuery(id+"F2.wireOp",EDGE,"E2.5.0.2")])],"isStart":true})});
            var Q341;
            Q341=makeQuery(id+"F3.boolean.opBoolean","COPY",EDGE,{"derivedFrom":makeQuery(id+"F3.opExtrude","CAP_EDGE",EDGE,{"disambiguationData":[OSD([sQuery(id+"F2.wireOp",EDGE,"E2.4.1.2")])],"isStart":true})});
            var Q342;
            Q342=makeQuery(id+"F3.boolean.opBoolean","COPY",EDGE,{"derivedFrom":makeQuery(id+"F3.opExtrude","CAP_EDGE",EDGE,{"disambiguationData":[OSD([sQuery(id+"F2.wireOp",EDGE,"E2.3.2.2")])],"isStart":true})});
            var Q343;
            Q343=makeQuery(id+"F3.boolean.opBoolean","INTERSECT",EDGE,{"derivedFrom":[makeQuery(id+"F1.opExtrude","CAP_FACE",FACE,{"disambiguationData":[OSD([sQuery(id+"F0.wireOp",EDGE,"E0.rect.bottom"),sQuery(id+"F0.wireOp",EDGE,"E0.rect.top"),sQuery(id+"F0.wireOp",EDGE,"E0.rect.left"),sQuery(id+"F0.wireOp",EDGE,"E0.rect.right")])],"isStart":true}),makeQuery(id+"F3.opExtrude","SWEPT_FACE",FACE,{"disambiguationData":[OSD([sQuery(id+"F2.wireOp",EDGE,"E2.0.2.2")])]})]});
            var Q344;
            Q344=makeQuery(id+"F3.boolean.opBoolean","INTERSECT",EDGE,{"derivedFrom":[makeQuery(id+"F1.opExtrude","CAP_FACE",FACE,{"disambiguationData":[OSD([sQuery(id+"F0.wireOp",EDGE,"E0.rect.bottom"),sQuery(id+"F0.wireOp",EDGE,"E0.rect.top"),sQuery(id+"F0.wireOp",EDGE,"E0.rect.left"),sQuery(id+"F0.wireOp",EDGE,"E0.rect.right")])],"isStart":true}),makeQuery(id+"F3.opExtrude","SWEPT_FACE",FACE,{"disambiguationData":[OSD([sQuery(id+"F2.wireOp",EDGE,"E2.2.4.2")])]})]});
            var Q345;
            Q345=makeQuery(id+"F3.boolean.opBoolean","INTERSECT",EDGE,{"derivedFrom":[makeQuery(id+"F1.opExtrude","CAP_FACE",FACE,{"disambiguationData":[OSD([sQuery(id+"F0.wireOp",EDGE,"E0.rect.bottom"),sQuery(id+"F0.wireOp",EDGE,"E0.rect.top"),sQuery(id+"F0.wireOp",EDGE,"E0.rect.left"),sQuery(id+"F0.wireOp",EDGE,"E0.rect.right")])],"isStart":true}),makeQuery(id+"F3.opExtrude","SWEPT_FACE",FACE,{"disambiguationData":[OSD([sQuery(id+"F2.wireOp",EDGE,"E2.6.0.2")])]})]});
            var Q346;
            Q346=makeQuery(id+"F3.boolean.opBoolean","COPY",FACE,{"derivedFrom":makeQuery(id+"F3.opExtrude","SWEPT_FACE",FACE,{"disambiguationData":[OSD([sQuery(id+"F2.wireOp",EDGE,"E2.3.1.2")])]})});
            var Q347;
            Q347=makeQuery(id+"F3.boolean.opBoolean","COPY",FACE,{"derivedFrom":makeQuery(id+"F3.opExtrude","SWEPT_FACE",FACE,{"disambiguationData":[OSD([sQuery(id+"F2.wireOp",EDGE,"E2.2.2.2")])]})});
            var Q348;
            Q348=makeQuery(id+"F3.boolean.opBoolean","COPY",FACE,{"derivedFrom":makeQuery(id+"F3.opExtrude","SWEPT_FACE",FACE,{"disambiguationData":[OSD([sQuery(id+"F2.wireOp",EDGE,"E2.4.0.2")])]})});
            var Q349;
            Q349=makeQuery(id+"F3.boolean.opBoolean","COPY",EDGE,{"derivedFrom":makeQuery(id+"F3.opExtrude","SWEPT_EDGE",EDGE,{"disambiguationData":[OSD([sQuery(id+"F2.wireOp",EDGE,"E2.1.3.1"),sQuery(id+"F2.wireOp",EDGE,"E2.1.3.2")])]})});
            var Q350;
            Q350=makeQuery(id+"F1.opExtrude","SWEPT_EDGE",EDGE,{"disambiguationData":[OSD([sQuery(id+"F0.wireOp",EDGE,"E0.rect.bottom"),sQuery(id+"F0.wireOp",EDGE,"E0.rect.left")])]});
            var Q351;
            Q351=makeQuery(id+"F3.boolean.opBoolean","INTERSECT",EDGE,{"derivedFrom":[makeQuery(id+"F1.opExtrude","CAP_FACE",FACE,{"disambiguationData":[OSD([sQuery(id+"F0.wireOp",EDGE,"E0.rect.bottom"),sQuery(id+"F0.wireOp",EDGE,"E0.rect.top"),sQuery(id+"F0.wireOp",EDGE,"E0.rect.left"),sQuery(id+"F0.wireOp",EDGE,"E0.rect.right")])],"isStart":true}),makeQuery(id+"F3.opExtrude","SWEPT_FACE",FACE,{"disambiguationData":[OSD([sQuery(id+"F2.wireOp",EDGE,"E2.2.4.3")])]})]});
            var Q352;
            Q352=makeQuery(id+"F1.opExtrude","SWEPT_EDGE",EDGE,{"disambiguationData":[OSD([sQuery(id+"F0.wireOp",EDGE,"E0.rect.top"),sQuery(id+"F0.wireOp",EDGE,"E0.rect.left")])]});
            var Q353;
            Q353=makeQuery(id+"F3.boolean.opBoolean","INTERSECT",EDGE,{"derivedFrom":[makeQuery(id+"F1.opExtrude","CAP_FACE",FACE,{"disambiguationData":[OSD([sQuery(id+"F0.wireOp",EDGE,"E0.rect.bottom"),sQuery(id+"F0.wireOp",EDGE,"E0.rect.top"),sQuery(id+"F0.wireOp",EDGE,"E0.rect.left"),sQuery(id+"F0.wireOp",EDGE,"E0.rect.right")])],"isStart":true}),makeQuery(id+"F3.opExtrude","SWEPT_FACE",FACE,{"disambiguationData":[OSD([sQuery(id+"F2.wireOp",EDGE,"E2.6.0.3")])]})]});
            var Q354;
            Q354=makeQuery(id+"F3.boolean.opBoolean","COPY",FACE,{"derivedFrom":makeQuery(id+"F3.opExtrude","SWEPT_FACE",FACE,{"disambiguationData":[OSD([sQuery(id+"F2.wireOp",EDGE,"E2.3.1.3")])]})});
            var Q355;
            Q355=makeQuery(id+"F1.opExtrude","CAP_EDGE",EDGE,{"disambiguationData":[OSD([sQuery(id+"F0.wireOp",EDGE,"E0.rect.bottom")])],"isStart":true});
            var Q356;
            Q356=makeQuery(id+"F3.boolean.opBoolean","INTERSECT",EDGE,{"derivedFrom":[makeQuery(id+"F1.opExtrude","CAP_FACE",FACE,{"disambiguationData":[OSD([sQuery(id+"F0.wireOp",EDGE,"E0.rect.bottom"),sQuery(id+"F0.wireOp",EDGE,"E0.rect.top"),sQuery(id+"F0.wireOp",EDGE,"E0.rect.left"),sQuery(id+"F0.wireOp",EDGE,"E0.rect.right")])],"isStart":true}),makeQuery(id+"F3.opExtrude","SWEPT_FACE",FACE,{"disambiguationData":[OSD([sQuery(id+"F2.wireOp",EDGE,"E2.6.4.3")])]})]});
            var Q357;
            Q357=makeQuery(id+"F1.opExtrude","SWEPT_FACE",FACE,{"disambiguationData":[OSD([sQuery(id+"F0.wireOp",EDGE,"E0.rect.right")])]});
            var Q358;
            Q358=makeQuery(id+"F3.boolean.opBoolean","COPY",FACE,{"derivedFrom":makeQuery(id+"F3.opExtrude","SWEPT_FACE",FACE,{"disambiguationData":[OSD([sQuery(id+"F2.wireOp",EDGE,"E2.4.0.3")])]})});
            var Q359;
            Q359=makeQuery(id+"F1.opExtrude","CAP_EDGE",EDGE,{"disambiguationData":[OSD([sQuery(id+"F0.wireOp",EDGE,"E0.rect.right")])],"isStart":true});
            var Q360;
            Q360=makeQuery(id+"F3.boolean.opBoolean","COPY",EDGE,{"derivedFrom":makeQuery(id+"F3.opExtrude","SWEPT_EDGE",EDGE,{"disambiguationData":[OSD([sQuery(id+"F2.wireOp",EDGE,"E2.2.2.1"),sQuery(id+"F2.wireOp",EDGE,"E2.2.2.3")])]})});
            var Q361;
            Q361=makeQuery(id+"F3.boolean.opBoolean","COPY",EDGE,{"derivedFrom":makeQuery(id+"F3.opExtrude","SWEPT_EDGE",EDGE,{"disambiguationData":[OSD([sQuery(id+"F2.wireOp",EDGE,"E2.1.3.1"),sQuery(id+"F2.wireOp",EDGE,"E2.1.3.3")])]})});
            var Q362;
            Q362=makeQuery(id+"F3.boolean.opBoolean","COPY",EDGE,{"derivedFrom":makeQuery(id+"F3.opExtrude","CAP_EDGE",EDGE,{"disambiguationData":[OSD([sQuery(id+"F2.wireOp",EDGE,"E2.1.4.3")])],"isStart":true})});
            var Q363;
            Q363=makeQuery(id+"F3.boolean.opBoolean","COPY",EDGE,{"derivedFrom":makeQuery(id+"F3.opExtrude","CAP_EDGE",EDGE,{"disambiguationData":[OSD([sQuery(id+"F2.wireOp",EDGE,"E2.1.0.3")])],"isStart":true})});
            var Q364;
            Q364=makeQuery(id+"F3.boolean.opBoolean","COPY",EDGE,{"derivedFrom":makeQuery(id+"F3.opExtrude","SWEPT_EDGE",EDGE,{"disambiguationData":[OSD([sQuery(id+"F2.wireOp",EDGE,"E2.6.2.1"),sQuery(id+"F2.wireOp",EDGE,"E2.6.2.3")])]})});
            var Q365;
            Q365=makeQuery(id+"F3.boolean.opBoolean","COPY",EDGE,{"derivedFrom":makeQuery(id+"F3.opExtrude","SWEPT_EDGE",EDGE,{"disambiguationData":[OSD([sQuery(id+"F2.wireOp",EDGE,"E2.0.3.0"),sQuery(id+"F2.wireOp",EDGE,"E2.0.3.3")])]})});
            var Q366;
            Q366=makeQuery(id+"F3.boolean.opBoolean","COPY",EDGE,{"derivedFrom":makeQuery(id+"F3.opExtrude","SWEPT_EDGE",EDGE,{"disambiguationData":[OSD([sQuery(id+"F2.wireOp",EDGE,"E2.0.3.1"),sQuery(id+"F2.wireOp",EDGE,"E2.0.3.2")])]})});
            var Q367;
            Q367=makeQuery(id+"F3.boolean.opBoolean","COPY",EDGE,{"derivedFrom":makeQuery(id+"F3.opExtrude","SWEPT_EDGE",EDGE,{"disambiguationData":[OSD([sQuery(id+"F2.wireOp",EDGE,"E2.0.3.1"),sQuery(id+"F2.wireOp",EDGE,"E2.0.3.3")])]})});
            var Q368;
            Q368=makeQuery(id+"F3.boolean.opBoolean","COPY",FACE,{"derivedFrom":makeQuery(id+"F3.opExtrude","SWEPT_FACE",FACE,{"disambiguationData":[OSD([sQuery(id+"F2.wireOp",EDGE,"E1.bottom")])]})});
            var Q369;
            Q369=makeQuery(id+"F3.boolean.opBoolean","INTERSECT",EDGE,{"derivedFrom":[makeQuery(id+"F1.opExtrude","CAP_FACE",FACE,{"disambiguationData":[OSD([sQuery(id+"F0.wireOp",EDGE,"E0.rect.bottom"),sQuery(id+"F0.wireOp",EDGE,"E0.rect.top"),sQuery(id+"F0.wireOp",EDGE,"E0.rect.left"),sQuery(id+"F0.wireOp",EDGE,"E0.rect.right")])],"isStart":true}),makeQuery(id+"F3.opExtrude","SWEPT_FACE",FACE,{"disambiguationData":[OSD([sQuery(id+"F2.wireOp",EDGE,"E2.0.3.0")])]})]});
            var Q370;
            Q370=makeQuery(id+"F3.boolean.opBoolean","COPY",EDGE,{"derivedFrom":makeQuery(id+"F3.opExtrude","CAP_EDGE",EDGE,{"disambiguationData":[OSD([sQuery(id+"F2.wireOp",EDGE,"E2.6.4.0")])],"isStart":true})});
            var Q371;
            Q371=makeQuery(id+"F3.boolean.opBoolean","COPY",EDGE,{"derivedFrom":makeQuery(id+"F3.opExtrude","CAP_EDGE",EDGE,{"disambiguationData":[OSD([sQuery(id+"F2.wireOp",EDGE,"E2.6.0.0")])],"isStart":true})});
            var Q372;
            Q372=makeQuery(id+"F3.boolean.opBoolean","INTERSECT",EDGE,{"derivedFrom":[makeQuery(id+"F1.opExtrude","CAP_FACE",FACE,{"disambiguationData":[OSD([sQuery(id+"F0.wireOp",EDGE,"E0.rect.bottom"),sQuery(id+"F0.wireOp",EDGE,"E0.rect.top"),sQuery(id+"F0.wireOp",EDGE,"E0.rect.left"),sQuery(id+"F0.wireOp",EDGE,"E0.rect.right")])],"isStart":true}),makeQuery(id+"F3.opExtrude","SWEPT_FACE",FACE,{"disambiguationData":[OSD([sQuery(id+"F2.wireOp",EDGE,"E2.4.3.0")])]})]});
            var Q373;
            Q373=makeQuery(id+"F3.boolean.opBoolean","COPY",FACE,{"derivedFrom":makeQuery(id+"F3.opExtrude","SWEPT_FACE",FACE,{"disambiguationData":[OSD([sQuery(id+"F2.wireOp",EDGE,"E1.top")])]})});
            var Q374;
            Q374=makeQuery(id+"F3.boolean.opBoolean","COPY",EDGE,{"derivedFrom":makeQuery(id+"F3.opExtrude","SWEPT_EDGE",EDGE,{"disambiguationData":[OSD([sQuery(id+"F2.wireOp",EDGE,"E1.bottom"),sQuery(id+"F2.wireOp",EDGE,"E1.right")])]})});
            var Q375;
            Q375=makeQuery(id+"F3.boolean.opBoolean","INTERSECT",EDGE,{"derivedFrom":[makeQuery(id+"F1.opExtrude","CAP_FACE",FACE,{"disambiguationData":[OSD([sQuery(id+"F0.wireOp",EDGE,"E0.rect.bottom"),sQuery(id+"F0.wireOp",EDGE,"E0.rect.top"),sQuery(id+"F0.wireOp",EDGE,"E0.rect.left"),sQuery(id+"F0.wireOp",EDGE,"E0.rect.right")])],"isStart":true}),makeQuery(id+"F3.opExtrude","SWEPT_FACE",FACE,{"disambiguationData":[OSD([sQuery(id+"F2.wireOp",EDGE,"E2.3.4.0")])]})]});
            var Q376;
            Q376=makeQuery(id+"F3.boolean.opBoolean","COPY",FACE,{"derivedFrom":makeQuery(id+"F3.opExtrude","SWEPT_FACE",FACE,{"disambiguationData":[OSD([sQuery(id+"F2.wireOp",EDGE,"E1.left")])]})});
            var Q377;
            Q377=makeQuery(id+"F3.boolean.opBoolean","INTERSECT",EDGE,{"derivedFrom":[makeQuery(id+"F1.opExtrude","CAP_FACE",FACE,{"disambiguationData":[OSD([sQuery(id+"F0.wireOp",EDGE,"E0.rect.bottom"),sQuery(id+"F0.wireOp",EDGE,"E0.rect.top"),sQuery(id+"F0.wireOp",EDGE,"E0.rect.left"),sQuery(id+"F0.wireOp",EDGE,"E0.rect.right")])],"isStart":true}),makeQuery(id+"F3.opExtrude","SWEPT_FACE",FACE,{"disambiguationData":[OSD([sQuery(id+"F2.wireOp",EDGE,"E2.6.1.0")])]})]});
            var Q378;
            Q378=makeQuery(id+"F3.boolean.opBoolean","COPY",FACE,{"derivedFrom":makeQuery(id+"F3.opExtrude","SWEPT_FACE",FACE,{"disambiguationData":[OSD([sQuery(id+"F2.wireOp",EDGE,"E1.right")])]})});
            var Q379;
            Q379=makeQuery(id+"F3.boolean.opBoolean","COPY",FACE,{"derivedFrom":makeQuery(id+"F3.opExtrude","SWEPT_FACE",FACE,{"disambiguationData":[OSD([sQuery(id+"F2.wireOp",EDGE,"E2.0.1.0")])]})});
            var Q380;
            Q380=makeQuery(id+"F3.boolean.opBoolean","COPY",FACE,{"derivedFrom":makeQuery(id+"F3.opExtrude","SWEPT_FACE",FACE,{"disambiguationData":[OSD([sQuery(id+"F2.wireOp",EDGE,"E2.3.2.0")])]})});
            var Q381;
            Q381=makeQuery(id+"F3.boolean.opBoolean","COPY",FACE,{"derivedFrom":makeQuery(id+"F3.opExtrude","SWEPT_FACE",FACE,{"disambiguationData":[OSD([sQuery(id+"F2.wireOp",EDGE,"E2.1.0.0")])]})});
            var Q382;
            Q382=makeQuery(id+"F3.boolean.opBoolean","COPY",FACE,{"derivedFrom":makeQuery(id+"F3.opExtrude","SWEPT_FACE",FACE,{"disambiguationData":[OSD([sQuery(id+"F2.wireOp",EDGE,"E2.0.1.1")])]})});
            var Q383;
            Q383=makeQuery(id+"F3.boolean.opBoolean","COPY",EDGE,{"derivedFrom":makeQuery(id+"F3.opExtrude","SWEPT_EDGE",EDGE,{"disambiguationData":[OSD([sQuery(id+"F2.wireOp",EDGE,"E2.0.1.0"),sQuery(id+"F2.wireOp",EDGE,"E2.0.1.3")])]})});
            var Q384;
            Q384=makeQuery(id+"F3.boolean.opBoolean","COPY",FACE,{"derivedFrom":makeQuery(id+"F3.opExtrude","SWEPT_FACE",FACE,{"disambiguationData":[OSD([sQuery(id+"F2.wireOp",EDGE,"E2.4.1.0")])]})});
            var Q385;
            Q385=makeQuery(id+"F3.boolean.opBoolean","COPY",FACE,{"derivedFrom":makeQuery(id+"F3.opExtrude","SWEPT_FACE",FACE,{"disambiguationData":[OSD([sQuery(id+"F2.wireOp",EDGE,"E2.0.1.2")])]})});
            var Q386;
            Q386=makeQuery(id+"F3.boolean.opBoolean","COPY",FACE,{"derivedFrom":makeQuery(id+"F3.opExtrude","SWEPT_FACE",FACE,{"disambiguationData":[OSD([sQuery(id+"F2.wireOp",EDGE,"E2.0.1.3")])]})});
            var Q387;
            Q387=makeQuery(id+"F3.boolean.opBoolean","COPY",FACE,{"derivedFrom":makeQuery(id+"F3.opExtrude","SWEPT_FACE",FACE,{"disambiguationData":[OSD([sQuery(id+"F2.wireOp",EDGE,"E2.0.2.0")])]})});
            var Q388;
            Q388=makeQuery(id+"F3.boolean.opBoolean","COPY",EDGE,{"derivedFrom":makeQuery(id+"F3.opExtrude","SWEPT_EDGE",EDGE,{"disambiguationData":[OSD([sQuery(id+"F2.wireOp",EDGE,"E2.0.2.0"),sQuery(id+"F2.wireOp",EDGE,"E2.0.2.2")])]})});
            var Q389;
            Q389=makeQuery(id+"F3.boolean.opBoolean","COPY",EDGE,{"derivedFrom":makeQuery(id+"F3.opExtrude","SWEPT_EDGE",EDGE,{"disambiguationData":[OSD([sQuery(id+"F2.wireOp",EDGE,"E2.0.2.0"),sQuery(id+"F2.wireOp",EDGE,"E2.0.2.3")])]})});
            var Q390;
            Q390=makeQuery(id+"F3.boolean.opBoolean","COPY",EDGE,{"derivedFrom":makeQuery(id+"F3.opExtrude","SWEPT_EDGE",EDGE,{"disambiguationData":[OSD([sQuery(id+"F2.wireOp",EDGE,"E2.0.2.1"),sQuery(id+"F2.wireOp",EDGE,"E2.0.2.2")])]})});
            var Q391;
            Q391=makeQuery(id+"F3.boolean.opBoolean","COPY",EDGE,{"derivedFrom":makeQuery(id+"F3.opExtrude","SWEPT_EDGE",EDGE,{"disambiguationData":[OSD([sQuery(id+"F2.wireOp",EDGE,"E2.2.3.0"),sQuery(id+"F2.wireOp",EDGE,"E2.2.3.2")])]})});
            var Q392;
            Q392=makeQuery(id+"F3.boolean.opBoolean","COPY",EDGE,{"derivedFrom":makeQuery(id+"F3.opExtrude","SWEPT_EDGE",EDGE,{"disambiguationData":[OSD([sQuery(id+"F2.wireOp",EDGE,"E2.1.4.0"),sQuery(id+"F2.wireOp",EDGE,"E2.1.4.2")])]})});
            var Q393;
            Q393=makeQuery(id+"F3.boolean.opBoolean","COPY",FACE,{"derivedFrom":makeQuery(id+"F3.opExtrude","SWEPT_FACE",FACE,{"disambiguationData":[OSD([sQuery(id+"F2.wireOp",EDGE,"E2.0.2.3")])]})});
            var Q394;
            Q394=makeQuery(id+"F3.boolean.opBoolean","COPY",EDGE,{"derivedFrom":makeQuery(id+"F3.opExtrude","SWEPT_EDGE",EDGE,{"disambiguationData":[OSD([sQuery(id+"F2.wireOp",EDGE,"E2.0.2.1"),sQuery(id+"F2.wireOp",EDGE,"E2.0.2.3")])]})});
            var Q395;
            Q395=makeQuery(id+"F3.boolean.opBoolean","COPY",EDGE,{"derivedFrom":makeQuery(id+"F3.opExtrude","SWEPT_EDGE",EDGE,{"disambiguationData":[OSD([sQuery(id+"F2.wireOp",EDGE,"E2.5.4.0"),sQuery(id+"F2.wireOp",EDGE,"E2.5.4.2")])]})});
            var Q396;
            Q396=makeQuery(id+"F3.boolean.opBoolean","COPY",EDGE,{"derivedFrom":makeQuery(id+"F3.opExtrude","SWEPT_EDGE",EDGE,{"disambiguationData":[OSD([sQuery(id+"F2.wireOp",EDGE,"E2.0.3.0"),sQuery(id+"F2.wireOp",EDGE,"E2.0.3.2")])]})});
            var Q397;
            Q397=makeQuery(id+"F3.boolean.opBoolean","COPY",EDGE,{"derivedFrom":makeQuery(id+"F3.opExtrude","CAP_EDGE",EDGE,{"disambiguationData":[OSD([sQuery(id+"F2.wireOp",EDGE,"E2.1.1.0")])],"isStart":true})});
            var Q398;
            Q398=makeQuery(id+"F3.boolean.opBoolean","COPY",EDGE,{"derivedFrom":makeQuery(id+"F3.opExtrude","SWEPT_EDGE",EDGE,{"disambiguationData":[OSD([sQuery(id+"F2.wireOp",EDGE,"E2.6.3.0"),sQuery(id+"F2.wireOp",EDGE,"E2.6.3.2")])]})});
            var Q399;
            Q399=makeQuery(id+"F3.boolean.opBoolean","COPY",EDGE,{"derivedFrom":makeQuery(id+"F3.opExtrude","CAP_EDGE",EDGE,{"disambiguationData":[OSD([sQuery(id+"F2.wireOp",EDGE,"E2.3.3.0")])],"isStart":true})});
            var Q400;
            Q400=makeQuery(id+"F3.boolean.opBoolean","COPY",EDGE,{"derivedFrom":makeQuery(id+"F3.opExtrude","CAP_EDGE",EDGE,{"disambiguationData":[OSD([sQuery(id+"F2.wireOp",EDGE,"E2.2.4.0")])],"isStart":true})});
            var Q401;
            Q401=makeQuery(id+"F3.boolean.opBoolean","INTERSECT",EDGE,{"derivedFrom":[makeQuery(id+"F1.opExtrude","CAP_FACE",FACE,{"disambiguationData":[OSD([sQuery(id+"F0.wireOp",EDGE,"E0.rect.bottom"),sQuery(id+"F0.wireOp",EDGE,"E0.rect.top"),sQuery(id+"F0.wireOp",EDGE,"E0.rect.left"),sQuery(id+"F0.wireOp",EDGE,"E0.rect.right")])],"isStart":true}),makeQuery(id+"F3.opExtrude","SWEPT_FACE",FACE,{"disambiguationData":[OSD([sQuery(id+"F2.wireOp",EDGE,"E2.4.3.1")])]})]});
            var Q402;
            Q402=makeQuery(id+"F3.boolean.opBoolean","INTERSECT",EDGE,{"derivedFrom":[makeQuery(id+"F1.opExtrude","CAP_FACE",FACE,{"disambiguationData":[OSD([sQuery(id+"F0.wireOp",EDGE,"E0.rect.bottom"),sQuery(id+"F0.wireOp",EDGE,"E0.rect.top"),sQuery(id+"F0.wireOp",EDGE,"E0.rect.left"),sQuery(id+"F0.wireOp",EDGE,"E0.rect.right")])],"isStart":true}),makeQuery(id+"F3.opExtrude","SWEPT_FACE",FACE,{"disambiguationData":[OSD([sQuery(id+"F2.wireOp",EDGE,"E2.3.4.1")])]})]});
            var Q403;
            Q403=makeQuery(id+"F3.boolean.opBoolean","INTERSECT",EDGE,{"derivedFrom":[makeQuery(id+"F1.opExtrude","CAP_FACE",FACE,{"disambiguationData":[OSD([sQuery(id+"F0.wireOp",EDGE,"E0.rect.bottom"),sQuery(id+"F0.wireOp",EDGE,"E0.rect.top"),sQuery(id+"F0.wireOp",EDGE,"E0.rect.left"),sQuery(id+"F0.wireOp",EDGE,"E0.rect.right")])],"isStart":true}),makeQuery(id+"F3.opExtrude","SWEPT_FACE",FACE,{"disambiguationData":[OSD([sQuery(id+"F2.wireOp",EDGE,"E2.3.0.1")])]})]});
            var Q404;
            Q404=makeQuery(id+"F3.boolean.opBoolean","INTERSECT",EDGE,{"derivedFrom":[makeQuery(id+"F1.opExtrude","CAP_FACE",FACE,{"disambiguationData":[OSD([sQuery(id+"F0.wireOp",EDGE,"E0.rect.bottom"),sQuery(id+"F0.wireOp",EDGE,"E0.rect.top"),sQuery(id+"F0.wireOp",EDGE,"E0.rect.left"),sQuery(id+"F0.wireOp",EDGE,"E0.rect.right")])],"isStart":true}),makeQuery(id+"F3.opExtrude","SWEPT_FACE",FACE,{"disambiguationData":[OSD([sQuery(id+"F2.wireOp",EDGE,"E2.2.1.1")])]})]});
            var Q405;
            Q405=makeQuery(id+"F3.boolean.opBoolean","INTERSECT",EDGE,{"derivedFrom":[makeQuery(id+"F1.opExtrude","CAP_FACE",FACE,{"disambiguationData":[OSD([sQuery(id+"F0.wireOp",EDGE,"E0.rect.bottom"),sQuery(id+"F0.wireOp",EDGE,"E0.rect.top"),sQuery(id+"F0.wireOp",EDGE,"E0.rect.left"),sQuery(id+"F0.wireOp",EDGE,"E0.rect.right")])],"isStart":true}),makeQuery(id+"F3.opExtrude","SWEPT_FACE",FACE,{"disambiguationData":[OSD([sQuery(id+"F2.wireOp",EDGE,"E2.6.1.1")])]})]});
            var Q406;
            Q406=makeQuery(id+"F3.boolean.opBoolean","INTERSECT",EDGE,{"derivedFrom":[makeQuery(id+"F1.opExtrude","CAP_FACE",FACE,{"disambiguationData":[OSD([sQuery(id+"F0.wireOp",EDGE,"E0.rect.bottom"),sQuery(id+"F0.wireOp",EDGE,"E0.rect.top"),sQuery(id+"F0.wireOp",EDGE,"E0.rect.left"),sQuery(id+"F0.wireOp",EDGE,"E0.rect.right")])],"isStart":true}),makeQuery(id+"F3.opExtrude","SWEPT_FACE",FACE,{"disambiguationData":[OSD([sQuery(id+"F2.wireOp",EDGE,"E2.5.2.1")])]})]});
            var Q407;
            Q407=makeQuery(id+"F3.boolean.opBoolean","COPY",FACE,{"derivedFrom":makeQuery(id+"F3.opExtrude","SWEPT_FACE",FACE,{"disambiguationData":[OSD([sQuery(id+"F2.wireOp",EDGE,"E2.3.2.1")])]})});
            var Q408;
            Q408=makeQuery(id+"F3.boolean.opBoolean","COPY",FACE,{"derivedFrom":makeQuery(id+"F3.opExtrude","SWEPT_FACE",FACE,{"disambiguationData":[OSD([sQuery(id+"F2.wireOp",EDGE,"E2.2.3.1")])]})});
            var Q409;
            Q409=makeQuery(id+"F3.boolean.opBoolean","COPY",FACE,{"derivedFrom":makeQuery(id+"F3.opExtrude","SWEPT_FACE",FACE,{"disambiguationData":[OSD([sQuery(id+"F2.wireOp",EDGE,"E2.1.4.1")])]})});
            var Q410;
            Q410=makeQuery(id+"F3.boolean.opBoolean","COPY",FACE,{"derivedFrom":makeQuery(id+"F3.opExtrude","SWEPT_FACE",FACE,{"disambiguationData":[OSD([sQuery(id+"F2.wireOp",EDGE,"E2.1.0.1")])]})});
            var Q411;
            Q411=makeQuery(id+"F3.boolean.opBoolean","COPY",FACE,{"derivedFrom":makeQuery(id+"F3.opExtrude","SWEPT_FACE",FACE,{"disambiguationData":[OSD([sQuery(id+"F2.wireOp",EDGE,"E2.5.4.1")])]})});
            var Q412;
            Q412=makeQuery(id+"F3.boolean.opBoolean","COPY",FACE,{"derivedFrom":makeQuery(id+"F3.opExtrude","SWEPT_FACE",FACE,{"disambiguationData":[OSD([sQuery(id+"F2.wireOp",EDGE,"E2.4.1.1")])]})});
            var Q413;
            Q413=makeQuery(id+"F3.boolean.opBoolean","COPY",EDGE,{"derivedFrom":makeQuery(id+"F3.opExtrude","SWEPT_EDGE",EDGE,{"disambiguationData":[OSD([sQuery(id+"F2.wireOp",EDGE,"E2.2.3.0"),sQuery(id+"F2.wireOp",EDGE,"E2.2.3.3")])]})});
            var Q414;
            Q414=makeQuery(id+"F3.boolean.opBoolean","COPY",EDGE,{"derivedFrom":makeQuery(id+"F3.opExtrude","SWEPT_EDGE",EDGE,{"disambiguationData":[OSD([sQuery(id+"F2.wireOp",EDGE,"E2.1.4.0"),sQuery(id+"F2.wireOp",EDGE,"E2.1.4.3")])]})});
            var Q415;
            Q415=makeQuery(id+"F3.boolean.opBoolean","COPY",EDGE,{"derivedFrom":makeQuery(id+"F3.opExtrude","SWEPT_EDGE",EDGE,{"disambiguationData":[OSD([sQuery(id+"F2.wireOp",EDGE,"E2.1.0.0"),sQuery(id+"F2.wireOp",EDGE,"E2.1.0.3")])]})});
            var Q416;
            Q416=makeQuery(id+"F3.boolean.opBoolean","COPY",EDGE,{"derivedFrom":makeQuery(id+"F3.opExtrude","SWEPT_EDGE",EDGE,{"disambiguationData":[OSD([sQuery(id+"F2.wireOp",EDGE,"E2.5.4.0"),sQuery(id+"F2.wireOp",EDGE,"E2.5.4.3")])]})});
            var Q417;
            Q417=makeQuery(id+"F3.boolean.opBoolean","COPY",EDGE,{"derivedFrom":makeQuery(id+"F3.opExtrude","SWEPT_EDGE",EDGE,{"disambiguationData":[OSD([sQuery(id+"F2.wireOp",EDGE,"E2.5.0.0"),sQuery(id+"F2.wireOp",EDGE,"E2.5.0.3")])]})});
            var Q418;
            Q418=makeQuery(id+"F3.boolean.opBoolean","COPY",EDGE,{"derivedFrom":makeQuery(id+"F3.opExtrude","SWEPT_EDGE",EDGE,{"disambiguationData":[OSD([sQuery(id+"F2.wireOp",EDGE,"E2.4.1.0"),sQuery(id+"F2.wireOp",EDGE,"E2.4.1.3")])]})});
            var Q419;
            Q419=makeQuery(id+"F3.boolean.opBoolean","COPY",EDGE,{"derivedFrom":makeQuery(id+"F3.opExtrude","SWEPT_EDGE",EDGE,{"disambiguationData":[OSD([sQuery(id+"F2.wireOp",EDGE,"E2.3.2.0"),sQuery(id+"F2.wireOp",EDGE,"E2.3.2.3")])]})});
            var Q420;
            Q420=makeQuery(id+"F3.boolean.opBoolean","COPY",EDGE,{"derivedFrom":makeQuery(id+"F3.opExtrude","CAP_EDGE",EDGE,{"disambiguationData":[OSD([sQuery(id+"F2.wireOp",EDGE,"E2.2.0.1")])],"isStart":true})});
            var Q421;
            Q421=makeQuery(id+"F3.boolean.opBoolean","COPY",EDGE,{"derivedFrom":makeQuery(id+"F3.opExtrude","CAP_EDGE",EDGE,{"disambiguationData":[OSD([sQuery(id+"F2.wireOp",EDGE,"E2.1.1.1")])],"isStart":true})});
            var Q422;
            Q422=makeQuery(id+"F3.boolean.opBoolean","COPY",EDGE,{"derivedFrom":makeQuery(id+"F3.opExtrude","SWEPT_EDGE",EDGE,{"disambiguationData":[OSD([sQuery(id+"F2.wireOp",EDGE,"E2.6.3.0"),sQuery(id+"F2.wireOp",EDGE,"E2.6.3.3")])]})});
            var Q423;
            Q423=makeQuery(id+"F3.boolean.opBoolean","COPY",EDGE,{"derivedFrom":makeQuery(id+"F3.opExtrude","CAP_EDGE",EDGE,{"disambiguationData":[OSD([sQuery(id+"F2.wireOp",EDGE,"E2.5.1.1")])],"isStart":true})});
            var Q424;
            Q424=makeQuery(id+"F3.boolean.opBoolean","INTERSECT",EDGE,{"derivedFrom":[makeQuery(id+"F1.opExtrude","CAP_FACE",FACE,{"disambiguationData":[OSD([sQuery(id+"F0.wireOp",EDGE,"E0.rect.bottom"),sQuery(id+"F0.wireOp",EDGE,"E0.rect.top"),sQuery(id+"F0.wireOp",EDGE,"E0.rect.left"),sQuery(id+"F0.wireOp",EDGE,"E0.rect.right")])],"isStart":true}),makeQuery(id+"F3.opExtrude","SWEPT_FACE",FACE,{"disambiguationData":[OSD([sQuery(id+"F2.wireOp",EDGE,"E2.1.2.1")])]})]});
            var Q425;
            Q425=makeQuery(id+"F3.boolean.opBoolean","INTERSECT",EDGE,{"derivedFrom":[makeQuery(id+"F1.opExtrude","CAP_FACE",FACE,{"disambiguationData":[OSD([sQuery(id+"F0.wireOp",EDGE,"E0.rect.bottom"),sQuery(id+"F0.wireOp",EDGE,"E0.rect.top"),sQuery(id+"F0.wireOp",EDGE,"E0.rect.left"),sQuery(id+"F0.wireOp",EDGE,"E0.rect.right")])],"isStart":true}),makeQuery(id+"F3.opExtrude","SWEPT_FACE",FACE,{"disambiguationData":[OSD([sQuery(id+"F2.wireOp",EDGE,"E2.0.3.1")])]})]});
            var Q426;
            Q426=makeQuery(id+"F3.boolean.opBoolean","INTERSECT",EDGE,{"derivedFrom":[makeQuery(id+"F1.opExtrude","CAP_FACE",FACE,{"disambiguationData":[OSD([sQuery(id+"F0.wireOp",EDGE,"E0.rect.bottom"),sQuery(id+"F0.wireOp",EDGE,"E0.rect.top"),sQuery(id+"F0.wireOp",EDGE,"E0.rect.left"),sQuery(id+"F0.wireOp",EDGE,"E0.rect.right")])],"isStart":true}),makeQuery(id+"F3.opExtrude","SWEPT_FACE",FACE,{"disambiguationData":[OSD([sQuery(id+"F2.wireOp",EDGE,"E2.3.3.3")])]})]});
            var Q427;
            Q427=makeQuery(id+"F3.boolean.opBoolean","INTERSECT",EDGE,{"derivedFrom":[makeQuery(id+"F1.opExtrude","CAP_FACE",FACE,{"disambiguationData":[OSD([sQuery(id+"F0.wireOp",EDGE,"E0.rect.bottom"),sQuery(id+"F0.wireOp",EDGE,"E0.rect.top"),sQuery(id+"F0.wireOp",EDGE,"E0.rect.left"),sQuery(id+"F0.wireOp",EDGE,"E0.rect.right")])],"isStart":true}),makeQuery(id+"F3.opExtrude","SWEPT_FACE",FACE,{"disambiguationData":[OSD([sQuery(id+"F2.wireOp",EDGE,"E2.1.1.3")])]})]});
            var Q428;
            Q428=makeQuery(id+"F3.boolean.opBoolean","COPY",EDGE,{"derivedFrom":makeQuery(id+"F3.opExtrude","CAP_EDGE",EDGE,{"disambiguationData":[OSD([sQuery(id+"F2.wireOp",EDGE,"E2.3.2.3")])],"isStart":true})});
            var Q429;
            Q429=makeQuery(id+"F3.boolean.opBoolean","COPY",EDGE,{"derivedFrom":makeQuery(id+"F3.opExtrude","SWEPT_EDGE",EDGE,{"disambiguationData":[OSD([sQuery(id+"F2.wireOp",EDGE,"E2.3.1.1"),sQuery(id+"F2.wireOp",EDGE,"E2.3.1.2")])]})});
            var Q430;
            Q430=makeQuery(id+"F3.boolean.opBoolean","COPY",EDGE,{"derivedFrom":makeQuery(id+"F3.opExtrude","SWEPT_EDGE",EDGE,{"disambiguationData":[OSD([sQuery(id+"F2.wireOp",EDGE,"E2.0.4.1"),sQuery(id+"F2.wireOp",EDGE,"E2.0.4.2")])]})});
            var Q431;
            Q431=makeQuery(id+"F3.boolean.opBoolean","COPY",EDGE,{"derivedFrom":makeQuery(id+"F3.opExtrude","SWEPT_EDGE",EDGE,{"disambiguationData":[OSD([sQuery(id+"F2.wireOp",EDGE,"E2.5.1.0"),sQuery(id+"F2.wireOp",EDGE,"E2.5.1.2")])]})});
            var Q432;
            Q432=makeQuery(id+"F3.boolean.opBoolean","COPY",EDGE,{"derivedFrom":makeQuery(id+"F3.opExtrude","CAP_EDGE",EDGE,{"disambiguationData":[OSD([sQuery(id+"F2.wireOp",EDGE,"E2.3.0.0")])],"isStart":true})});
            var Q433;
            Q433=makeQuery(id+"F3.boolean.opBoolean","COPY",EDGE,{"derivedFrom":makeQuery(id+"F3.opExtrude","CAP_EDGE",EDGE,{"disambiguationData":[OSD([sQuery(id+"F2.wireOp",EDGE,"E2.2.1.0")])],"isStart":true})});
            var Q434;
            Q434=makeQuery(id+"F3.boolean.opBoolean","INTERSECT",EDGE,{"derivedFrom":[makeQuery(id+"F1.opExtrude","CAP_FACE",FACE,{"disambiguationData":[OSD([sQuery(id+"F0.wireOp",EDGE,"E0.rect.bottom"),sQuery(id+"F0.wireOp",EDGE,"E0.rect.top"),sQuery(id+"F0.wireOp",EDGE,"E0.rect.left"),sQuery(id+"F0.wireOp",EDGE,"E0.rect.right")])],"isStart":true}),makeQuery(id+"F3.opExtrude","SWEPT_FACE",FACE,{"disambiguationData":[OSD([sQuery(id+"F2.wireOp",EDGE,"E1.bottom")])]})]});
            var Q435;
            Q435=makeQuery(id+"F3.boolean.opBoolean","COPY",EDGE,{"derivedFrom":makeQuery(id+"F3.opExtrude","CAP_EDGE",EDGE,{"disambiguationData":[OSD([sQuery(id+"F2.wireOp",EDGE,"E2.1.2.0")])],"isStart":true})});
            var Q436;
            Q436=makeQuery(id+"F3.boolean.opBoolean","COPY",EDGE,{"derivedFrom":makeQuery(id+"F3.opExtrude","CAP_EDGE",EDGE,{"disambiguationData":[OSD([sQuery(id+"F2.wireOp",EDGE,"E2.5.2.0")])],"isStart":true})});
            var Q437;
            Q437=makeQuery(id+"F3.boolean.opBoolean","INTERSECT",EDGE,{"derivedFrom":[makeQuery(id+"F1.opExtrude","CAP_FACE",FACE,{"disambiguationData":[OSD([sQuery(id+"F0.wireOp",EDGE,"E0.rect.bottom"),sQuery(id+"F0.wireOp",EDGE,"E0.rect.top"),sQuery(id+"F0.wireOp",EDGE,"E0.rect.left"),sQuery(id+"F0.wireOp",EDGE,"E0.rect.right")])],"isStart":true}),makeQuery(id+"F3.opExtrude","SWEPT_FACE",FACE,{"disambiguationData":[OSD([sQuery(id+"F2.wireOp",EDGE,"E2.3.1.0")])]})]});
            var Q438;
            Q438=makeQuery(id+"F3.boolean.opBoolean","INTERSECT",EDGE,{"derivedFrom":[makeQuery(id+"F1.opExtrude","CAP_FACE",FACE,{"disambiguationData":[OSD([sQuery(id+"F0.wireOp",EDGE,"E0.rect.bottom"),sQuery(id+"F0.wireOp",EDGE,"E0.rect.top"),sQuery(id+"F0.wireOp",EDGE,"E0.rect.left"),sQuery(id+"F0.wireOp",EDGE,"E0.rect.right")])],"isStart":true}),makeQuery(id+"F3.opExtrude","SWEPT_FACE",FACE,{"disambiguationData":[OSD([sQuery(id+"F2.wireOp",EDGE,"E2.2.2.0")])]})]});
            var Q439;
            Q439=makeQuery(id+"F3.boolean.opBoolean","INTERSECT",EDGE,{"derivedFrom":[makeQuery(id+"F1.opExtrude","CAP_FACE",FACE,{"disambiguationData":[OSD([sQuery(id+"F0.wireOp",EDGE,"E0.rect.bottom"),sQuery(id+"F0.wireOp",EDGE,"E0.rect.top"),sQuery(id+"F0.wireOp",EDGE,"E0.rect.left"),sQuery(id+"F0.wireOp",EDGE,"E0.rect.right")])],"isStart":true}),makeQuery(id+"F3.opExtrude","SWEPT_FACE",FACE,{"disambiguationData":[OSD([sQuery(id+"F2.wireOp",EDGE,"E2.4.0.0")])]})]});
            var Q440;
            Q440=makeQuery(id+"F3.boolean.opBoolean","INTERSECT",EDGE,{"derivedFrom":[makeQuery(id+"F1.opExtrude","CAP_FACE",FACE,{"disambiguationData":[OSD([sQuery(id+"F0.wireOp",EDGE,"E0.rect.bottom"),sQuery(id+"F0.wireOp",EDGE,"E0.rect.top"),sQuery(id+"F0.wireOp",EDGE,"E0.rect.left"),sQuery(id+"F0.wireOp",EDGE,"E0.rect.right")])],"isStart":true}),makeQuery(id+"F3.opExtrude","SWEPT_FACE",FACE,{"disambiguationData":[OSD([sQuery(id+"F2.wireOp",EDGE,"E2.5.2.2")])]})]});
            var Q441;
            Q441=makeQuery(id+"F3.boolean.opBoolean","COPY",EDGE,{"derivedFrom":makeQuery(id+"F3.opExtrude","SWEPT_EDGE",EDGE,{"disambiguationData":[OSD([sQuery(id+"F2.wireOp",EDGE,"E2.2.3.1"),sQuery(id+"F2.wireOp",EDGE,"E2.2.3.2")])]})});
            var Q442;
            Q442=makeQuery(id+"F3.boolean.opBoolean","COPY",EDGE,{"derivedFrom":makeQuery(id+"F3.opExtrude","SWEPT_EDGE",EDGE,{"disambiguationData":[OSD([sQuery(id+"F2.wireOp",EDGE,"E2.1.4.1"),sQuery(id+"F2.wireOp",EDGE,"E2.1.4.2")])]})});
            var Q443;
            Q443=makeQuery(id+"F3.boolean.opBoolean","COPY",EDGE,{"derivedFrom":makeQuery(id+"F3.opExtrude","SWEPT_EDGE",EDGE,{"disambiguationData":[OSD([sQuery(id+"F2.wireOp",EDGE,"E2.1.0.1"),sQuery(id+"F2.wireOp",EDGE,"E2.1.0.2")])]})});
            var Q444;
            Q444=makeQuery(id+"F3.boolean.opBoolean","COPY",EDGE,{"derivedFrom":makeQuery(id+"F3.opExtrude","SWEPT_EDGE",EDGE,{"disambiguationData":[OSD([sQuery(id+"F2.wireOp",EDGE,"E2.5.4.1"),sQuery(id+"F2.wireOp",EDGE,"E2.5.4.2")])]})});
            var Q445;
            Q445=makeQuery(id+"F3.boolean.opBoolean","COPY",EDGE,{"derivedFrom":makeQuery(id+"F3.opExtrude","SWEPT_EDGE",EDGE,{"disambiguationData":[OSD([sQuery(id+"F2.wireOp",EDGE,"E2.5.0.1"),sQuery(id+"F2.wireOp",EDGE,"E2.5.0.2")])]})});
            var Q446;
            Q446=makeQuery(id+"F3.boolean.opBoolean","COPY",EDGE,{"derivedFrom":makeQuery(id+"F3.opExtrude","SWEPT_EDGE",EDGE,{"disambiguationData":[OSD([sQuery(id+"F2.wireOp",EDGE,"E2.4.1.1"),sQuery(id+"F2.wireOp",EDGE,"E2.4.1.2")])]})});
            var Q447;
            Q447=makeQuery(id+"F3.boolean.opBoolean","COPY",EDGE,{"derivedFrom":makeQuery(id+"F3.opExtrude","SWEPT_EDGE",EDGE,{"disambiguationData":[OSD([sQuery(id+"F2.wireOp",EDGE,"E2.3.2.1"),sQuery(id+"F2.wireOp",EDGE,"E2.3.2.2")])]})});
            var Q448;
            Q448=makeQuery(id+"F3.boolean.opBoolean","INTERSECT",EDGE,{"derivedFrom":[makeQuery(id+"F1.opExtrude","CAP_FACE",FACE,{"disambiguationData":[OSD([sQuery(id+"F0.wireOp",EDGE,"E0.rect.bottom"),sQuery(id+"F0.wireOp",EDGE,"E0.rect.top"),sQuery(id+"F0.wireOp",EDGE,"E0.rect.left"),sQuery(id+"F0.wireOp",EDGE,"E0.rect.right")])],"isStart":true}),makeQuery(id+"F3.opExtrude","SWEPT_FACE",FACE,{"disambiguationData":[OSD([sQuery(id+"F2.wireOp",EDGE,"E2.4.3.2")])]})]});
            var Q449;
            Q449=makeQuery(id+"F3.boolean.opBoolean","INTERSECT",EDGE,{"derivedFrom":[makeQuery(id+"F1.opExtrude","CAP_FACE",FACE,{"disambiguationData":[OSD([sQuery(id+"F0.wireOp",EDGE,"E0.rect.bottom"),sQuery(id+"F0.wireOp",EDGE,"E0.rect.top"),sQuery(id+"F0.wireOp",EDGE,"E0.rect.left"),sQuery(id+"F0.wireOp",EDGE,"E0.rect.right")])],"isStart":true}),makeQuery(id+"F3.opExtrude","SWEPT_FACE",FACE,{"disambiguationData":[OSD([sQuery(id+"F2.wireOp",EDGE,"E2.3.4.2")])]})]});
            var Q450;
            Q450=makeQuery(id+"F3.boolean.opBoolean","INTERSECT",EDGE,{"derivedFrom":[makeQuery(id+"F1.opExtrude","CAP_FACE",FACE,{"disambiguationData":[OSD([sQuery(id+"F0.wireOp",EDGE,"E0.rect.bottom"),sQuery(id+"F0.wireOp",EDGE,"E0.rect.top"),sQuery(id+"F0.wireOp",EDGE,"E0.rect.left"),sQuery(id+"F0.wireOp",EDGE,"E0.rect.right")])],"isStart":true}),makeQuery(id+"F3.opExtrude","SWEPT_FACE",FACE,{"disambiguationData":[OSD([sQuery(id+"F2.wireOp",EDGE,"E2.3.0.2")])]})]});
            var Q451;
            Q451=makeQuery(id+"F3.boolean.opBoolean","INTERSECT",EDGE,{"derivedFrom":[makeQuery(id+"F1.opExtrude","CAP_FACE",FACE,{"disambiguationData":[OSD([sQuery(id+"F0.wireOp",EDGE,"E0.rect.bottom"),sQuery(id+"F0.wireOp",EDGE,"E0.rect.top"),sQuery(id+"F0.wireOp",EDGE,"E0.rect.left"),sQuery(id+"F0.wireOp",EDGE,"E0.rect.right")])],"isStart":true}),makeQuery(id+"F3.opExtrude","SWEPT_FACE",FACE,{"disambiguationData":[OSD([sQuery(id+"F2.wireOp",EDGE,"E2.2.1.2")])]})]});
            var Q452;
            Q452=makeQuery(id+"F3.boolean.opBoolean","COPY",EDGE,{"derivedFrom":makeQuery(id+"F3.opExtrude","SWEPT_EDGE",EDGE,{"disambiguationData":[OSD([sQuery(id+"F2.wireOp",EDGE,"E2.1.1.1"),sQuery(id+"F2.wireOp",EDGE,"E2.1.1.2")])]})});
            var Q453;
            Q453=makeQuery(id+"F3.boolean.opBoolean","COPY",EDGE,{"derivedFrom":makeQuery(id+"F3.opExtrude","SWEPT_EDGE",EDGE,{"disambiguationData":[OSD([sQuery(id+"F2.wireOp",EDGE,"E2.4.2.1"),sQuery(id+"F2.wireOp",EDGE,"E2.4.2.2")])]})});
            var Q454;
            Q454=makeQuery(id+"F3.boolean.opBoolean","COPY",EDGE,{"derivedFrom":makeQuery(id+"F3.opExtrude","SWEPT_EDGE",EDGE,{"disambiguationData":[OSD([sQuery(id+"F2.wireOp",EDGE,"E2.3.3.1"),sQuery(id+"F2.wireOp",EDGE,"E2.3.3.2")])]})});
            var Q455;
            Q455=makeQuery(id+"F3.boolean.opBoolean","COPY",EDGE,{"derivedFrom":makeQuery(id+"F3.opExtrude","SWEPT_EDGE",EDGE,{"disambiguationData":[OSD([sQuery(id+"F2.wireOp",EDGE,"E2.2.0.1"),sQuery(id+"F2.wireOp",EDGE,"E2.2.0.2")])]})});
            var Q456;
            Q456=makeQuery(id+"F3.boolean.opBoolean","COPY",EDGE,{"derivedFrom":makeQuery(id+"F3.opExtrude","SWEPT_EDGE",EDGE,{"disambiguationData":[OSD([sQuery(id+"F2.wireOp",EDGE,"E2.5.1.1"),sQuery(id+"F2.wireOp",EDGE,"E2.5.1.2")])]})});
            var Q457;
            Q457=makeQuery(id+"F3.boolean.opBoolean","INTERSECT",EDGE,{"derivedFrom":[makeQuery(id+"F1.opExtrude","CAP_FACE",FACE,{"disambiguationData":[OSD([sQuery(id+"F0.wireOp",EDGE,"E0.rect.bottom"),sQuery(id+"F0.wireOp",EDGE,"E0.rect.top"),sQuery(id+"F0.wireOp",EDGE,"E0.rect.left"),sQuery(id+"F0.wireOp",EDGE,"E0.rect.right")])],"isStart":true}),makeQuery(id+"F3.opExtrude","SWEPT_FACE",FACE,{"disambiguationData":[OSD([sQuery(id+"F2.wireOp",EDGE,"E1.left")])]})]});
            var Q458;
            Q458=makeQuery(id+"F3.boolean.opBoolean","INTERSECT",EDGE,{"derivedFrom":[makeQuery(id+"F1.opExtrude","CAP_FACE",FACE,{"disambiguationData":[OSD([sQuery(id+"F0.wireOp",EDGE,"E0.rect.bottom"),sQuery(id+"F0.wireOp",EDGE,"E0.rect.top"),sQuery(id+"F0.wireOp",EDGE,"E0.rect.left"),sQuery(id+"F0.wireOp",EDGE,"E0.rect.right")])],"isStart":true}),makeQuery(id+"F3.opExtrude","SWEPT_FACE",FACE,{"disambiguationData":[OSD([sQuery(id+"F2.wireOp",EDGE,"E2.3.1.2")])]})]});
            var Q459;
            Q459=makeQuery(id+"F3.boolean.opBoolean","INTERSECT",EDGE,{"derivedFrom":[makeQuery(id+"F1.opExtrude","CAP_FACE",FACE,{"disambiguationData":[OSD([sQuery(id+"F0.wireOp",EDGE,"E0.rect.bottom"),sQuery(id+"F0.wireOp",EDGE,"E0.rect.top"),sQuery(id+"F0.wireOp",EDGE,"E0.rect.left"),sQuery(id+"F0.wireOp",EDGE,"E0.rect.right")])],"isStart":true}),makeQuery(id+"F3.opExtrude","SWEPT_FACE",FACE,{"disambiguationData":[OSD([sQuery(id+"F2.wireOp",EDGE,"E2.0.4.2")])]})]});
            var Q460;
            Q460=makeQuery(id+"F3.boolean.opBoolean","INTERSECT",EDGE,{"derivedFrom":[makeQuery(id+"F1.opExtrude","CAP_FACE",FACE,{"disambiguationData":[OSD([sQuery(id+"F0.wireOp",EDGE,"E0.rect.bottom"),sQuery(id+"F0.wireOp",EDGE,"E0.rect.top"),sQuery(id+"F0.wireOp",EDGE,"E0.rect.left"),sQuery(id+"F0.wireOp",EDGE,"E0.rect.right")])],"isStart":true}),makeQuery(id+"F3.opExtrude","SWEPT_FACE",FACE,{"disambiguationData":[OSD([sQuery(id+"F2.wireOp",EDGE,"E2.5.3.2")])]})]});
            var Q461;
            Q461=makeQuery(id+"F3.boolean.opBoolean","INTERSECT",EDGE,{"derivedFrom":[makeQuery(id+"F1.opExtrude","CAP_FACE",FACE,{"disambiguationData":[OSD([sQuery(id+"F0.wireOp",EDGE,"E0.rect.bottom"),sQuery(id+"F0.wireOp",EDGE,"E0.rect.top"),sQuery(id+"F0.wireOp",EDGE,"E0.rect.left"),sQuery(id+"F0.wireOp",EDGE,"E0.rect.right")])],"isStart":true}),makeQuery(id+"F3.opExtrude","SWEPT_FACE",FACE,{"disambiguationData":[OSD([sQuery(id+"F2.wireOp",EDGE,"E2.4.4.2")])]})]});
            var Q462;
            Q462=makeQuery(id+"F3.boolean.opBoolean","INTERSECT",EDGE,{"derivedFrom":[makeQuery(id+"F1.opExtrude","CAP_FACE",FACE,{"disambiguationData":[OSD([sQuery(id+"F0.wireOp",EDGE,"E0.rect.bottom"),sQuery(id+"F0.wireOp",EDGE,"E0.rect.top"),sQuery(id+"F0.wireOp",EDGE,"E0.rect.left"),sQuery(id+"F0.wireOp",EDGE,"E0.rect.right")])],"isStart":true}),makeQuery(id+"F3.opExtrude","SWEPT_FACE",FACE,{"disambiguationData":[OSD([sQuery(id+"F2.wireOp",EDGE,"E2.4.0.2")])]})]});
            var Q463;
            Q463=makeQuery(id+"F3.boolean.opBoolean","COPY",EDGE,{"derivedFrom":makeQuery(id+"F3.opExtrude","SWEPT_EDGE",EDGE,{"disambiguationData":[OSD([sQuery(id+"F2.wireOp",EDGE,"E2.1.1.1"),sQuery(id+"F2.wireOp",EDGE,"E2.1.1.3")])]})});
            var Q464;
            Q464=makeQuery(id+"F3.boolean.opBoolean","COPY",EDGE,{"derivedFrom":makeQuery(id+"F3.opExtrude","SWEPT_EDGE",EDGE,{"disambiguationData":[OSD([sQuery(id+"F2.wireOp",EDGE,"E2.4.2.1"),sQuery(id+"F2.wireOp",EDGE,"E2.4.2.3")])]})});
            var Q465;
            Q465=makeQuery(id+"F3.boolean.opBoolean","COPY",EDGE,{"derivedFrom":makeQuery(id+"F3.opExtrude","SWEPT_EDGE",EDGE,{"disambiguationData":[OSD([sQuery(id+"F2.wireOp",EDGE,"E2.3.3.1"),sQuery(id+"F2.wireOp",EDGE,"E2.3.3.3")])]})});
            var Q466;
            Q466=makeQuery(id+"F3.boolean.opBoolean","COPY",EDGE,{"derivedFrom":makeQuery(id+"F3.opExtrude","SWEPT_EDGE",EDGE,{"disambiguationData":[OSD([sQuery(id+"F2.wireOp",EDGE,"E2.2.0.1"),sQuery(id+"F2.wireOp",EDGE,"E2.2.0.3")])]})});
            var Q467;
            Q467=makeQuery(id+"F3.boolean.opBoolean","COPY",EDGE,{"derivedFrom":makeQuery(id+"F3.opExtrude","SWEPT_EDGE",EDGE,{"disambiguationData":[OSD([sQuery(id+"F2.wireOp",EDGE,"E2.5.1.1"),sQuery(id+"F2.wireOp",EDGE,"E2.5.1.3")])]})});
            var Q468;
            Q468=makeQuery(id+"F3.boolean.opBoolean","COPY",EDGE,{"derivedFrom":makeQuery(id+"F3.opExtrude","CAP_EDGE",EDGE,{"disambiguationData":[OSD([sQuery(id+"F2.wireOp",EDGE,"E2.3.0.3")])],"isStart":true})});
            var Q469;
            Q469=makeQuery(id+"F3.boolean.opBoolean","INTERSECT",EDGE,{"derivedFrom":[makeQuery(id+"F1.opExtrude","CAP_FACE",FACE,{"disambiguationData":[OSD([sQuery(id+"F0.wireOp",EDGE,"E0.rect.bottom"),sQuery(id+"F0.wireOp",EDGE,"E0.rect.top"),sQuery(id+"F0.wireOp",EDGE,"E0.rect.left"),sQuery(id+"F0.wireOp",EDGE,"E0.rect.right")])],"isStart":true}),makeQuery(id+"F3.opExtrude","SWEPT_FACE",FACE,{"disambiguationData":[OSD([sQuery(id+"F2.wireOp",EDGE,"E1.right")])]})]});
            var Q470;
            Q470=makeQuery(id+"F3.boolean.opBoolean","INTERSECT",EDGE,{"derivedFrom":[makeQuery(id+"F1.opExtrude","CAP_FACE",FACE,{"disambiguationData":[OSD([sQuery(id+"F0.wireOp",EDGE,"E0.rect.bottom"),sQuery(id+"F0.wireOp",EDGE,"E0.rect.top"),sQuery(id+"F0.wireOp",EDGE,"E0.rect.left"),sQuery(id+"F0.wireOp",EDGE,"E0.rect.right")])],"isStart":true}),makeQuery(id+"F3.opExtrude","SWEPT_FACE",FACE,{"disambiguationData":[OSD([sQuery(id+"F2.wireOp",EDGE,"E2.3.1.3")])]})]});
            var Q471;
            Q471=makeQuery(id+"F3.boolean.opBoolean","INTERSECT",EDGE,{"derivedFrom":[makeQuery(id+"F1.opExtrude","CAP_FACE",FACE,{"disambiguationData":[OSD([sQuery(id+"F0.wireOp",EDGE,"E0.rect.bottom"),sQuery(id+"F0.wireOp",EDGE,"E0.rect.top"),sQuery(id+"F0.wireOp",EDGE,"E0.rect.left"),sQuery(id+"F0.wireOp",EDGE,"E0.rect.right")])],"isStart":true}),makeQuery(id+"F3.opExtrude","SWEPT_FACE",FACE,{"disambiguationData":[OSD([sQuery(id+"F2.wireOp",EDGE,"E2.4.0.3")])]})]});
            var Q472;
            Q472=makeQuery(id+"F3.boolean.opBoolean","COPY",EDGE,{"derivedFrom":makeQuery(id+"F3.opExtrude","SWEPT_EDGE",EDGE,{"disambiguationData":[OSD([sQuery(id+"F2.wireOp",EDGE,"E2.1.2.0"),sQuery(id+"F2.wireOp",EDGE,"E2.1.2.2")])]})});
            var Q473;
            Q473=makeQuery(id+"F3.boolean.opBoolean","COPY",EDGE,{"derivedFrom":makeQuery(id+"F3.opExtrude","SWEPT_EDGE",EDGE,{"disambiguationData":[OSD([sQuery(id+"F2.wireOp",EDGE,"E2.4.3.0"),sQuery(id+"F2.wireOp",EDGE,"E2.4.3.2")])]})});
            var Q474;
            Q474=makeQuery(id+"F3.boolean.opBoolean","COPY",EDGE,{"derivedFrom":makeQuery(id+"F3.opExtrude","SWEPT_EDGE",EDGE,{"disambiguationData":[OSD([sQuery(id+"F2.wireOp",EDGE,"E2.3.0.0"),sQuery(id+"F2.wireOp",EDGE,"E2.3.0.2")])]})});
            var Q475;
            Q475=makeQuery(id+"F3.boolean.opBoolean","COPY",EDGE,{"derivedFrom":makeQuery(id+"F3.opExtrude","SWEPT_EDGE",EDGE,{"disambiguationData":[OSD([sQuery(id+"F2.wireOp",EDGE,"E2.2.1.0"),sQuery(id+"F2.wireOp",EDGE,"E2.2.1.2")])]})});
            var Q476;
            Q476=makeQuery(id+"F3.boolean.opBoolean","COPY",EDGE,{"derivedFrom":makeQuery(id+"F3.opExtrude","CAP_EDGE",EDGE,{"disambiguationData":[OSD([sQuery(id+"F2.wireOp",EDGE,"E1.bottom")])],"isStart":true})});
            var Q477;
            Q477=makeQuery(id+"F3.boolean.opBoolean","COPY",EDGE,{"derivedFrom":makeQuery(id+"F3.opExtrude","SWEPT_EDGE",EDGE,{"disambiguationData":[OSD([sQuery(id+"F2.wireOp",EDGE,"E2.5.2.0"),sQuery(id+"F2.wireOp",EDGE,"E2.5.2.2")])]})});
            var Q478;
            Q478=makeQuery(id+"F3.boolean.opBoolean","COPY",EDGE,{"derivedFrom":makeQuery(id+"F3.opExtrude","CAP_EDGE",EDGE,{"disambiguationData":[OSD([sQuery(id+"F2.wireOp",EDGE,"E2.4.0.0")])],"isStart":true})});
            var Q479;
            Q479=makeQuery(id+"F3.boolean.opBoolean","COPY",EDGE,{"derivedFrom":makeQuery(id+"F3.opExtrude","CAP_EDGE",EDGE,{"disambiguationData":[OSD([sQuery(id+"F2.wireOp",EDGE,"E2.3.1.0")])],"isStart":true})});
            var Q480;
            Q480=makeQuery(id+"F3.boolean.opBoolean","INTERSECT",EDGE,{"derivedFrom":[makeQuery(id+"F1.opExtrude","CAP_FACE",FACE,{"disambiguationData":[OSD([sQuery(id+"F0.wireOp",EDGE,"E0.rect.bottom"),sQuery(id+"F0.wireOp",EDGE,"E0.rect.top"),sQuery(id+"F0.wireOp",EDGE,"E0.rect.left"),sQuery(id+"F0.wireOp",EDGE,"E0.rect.right")])],"isStart":true}),makeQuery(id+"F3.opExtrude","SWEPT_FACE",FACE,{"disambiguationData":[OSD([sQuery(id+"F2.wireOp",EDGE,"E2.0.1.0")])]})]});
            var Q481;
            Q481=makeQuery(id+"F3.boolean.opBoolean","INTERSECT",EDGE,{"derivedFrom":[makeQuery(id+"F1.opExtrude","CAP_FACE",FACE,{"disambiguationData":[OSD([sQuery(id+"F0.wireOp",EDGE,"E0.rect.bottom"),sQuery(id+"F0.wireOp",EDGE,"E0.rect.top"),sQuery(id+"F0.wireOp",EDGE,"E0.rect.left"),sQuery(id+"F0.wireOp",EDGE,"E0.rect.right")])],"isStart":true}),makeQuery(id+"F3.opExtrude","SWEPT_FACE",FACE,{"disambiguationData":[OSD([sQuery(id+"F2.wireOp",EDGE,"E2.3.2.0")])]})]});
            var Q482;
            Q482=makeQuery(id+"F3.boolean.opBoolean","INTERSECT",EDGE,{"derivedFrom":[makeQuery(id+"F1.opExtrude","CAP_FACE",FACE,{"disambiguationData":[OSD([sQuery(id+"F0.wireOp",EDGE,"E0.rect.bottom"),sQuery(id+"F0.wireOp",EDGE,"E0.rect.top"),sQuery(id+"F0.wireOp",EDGE,"E0.rect.left"),sQuery(id+"F0.wireOp",EDGE,"E0.rect.right")])],"isStart":true}),makeQuery(id+"F3.opExtrude","SWEPT_FACE",FACE,{"disambiguationData":[OSD([sQuery(id+"F2.wireOp",EDGE,"E2.1.0.0")])]})]});
            var Q483;
            Q483=makeQuery(id+"F3.boolean.opBoolean","INTERSECT",EDGE,{"derivedFrom":[makeQuery(id+"F1.opExtrude","CAP_FACE",FACE,{"disambiguationData":[OSD([sQuery(id+"F0.wireOp",EDGE,"E0.rect.bottom"),sQuery(id+"F0.wireOp",EDGE,"E0.rect.top"),sQuery(id+"F0.wireOp",EDGE,"E0.rect.left"),sQuery(id+"F0.wireOp",EDGE,"E0.rect.right")])],"isStart":true}),makeQuery(id+"F3.opExtrude","SWEPT_FACE",FACE,{"disambiguationData":[OSD([sQuery(id+"F2.wireOp",EDGE,"E2.4.1.0")])]})]});
            var Q484;
            Q484=makeQuery(id+"F3.boolean.opBoolean","COPY",EDGE,{"derivedFrom":makeQuery(id+"F3.opExtrude","SWEPT_EDGE",EDGE,{"disambiguationData":[OSD([sQuery(id+"F2.wireOp",EDGE,"E2.1.0.1"),sQuery(id+"F2.wireOp",EDGE,"E2.1.0.3")])]})});
            var Q485;
            Q485=makeQuery(id+"F3.boolean.opBoolean","INTERSECT",EDGE,{"derivedFrom":[makeQuery(id+"F1.opExtrude","CAP_FACE",FACE,{"disambiguationData":[OSD([sQuery(id+"F0.wireOp",EDGE,"E0.rect.bottom"),sQuery(id+"F0.wireOp",EDGE,"E0.rect.top"),sQuery(id+"F0.wireOp",EDGE,"E0.rect.left"),sQuery(id+"F0.wireOp",EDGE,"E0.rect.right")])],"isStart":true}),makeQuery(id+"F3.opExtrude","SWEPT_FACE",FACE,{"disambiguationData":[OSD([sQuery(id+"F2.wireOp",EDGE,"E2.4.1.2")])]})]});
            var Q486;
            Q486=makeQuery(id+"F3.boolean.opBoolean","INTERSECT",EDGE,{"derivedFrom":[makeQuery(id+"F1.opExtrude","CAP_FACE",FACE,{"disambiguationData":[OSD([sQuery(id+"F0.wireOp",EDGE,"E0.rect.bottom"),sQuery(id+"F0.wireOp",EDGE,"E0.rect.top"),sQuery(id+"F0.wireOp",EDGE,"E0.rect.left"),sQuery(id+"F0.wireOp",EDGE,"E0.rect.right")])],"isStart":true}),makeQuery(id+"F3.opExtrude","SWEPT_FACE",FACE,{"disambiguationData":[OSD([sQuery(id+"F2.wireOp",EDGE,"E2.3.2.2")])]})]});
            var Q487;
            Q487=makeQuery(id+"F3.boolean.opBoolean","INTERSECT",EDGE,{"derivedFrom":[makeQuery(id+"F1.opExtrude","CAP_FACE",FACE,{"disambiguationData":[OSD([sQuery(id+"F0.wireOp",EDGE,"E0.rect.bottom"),sQuery(id+"F0.wireOp",EDGE,"E0.rect.top"),sQuery(id+"F0.wireOp",EDGE,"E0.rect.left"),sQuery(id+"F0.wireOp",EDGE,"E0.rect.right")])],"isStart":true}),makeQuery(id+"F3.opExtrude","SWEPT_FACE",FACE,{"disambiguationData":[OSD([sQuery(id+"F2.wireOp",EDGE,"E2.2.3.2")])]})]});
            var Q488;
            Q488=makeQuery(id+"F3.boolean.opBoolean","INTERSECT",EDGE,{"derivedFrom":[makeQuery(id+"F1.opExtrude","CAP_FACE",FACE,{"disambiguationData":[OSD([sQuery(id+"F0.wireOp",EDGE,"E0.rect.bottom"),sQuery(id+"F0.wireOp",EDGE,"E0.rect.top"),sQuery(id+"F0.wireOp",EDGE,"E0.rect.left"),sQuery(id+"F0.wireOp",EDGE,"E0.rect.right")])],"isStart":true}),makeQuery(id+"F3.opExtrude","SWEPT_FACE",FACE,{"disambiguationData":[OSD([sQuery(id+"F2.wireOp",EDGE,"E2.1.4.2")])]})]});
            var Q489;
            Q489=makeQuery(id+"F3.boolean.opBoolean","INTERSECT",EDGE,{"derivedFrom":[makeQuery(id+"F1.opExtrude","CAP_FACE",FACE,{"disambiguationData":[OSD([sQuery(id+"F0.wireOp",EDGE,"E0.rect.bottom"),sQuery(id+"F0.wireOp",EDGE,"E0.rect.top"),sQuery(id+"F0.wireOp",EDGE,"E0.rect.left"),sQuery(id+"F0.wireOp",EDGE,"E0.rect.right")])],"isStart":true}),makeQuery(id+"F3.opExtrude","SWEPT_FACE",FACE,{"disambiguationData":[OSD([sQuery(id+"F2.wireOp",EDGE,"E2.5.4.2")])]})]});
            var Q490;
            Q490=makeQuery(id+"F3.boolean.opBoolean","COPY",EDGE,{"derivedFrom":makeQuery(id+"F3.opExtrude","SWEPT_EDGE",EDGE,{"disambiguationData":[OSD([sQuery(id+"F2.wireOp",EDGE,"E2.4.1.1"),sQuery(id+"F2.wireOp",EDGE,"E2.4.1.3")])]})});
            var Q491;
            Q491=makeQuery(id+"F3.boolean.opBoolean","COPY",EDGE,{"derivedFrom":makeQuery(id+"F3.opExtrude","SWEPT_EDGE",EDGE,{"disambiguationData":[OSD([sQuery(id+"F2.wireOp",EDGE,"E2.3.2.1"),sQuery(id+"F2.wireOp",EDGE,"E2.3.2.3")])]})});
            var Q492;
            Q492=makeQuery(id+"F3.boolean.opBoolean","COPY",EDGE,{"derivedFrom":makeQuery(id+"F3.opExtrude","SWEPT_EDGE",EDGE,{"disambiguationData":[OSD([sQuery(id+"F2.wireOp",EDGE,"E2.2.3.1"),sQuery(id+"F2.wireOp",EDGE,"E2.2.3.3")])]})});
            var Q493;
            Q493=makeQuery(id+"F3.boolean.opBoolean","COPY",EDGE,{"derivedFrom":makeQuery(id+"F3.opExtrude","SWEPT_EDGE",EDGE,{"disambiguationData":[OSD([sQuery(id+"F2.wireOp",EDGE,"E2.1.4.1"),sQuery(id+"F2.wireOp",EDGE,"E2.1.4.3")])]})});
            var Q494;
            Q494=makeQuery(id+"F3.boolean.opBoolean","COPY",EDGE,{"derivedFrom":makeQuery(id+"F3.opExtrude","CAP_EDGE",EDGE,{"disambiguationData":[OSD([sQuery(id+"F2.wireOp",EDGE,"E2.0.2.3")])],"isStart":true})});
            var Q495;
            Q495=makeQuery(id+"F3.boolean.opBoolean","COPY",EDGE,{"derivedFrom":makeQuery(id+"F3.opExtrude","SWEPT_EDGE",EDGE,{"disambiguationData":[OSD([sQuery(id+"F2.wireOp",EDGE,"E2.2.1.1"),sQuery(id+"F2.wireOp",EDGE,"E2.2.1.2")])]})});
            var Q496;
            Q496=makeQuery(id+"F3.boolean.opBoolean","COPY",EDGE,{"derivedFrom":makeQuery(id+"F3.opExtrude","SWEPT_EDGE",EDGE,{"disambiguationData":[OSD([sQuery(id+"F2.wireOp",EDGE,"E2.5.4.1"),sQuery(id+"F2.wireOp",EDGE,"E2.5.4.3")])]})});
            var Q497;
            Q497=makeQuery(id+"F3.boolean.opBoolean","COPY",EDGE,{"derivedFrom":makeQuery(id+"F3.opExtrude","SWEPT_EDGE",EDGE,{"disambiguationData":[OSD([sQuery(id+"F2.wireOp",EDGE,"E2.1.2.1"),sQuery(id+"F2.wireOp",EDGE,"E2.1.2.2")])]})});
            var Q498;
            Q498=makeQuery(id+"F3.boolean.opBoolean","COPY",EDGE,{"derivedFrom":makeQuery(id+"F3.opExtrude","SWEPT_EDGE",EDGE,{"disambiguationData":[OSD([sQuery(id+"F2.wireOp",EDGE,"E2.5.2.1"),sQuery(id+"F2.wireOp",EDGE,"E2.5.2.2")])]})});
            var Q499;
            Q499=makeQuery(id+"F3.boolean.opBoolean","COPY",EDGE,{"derivedFrom":makeQuery(id+"F3.opExtrude","CAP_EDGE",EDGE,{"disambiguationData":[OSD([sQuery(id+"F2.wireOp",EDGE,"E2.3.3.3")])],"isStart":true})});
            var Q500;
            Q500=makeQuery(id+"F3.boolean.opBoolean","COPY",EDGE,{"derivedFrom":makeQuery(id+"F3.opExtrude","SWEPT_EDGE",EDGE,{"disambiguationData":[OSD([sQuery(id+"F2.wireOp",EDGE,"E2.4.3.1"),sQuery(id+"F2.wireOp",EDGE,"E2.4.3.2")])]})});
            var Q501;
            Q501=makeQuery(id+"F3.boolean.opBoolean","COPY",EDGE,{"derivedFrom":makeQuery(id+"F3.opExtrude","SWEPT_EDGE",EDGE,{"disambiguationData":[OSD([sQuery(id+"F2.wireOp",EDGE,"E2.3.4.1"),sQuery(id+"F2.wireOp",EDGE,"E2.3.4.2")])]})});
            var Q502;
            Q502=makeQuery(id+"F3.boolean.opBoolean","INTERSECT",EDGE,{"derivedFrom":[makeQuery(id+"F1.opExtrude","CAP_FACE",FACE,{"disambiguationData":[OSD([sQuery(id+"F0.wireOp",EDGE,"E0.rect.bottom"),sQuery(id+"F0.wireOp",EDGE,"E0.rect.top"),sQuery(id+"F0.wireOp",EDGE,"E0.rect.left"),sQuery(id+"F0.wireOp",EDGE,"E0.rect.right")])],"isStart":true}),makeQuery(id+"F3.opExtrude","SWEPT_FACE",FACE,{"disambiguationData":[OSD([sQuery(id+"F2.wireOp",EDGE,"E2.3.0.3")])]})]});
            var Q503;
            Q503=makeQuery(id+"F3.boolean.opBoolean","INTERSECT",EDGE,{"derivedFrom":[makeQuery(id+"F1.opExtrude","CAP_FACE",FACE,{"disambiguationData":[OSD([sQuery(id+"F0.wireOp",EDGE,"E0.rect.bottom"),sQuery(id+"F0.wireOp",EDGE,"E0.rect.top"),sQuery(id+"F0.wireOp",EDGE,"E0.rect.left"),sQuery(id+"F0.wireOp",EDGE,"E0.rect.right")])],"isStart":true}),makeQuery(id+"F3.opExtrude","SWEPT_FACE",FACE,{"disambiguationData":[OSD([sQuery(id+"F2.wireOp",EDGE,"E2.2.1.3")])]})]});
            var Q504;
            Q504=makeQuery(id+"F3.boolean.opBoolean","INTERSECT",EDGE,{"derivedFrom":[makeQuery(id+"F1.opExtrude","CAP_FACE",FACE,{"disambiguationData":[OSD([sQuery(id+"F0.wireOp",EDGE,"E0.rect.bottom"),sQuery(id+"F0.wireOp",EDGE,"E0.rect.top"),sQuery(id+"F0.wireOp",EDGE,"E0.rect.left"),sQuery(id+"F0.wireOp",EDGE,"E0.rect.right")])],"isStart":true}),makeQuery(id+"F3.opExtrude","SWEPT_FACE",FACE,{"disambiguationData":[OSD([sQuery(id+"F2.wireOp",EDGE,"E2.1.2.3")])]})]});
            var Q505;
            Q505=makeQuery(id+"F3.boolean.opBoolean","COPY",EDGE,{"derivedFrom":makeQuery(id+"F3.opExtrude","SWEPT_EDGE",EDGE,{"disambiguationData":[OSD([sQuery(id+"F2.wireOp",EDGE,"E2.3.0.1"),sQuery(id+"F2.wireOp",EDGE,"E2.3.0.2")])]})});
            var Q506;
            Q506=makeQuery(id+"F3.boolean.opBoolean","INTERSECT",EDGE,{"derivedFrom":[makeQuery(id+"F1.opExtrude","CAP_FACE",FACE,{"disambiguationData":[OSD([sQuery(id+"F0.wireOp",EDGE,"E0.rect.bottom"),sQuery(id+"F0.wireOp",EDGE,"E0.rect.top"),sQuery(id+"F0.wireOp",EDGE,"E0.rect.left"),sQuery(id+"F0.wireOp",EDGE,"E0.rect.right")])],"isStart":true}),makeQuery(id+"F3.opExtrude","SWEPT_FACE",FACE,{"disambiguationData":[OSD([sQuery(id+"F2.wireOp",EDGE,"E2.1.0.2")])]})]});
            var Q507;
            Q507=makeQuery(id+"F3.boolean.opBoolean","INTERSECT",EDGE,{"derivedFrom":[makeQuery(id+"F1.opExtrude","CAP_FACE",FACE,{"disambiguationData":[OSD([sQuery(id+"F0.wireOp",EDGE,"E0.rect.bottom"),sQuery(id+"F0.wireOp",EDGE,"E0.rect.top"),sQuery(id+"F0.wireOp",EDGE,"E0.rect.left"),sQuery(id+"F0.wireOp",EDGE,"E0.rect.right")])],"isStart":true}),makeQuery(id+"F3.opExtrude","SWEPT_FACE",FACE,{"disambiguationData":[OSD([sQuery(id+"F2.wireOp",EDGE,"E2.0.1.2")])]})]});
            var Q508;
            Q508=makeQuery(id+"F3.boolean.opBoolean","COPY",EDGE,{"derivedFrom":makeQuery(id+"F3.opExtrude","SWEPT_EDGE",EDGE,{"disambiguationData":[OSD([sQuery(id+"F2.wireOp",EDGE,"E2.1.1.0"),sQuery(id+"F2.wireOp",EDGE,"E2.1.1.2")])]})});
            var Q509;
            Q509=makeQuery(id+"F3.boolean.opBoolean","COPY",EDGE,{"derivedFrom":makeQuery(id+"F3.opExtrude","SWEPT_EDGE",EDGE,{"disambiguationData":[OSD([sQuery(id+"F2.wireOp",EDGE,"E2.4.2.0"),sQuery(id+"F2.wireOp",EDGE,"E2.4.2.2")])]})});
            var Q510;
            Q510=makeQuery(id+"F3.boolean.opBoolean","COPY",EDGE,{"derivedFrom":makeQuery(id+"F3.opExtrude","SWEPT_EDGE",EDGE,{"disambiguationData":[OSD([sQuery(id+"F2.wireOp",EDGE,"E2.2.0.0"),sQuery(id+"F2.wireOp",EDGE,"E2.2.0.2")])]})});
            var Q511;
            Q511=makeQuery(id+"F3.boolean.opBoolean","COPY",EDGE,{"derivedFrom":makeQuery(id+"F3.opExtrude","SWEPT_EDGE",EDGE,{"disambiguationData":[OSD([sQuery(id+"F2.wireOp",EDGE,"E2.2.1.1"),sQuery(id+"F2.wireOp",EDGE,"E2.2.1.3")])]})});
            var Q512;
            Q512=makeQuery(id+"F3.boolean.opBoolean","COPY",EDGE,{"derivedFrom":makeQuery(id+"F3.opExtrude","SWEPT_EDGE",EDGE,{"disambiguationData":[OSD([sQuery(id+"F2.wireOp",EDGE,"E2.5.2.1"),sQuery(id+"F2.wireOp",EDGE,"E2.5.2.3")])]})});
            var Q513;
            Q513=makeQuery(id+"F3.boolean.opBoolean","COPY",EDGE,{"derivedFrom":makeQuery(id+"F3.opExtrude","SWEPT_EDGE",EDGE,{"disambiguationData":[OSD([sQuery(id+"F2.wireOp",EDGE,"E2.4.3.1"),sQuery(id+"F2.wireOp",EDGE,"E2.4.3.3")])]})});
            var Q514;
            Q514=makeQuery(id+"F3.boolean.opBoolean","COPY",EDGE,{"derivedFrom":makeQuery(id+"F3.opExtrude","SWEPT_EDGE",EDGE,{"disambiguationData":[OSD([sQuery(id+"F2.wireOp",EDGE,"E2.3.4.1"),sQuery(id+"F2.wireOp",EDGE,"E2.3.4.3")])]})});
            var Q515;
            Q515=makeQuery(id+"F3.boolean.opBoolean","COPY",EDGE,{"derivedFrom":makeQuery(id+"F3.opExtrude","SWEPT_EDGE",EDGE,{"disambiguationData":[OSD([sQuery(id+"F2.wireOp",EDGE,"E2.3.0.1"),sQuery(id+"F2.wireOp",EDGE,"E2.3.0.3")])]})});
            var Q516;
            Q516=makeQuery(id+"F3.boolean.opBoolean","COPY",EDGE,{"derivedFrom":makeQuery(id+"F3.opExtrude","CAP_EDGE",EDGE,{"disambiguationData":[OSD([sQuery(id+"F2.wireOp",EDGE,"E1.right")])],"isStart":true})});
            var Q517;
            Q517=makeQuery(id+"F3.boolean.opBoolean","COPY",EDGE,{"derivedFrom":makeQuery(id+"F3.opExtrude","CAP_EDGE",EDGE,{"disambiguationData":[OSD([sQuery(id+"F2.wireOp",EDGE,"E2.4.0.3")])],"isStart":true})});
            var Q518;
            Q518=makeQuery(id+"F3.boolean.opBoolean","COPY",EDGE,{"derivedFrom":makeQuery(id+"F3.opExtrude","CAP_EDGE",EDGE,{"disambiguationData":[OSD([sQuery(id+"F2.wireOp",EDGE,"E2.3.1.3")])],"isStart":true})});
            var Q519;
            Q519=makeQuery(id+"F3.boolean.opBoolean","INTERSECT",EDGE,{"derivedFrom":[makeQuery(id+"F1.opExtrude","CAP_FACE",FACE,{"disambiguationData":[OSD([sQuery(id+"F0.wireOp",EDGE,"E0.rect.bottom"),sQuery(id+"F0.wireOp",EDGE,"E0.rect.top"),sQuery(id+"F0.wireOp",EDGE,"E0.rect.left"),sQuery(id+"F0.wireOp",EDGE,"E0.rect.right")])],"isStart":true}),makeQuery(id+"F3.opExtrude","SWEPT_FACE",FACE,{"disambiguationData":[OSD([sQuery(id+"F2.wireOp",EDGE,"E2.1.0.3")])]})]});
            var Q520;
            Q520=makeQuery(id+"F3.boolean.opBoolean","INTERSECT",EDGE,{"derivedFrom":[makeQuery(id+"F1.opExtrude","CAP_FACE",FACE,{"disambiguationData":[OSD([sQuery(id+"F0.wireOp",EDGE,"E0.rect.bottom"),sQuery(id+"F0.wireOp",EDGE,"E0.rect.top"),sQuery(id+"F0.wireOp",EDGE,"E0.rect.left"),sQuery(id+"F0.wireOp",EDGE,"E0.rect.right")])],"isStart":true}),makeQuery(id+"F3.opExtrude","SWEPT_FACE",FACE,{"disambiguationData":[OSD([sQuery(id+"F2.wireOp",EDGE,"E2.0.1.3")])]})]});
            var Q521;
            Q521=makeQuery(id+"F3.boolean.opBoolean","INTERSECT",EDGE,{"derivedFrom":[makeQuery(id+"F1.opExtrude","CAP_FACE",FACE,{"disambiguationData":[OSD([sQuery(id+"F0.wireOp",EDGE,"E0.rect.bottom"),sQuery(id+"F0.wireOp",EDGE,"E0.rect.top"),sQuery(id+"F0.wireOp",EDGE,"E0.rect.left"),sQuery(id+"F0.wireOp",EDGE,"E0.rect.right")])],"isStart":true}),makeQuery(id+"F3.opExtrude","SWEPT_FACE",FACE,{"disambiguationData":[OSD([sQuery(id+"F2.wireOp",EDGE,"E2.4.1.3")])]})]});
            var Q522;
            Q522=makeQuery(id+"F3.boolean.opBoolean","INTERSECT",EDGE,{"derivedFrom":[makeQuery(id+"F1.opExtrude","CAP_FACE",FACE,{"disambiguationData":[OSD([sQuery(id+"F0.wireOp",EDGE,"E0.rect.bottom"),sQuery(id+"F0.wireOp",EDGE,"E0.rect.top"),sQuery(id+"F0.wireOp",EDGE,"E0.rect.left"),sQuery(id+"F0.wireOp",EDGE,"E0.rect.right")])],"isStart":true}),makeQuery(id+"F3.opExtrude","SWEPT_FACE",FACE,{"disambiguationData":[OSD([sQuery(id+"F2.wireOp",EDGE,"E2.3.2.3")])]})]});
            var Q523;
            Q523=makeQuery(id+"F3.boolean.opBoolean","COPY",EDGE,{"derivedFrom":makeQuery(id+"F3.opExtrude","SWEPT_EDGE",EDGE,{"disambiguationData":[OSD([sQuery(id+"F2.wireOp",EDGE,"E2.2.2.0"),sQuery(id+"F2.wireOp",EDGE,"E2.2.2.2")])]})});
            var Q524;
            Q524=makeQuery(id+"F3.boolean.opBoolean","COPY",EDGE,{"derivedFrom":makeQuery(id+"F3.opExtrude","SWEPT_EDGE",EDGE,{"disambiguationData":[OSD([sQuery(id+"F2.wireOp",EDGE,"E2.4.0.0"),sQuery(id+"F2.wireOp",EDGE,"E2.4.0.2")])]})});
            var Q525;
            Q525=makeQuery(id+"F3.boolean.opBoolean","COPY",EDGE,{"derivedFrom":makeQuery(id+"F3.opExtrude","SWEPT_EDGE",EDGE,{"disambiguationData":[OSD([sQuery(id+"F2.wireOp",EDGE,"E2.3.1.0"),sQuery(id+"F2.wireOp",EDGE,"E2.3.1.2")])]})});
            var Q526;
            Q526=makeQuery(id+"F3.boolean.opBoolean","COPY",EDGE,{"derivedFrom":makeQuery(id+"F3.opExtrude","CAP_EDGE",EDGE,{"disambiguationData":[OSD([sQuery(id+"F2.wireOp",EDGE,"E2.1.0.0")])],"isStart":true})});
            var Q527;
            Q527=makeQuery(id+"F3.boolean.opBoolean","COPY",EDGE,{"derivedFrom":makeQuery(id+"F3.opExtrude","CAP_EDGE",EDGE,{"disambiguationData":[OSD([sQuery(id+"F2.wireOp",EDGE,"E2.0.1.0")])],"isStart":true})});
            var Q528;
            Q528=makeQuery(id+"F3.boolean.opBoolean","COPY",EDGE,{"derivedFrom":makeQuery(id+"F3.opExtrude","SWEPT_EDGE",EDGE,{"disambiguationData":[OSD([sQuery(id+"F2.wireOp",EDGE,"E2.6.2.0"),sQuery(id+"F2.wireOp",EDGE,"E2.6.2.2")])]})});
            var Q529;
            Q529=makeQuery(id+"F3.boolean.opBoolean","COPY",EDGE,{"derivedFrom":makeQuery(id+"F3.opExtrude","CAP_EDGE",EDGE,{"disambiguationData":[OSD([sQuery(id+"F2.wireOp",EDGE,"E2.4.1.0")])],"isStart":true})});
            var Q530;
            Q530=makeQuery(id+"F3.boolean.opBoolean","COPY",EDGE,{"derivedFrom":makeQuery(id+"F3.opExtrude","CAP_EDGE",EDGE,{"disambiguationData":[OSD([sQuery(id+"F2.wireOp",EDGE,"E2.3.2.0")])],"isStart":true})});
            var Q531;
            Q531=makeQuery(id+"F3.boolean.opBoolean","INTERSECT",EDGE,{"derivedFrom":[makeQuery(id+"F1.opExtrude","CAP_FACE",FACE,{"disambiguationData":[OSD([sQuery(id+"F0.wireOp",EDGE,"E0.rect.bottom"),sQuery(id+"F0.wireOp",EDGE,"E0.rect.top"),sQuery(id+"F0.wireOp",EDGE,"E0.rect.left"),sQuery(id+"F0.wireOp",EDGE,"E0.rect.right")])],"isStart":true}),makeQuery(id+"F3.opExtrude","SWEPT_FACE",FACE,{"disambiguationData":[OSD([sQuery(id+"F2.wireOp",EDGE,"E2.1.1.0")])]})]});
            var Q532;
            Q532=makeQuery(id+"F3.boolean.opBoolean","INTERSECT",EDGE,{"derivedFrom":[makeQuery(id+"F1.opExtrude","CAP_FACE",FACE,{"disambiguationData":[OSD([sQuery(id+"F0.wireOp",EDGE,"E0.rect.bottom"),sQuery(id+"F0.wireOp",EDGE,"E0.rect.top"),sQuery(id+"F0.wireOp",EDGE,"E0.rect.left"),sQuery(id+"F0.wireOp",EDGE,"E0.rect.right")])],"isStart":true}),makeQuery(id+"F3.opExtrude","SWEPT_FACE",FACE,{"disambiguationData":[OSD([sQuery(id+"F2.wireOp",EDGE,"E2.0.2.0")])]})]});
            var Q533;
            Q533=makeQuery(id+"F3.boolean.opBoolean","INTERSECT",EDGE,{"derivedFrom":[makeQuery(id+"F1.opExtrude","CAP_FACE",FACE,{"disambiguationData":[OSD([sQuery(id+"F0.wireOp",EDGE,"E0.rect.bottom"),sQuery(id+"F0.wireOp",EDGE,"E0.rect.top"),sQuery(id+"F0.wireOp",EDGE,"E0.rect.left"),sQuery(id+"F0.wireOp",EDGE,"E0.rect.right")])],"isStart":true}),makeQuery(id+"F3.opExtrude","SWEPT_FACE",FACE,{"disambiguationData":[OSD([sQuery(id+"F2.wireOp",EDGE,"E2.4.2.0")])]})]});
            var Q534;
            Q534=makeQuery(id+"F3.boolean.opBoolean","INTERSECT",EDGE,{"derivedFrom":[makeQuery(id+"F1.opExtrude","CAP_FACE",FACE,{"disambiguationData":[OSD([sQuery(id+"F0.wireOp",EDGE,"E0.rect.bottom"),sQuery(id+"F0.wireOp",EDGE,"E0.rect.top"),sQuery(id+"F0.wireOp",EDGE,"E0.rect.left"),sQuery(id+"F0.wireOp",EDGE,"E0.rect.right")])],"isStart":true}),makeQuery(id+"F3.opExtrude","SWEPT_FACE",FACE,{"disambiguationData":[OSD([sQuery(id+"F2.wireOp",EDGE,"E2.3.3.0")])]})]});
            var Q535;
            Q535=makeQuery(id+"F3.boolean.opBoolean","INTERSECT",EDGE,{"derivedFrom":[makeQuery(id+"F1.opExtrude","CAP_FACE",FACE,{"disambiguationData":[OSD([sQuery(id+"F0.wireOp",EDGE,"E0.rect.bottom"),sQuery(id+"F0.wireOp",EDGE,"E0.rect.top"),sQuery(id+"F0.wireOp",EDGE,"E0.rect.left"),sQuery(id+"F0.wireOp",EDGE,"E0.rect.right")])],"isStart":true}),makeQuery(id+"F3.opExtrude","SWEPT_FACE",FACE,{"disambiguationData":[OSD([sQuery(id+"F2.wireOp",EDGE,"E2.2.0.0")])]})]});
            var Q536;
            Q536=makeQuery(id+"F3.boolean.opBoolean","INTERSECT",EDGE,{"derivedFrom":[makeQuery(id+"F1.opExtrude","CAP_FACE",FACE,{"disambiguationData":[OSD([sQuery(id+"F0.wireOp",EDGE,"E0.rect.bottom"),sQuery(id+"F0.wireOp",EDGE,"E0.rect.top"),sQuery(id+"F0.wireOp",EDGE,"E0.rect.left"),sQuery(id+"F0.wireOp",EDGE,"E0.rect.right")])],"isStart":true}),makeQuery(id+"F3.opExtrude","SWEPT_FACE",FACE,{"disambiguationData":[OSD([sQuery(id+"F2.wireOp",EDGE,"E2.5.1.0")])]})]});
            var Q537;
            Q537=makeQuery(id+"F3.boolean.opBoolean","COPY",EDGE,{"derivedFrom":makeQuery(id+"F3.opExtrude","SWEPT_EDGE",EDGE,{"disambiguationData":[OSD([sQuery(id+"F2.wireOp",EDGE,"E2.6.2.1"),sQuery(id+"F2.wireOp",EDGE,"E2.6.2.2")])]})});
            var Q538;
            Q538=makeQuery(id+"F3.boolean.opBoolean","INTERSECT",EDGE,{"derivedFrom":[makeQuery(id+"F1.opExtrude","CAP_FACE",FACE,{"disambiguationData":[OSD([sQuery(id+"F0.wireOp",EDGE,"E0.rect.bottom"),sQuery(id+"F0.wireOp",EDGE,"E0.rect.top"),sQuery(id+"F0.wireOp",EDGE,"E0.rect.left"),sQuery(id+"F0.wireOp",EDGE,"E0.rect.right")])],"isStart":true}),makeQuery(id+"F3.opExtrude","SWEPT_FACE",FACE,{"disambiguationData":[OSD([sQuery(id+"F2.wireOp",EDGE,"E2.1.1.2")])]})]});
            var Q539;
            Q539=makeQuery(id+"F3.boolean.opBoolean","INTERSECT",EDGE,{"derivedFrom":[makeQuery(id+"F1.opExtrude","CAP_FACE",FACE,{"disambiguationData":[OSD([sQuery(id+"F0.wireOp",EDGE,"E0.rect.bottom"),sQuery(id+"F0.wireOp",EDGE,"E0.rect.top"),sQuery(id+"F0.wireOp",EDGE,"E0.rect.left"),sQuery(id+"F0.wireOp",EDGE,"E0.rect.right")])],"isStart":true}),makeQuery(id+"F3.opExtrude","SWEPT_FACE",FACE,{"disambiguationData":[OSD([sQuery(id+"F2.wireOp",EDGE,"E2.4.2.2")])]})]});
            var Q540;
            Q540=makeQuery(id+"F3.boolean.opBoolean","INTERSECT",EDGE,{"derivedFrom":[makeQuery(id+"F1.opExtrude","CAP_FACE",FACE,{"disambiguationData":[OSD([sQuery(id+"F0.wireOp",EDGE,"E0.rect.bottom"),sQuery(id+"F0.wireOp",EDGE,"E0.rect.top"),sQuery(id+"F0.wireOp",EDGE,"E0.rect.left"),sQuery(id+"F0.wireOp",EDGE,"E0.rect.right")])],"isStart":true}),makeQuery(id+"F3.opExtrude","SWEPT_FACE",FACE,{"disambiguationData":[OSD([sQuery(id+"F2.wireOp",EDGE,"E2.3.3.2")])]})]});
            var Q541;
            Q541=makeQuery(id+"F3.boolean.opBoolean","INTERSECT",EDGE,{"derivedFrom":[makeQuery(id+"F1.opExtrude","CAP_FACE",FACE,{"disambiguationData":[OSD([sQuery(id+"F0.wireOp",EDGE,"E0.rect.bottom"),sQuery(id+"F0.wireOp",EDGE,"E0.rect.top"),sQuery(id+"F0.wireOp",EDGE,"E0.rect.left"),sQuery(id+"F0.wireOp",EDGE,"E0.rect.right")])],"isStart":true}),makeQuery(id+"F3.opExtrude","SWEPT_FACE",FACE,{"disambiguationData":[OSD([sQuery(id+"F2.wireOp",EDGE,"E2.2.0.2")])]})]});
            var Q542;
            Q542=makeQuery(id+"F3.boolean.opBoolean","COPY",EDGE,{"derivedFrom":makeQuery(id+"F3.opExtrude","SWEPT_EDGE",EDGE,{"disambiguationData":[OSD([sQuery(id+"F2.wireOp",EDGE,"E2.2.2.1"),sQuery(id+"F2.wireOp",EDGE,"E2.2.2.2")])]})});
            var Q543;
            Q543=makeQuery(id+"F3.boolean.opBoolean","COPY",EDGE,{"derivedFrom":makeQuery(id+"F3.opExtrude","SWEPT_EDGE",EDGE,{"disambiguationData":[OSD([sQuery(id+"F2.wireOp",EDGE,"E2.5.3.1"),sQuery(id+"F2.wireOp",EDGE,"E2.5.3.2")])]})});
            var Q544;
            Q544=makeQuery(id+"F3.boolean.opBoolean","COPY",EDGE,{"derivedFrom":makeQuery(id+"F3.opExtrude","SWEPT_EDGE",EDGE,{"disambiguationData":[OSD([sQuery(id+"F2.wireOp",EDGE,"E2.4.4.1"),sQuery(id+"F2.wireOp",EDGE,"E2.4.4.2")])]})});
            var Q545;
            Q545=makeQuery(id+"F3.boolean.opBoolean","COPY",EDGE,{"derivedFrom":makeQuery(id+"F3.opExtrude","SWEPT_EDGE",EDGE,{"disambiguationData":[OSD([sQuery(id+"F2.wireOp",EDGE,"E2.4.0.1"),sQuery(id+"F2.wireOp",EDGE,"E2.4.0.2")])]})});
            var Q546;
            Q546=makeQuery(id+"F3.boolean.opBoolean","COPY",EDGE,{"derivedFrom":makeQuery(id+"F3.opExtrude","CAP_EDGE",EDGE,{"disambiguationData":[OSD([sQuery(id+"F2.wireOp",EDGE,"E2.4.1.3")])],"isStart":true})});
            var Q547;
            Q547=makeQuery(id+"F3.boolean.opBoolean","INTERSECT",EDGE,{"derivedFrom":[makeQuery(id+"F1.opExtrude","CAP_FACE",FACE,{"disambiguationData":[OSD([sQuery(id+"F0.wireOp",EDGE,"E0.rect.bottom"),sQuery(id+"F0.wireOp",EDGE,"E0.rect.top"),sQuery(id+"F0.wireOp",EDGE,"E0.rect.left"),sQuery(id+"F0.wireOp",EDGE,"E0.rect.right")])],"isStart":true}),makeQuery(id+"F3.opExtrude","SWEPT_FACE",FACE,{"disambiguationData":[OSD([sQuery(id+"F2.wireOp",EDGE,"E2.0.2.3")])]})]});
            var Q548;
            Q548=makeQuery(id+"F3.boolean.opBoolean","INTERSECT",EDGE,{"derivedFrom":[makeQuery(id+"F1.opExtrude","CAP_FACE",FACE,{"disambiguationData":[OSD([sQuery(id+"F0.wireOp",EDGE,"E0.rect.bottom"),sQuery(id+"F0.wireOp",EDGE,"E0.rect.top"),sQuery(id+"F0.wireOp",EDGE,"E0.rect.left"),sQuery(id+"F0.wireOp",EDGE,"E0.rect.right")])],"isStart":true}),makeQuery(id+"F3.opExtrude","SWEPT_FACE",FACE,{"disambiguationData":[OSD([sQuery(id+"F2.wireOp",EDGE,"E2.4.2.3")])]})]});
            var Q549;
            Q549=makeQuery(id+"F1.opExtrude","SWEPT_EDGE",EDGE,{"disambiguationData":[OSD([sQuery(id+"F0.wireOp",EDGE,"E0.rect.bottom"),sQuery(id+"F0.wireOp",EDGE,"E0.rect.right")])]});
            var Q550;
            Q550=makeQuery(id+"F3.boolean.opBoolean","INTERSECT",EDGE,{"derivedFrom":[makeQuery(id+"F1.opExtrude","CAP_FACE",FACE,{"disambiguationData":[OSD([sQuery(id+"F0.wireOp",EDGE,"E0.rect.bottom"),sQuery(id+"F0.wireOp",EDGE,"E0.rect.top"),sQuery(id+"F0.wireOp",EDGE,"E0.rect.left"),sQuery(id+"F0.wireOp",EDGE,"E0.rect.right")])],"isStart":true}),makeQuery(id+"F3.opExtrude","SWEPT_FACE",FACE,{"disambiguationData":[OSD([sQuery(id+"F2.wireOp",EDGE,"E2.2.0.3")])]})]});
            var Q551;
            Q551=makeQuery(id+"F3.boolean.opBoolean","INTERSECT",EDGE,{"derivedFrom":[makeQuery(id+"F1.opExtrude","CAP_FACE",FACE,{"disambiguationData":[OSD([sQuery(id+"F0.wireOp",EDGE,"E0.rect.bottom"),sQuery(id+"F0.wireOp",EDGE,"E0.rect.top"),sQuery(id+"F0.wireOp",EDGE,"E0.rect.left"),sQuery(id+"F0.wireOp",EDGE,"E0.rect.right")])],"isStart":true}),makeQuery(id+"F3.opExtrude","SWEPT_FACE",FACE,{"disambiguationData":[OSD([sQuery(id+"F2.wireOp",EDGE,"E2.5.1.3")])]})]});
            var Q552;
            Q552=makeQuery(id+"F1.opExtrude","SWEPT_EDGE",EDGE,{"disambiguationData":[OSD([sQuery(id+"F0.wireOp",EDGE,"E0.rect.top"),sQuery(id+"F0.wireOp",EDGE,"E0.rect.right")])]});
            var Q553;
            Q553=makeQuery(id+"F3.boolean.opBoolean","COPY",EDGE,{"derivedFrom":makeQuery(id+"F3.opExtrude","SWEPT_EDGE",EDGE,{"disambiguationData":[OSD([sQuery(id+"F2.wireOp",EDGE,"E2.0.4.1"),sQuery(id+"F2.wireOp",EDGE,"E2.0.4.3")])]})});
            var Q554;
            Q554=makeQuery(id+"F3.boolean.opBoolean","COPY",EDGE,{"derivedFrom":makeQuery(id+"F3.opExtrude","SWEPT_EDGE",EDGE,{"disambiguationData":[OSD([sQuery(id+"F2.wireOp",EDGE,"E2.5.3.1"),sQuery(id+"F2.wireOp",EDGE,"E2.5.3.3")])]})});
            var Q555;
            Q555=makeQuery(id+"F3.boolean.opBoolean","COPY",EDGE,{"derivedFrom":makeQuery(id+"F3.opExtrude","SWEPT_EDGE",EDGE,{"disambiguationData":[OSD([sQuery(id+"F2.wireOp",EDGE,"E2.4.4.1"),sQuery(id+"F2.wireOp",EDGE,"E2.4.4.3")])]})});
            var Q556;
            Q556=makeQuery(id+"F3.boolean.opBoolean","COPY",EDGE,{"derivedFrom":makeQuery(id+"F3.opExtrude","SWEPT_EDGE",EDGE,{"disambiguationData":[OSD([sQuery(id+"F2.wireOp",EDGE,"E2.4.0.1"),sQuery(id+"F2.wireOp",EDGE,"E2.4.0.3")])]})});
            var Q557;
            Q557=makeQuery(id+"F3.boolean.opBoolean","COPY",EDGE,{"derivedFrom":makeQuery(id+"F3.opExtrude","SWEPT_EDGE",EDGE,{"disambiguationData":[OSD([sQuery(id+"F2.wireOp",EDGE,"E2.3.1.1"),sQuery(id+"F2.wireOp",EDGE,"E2.3.1.3")])]})});
            var Q558;
            Q558=makeQuery(id+"F3.boolean.opBoolean","COPY",EDGE,{"derivedFrom":makeQuery(id+"F3.opExtrude","CAP_EDGE",EDGE,{"disambiguationData":[OSD([sQuery(id+"F2.wireOp",EDGE,"E2.0.1.3")])],"isStart":true})});
            var Q559;
            Q559=makeQuery(id+"F3.boolean.opBoolean","INTERSECT",EDGE,{"derivedFrom":[makeQuery(id+"F1.opExtrude","CAP_FACE",FACE,{"disambiguationData":[OSD([sQuery(id+"F0.wireOp",EDGE,"E0.rect.bottom"),sQuery(id+"F0.wireOp",EDGE,"E0.rect.top"),sQuery(id+"F0.wireOp",EDGE,"E0.rect.left"),sQuery(id+"F0.wireOp",EDGE,"E0.rect.right")])],"isStart":true}),makeQuery(id+"F3.opExtrude","SWEPT_FACE",FACE,{"disambiguationData":[OSD([sQuery(id+"F2.wireOp",EDGE,"E2.1.2.0")])]})]});
            var Q560;
            Q560=makeQuery(id+"F3.boolean.opBoolean","COPY",EDGE,{"derivedFrom":makeQuery(id+"F3.opExtrude","SWEPT_EDGE",EDGE,{"disambiguationData":[OSD([sQuery(id+"F2.wireOp",EDGE,"E1.bottom"),sQuery(id+"F2.wireOp",EDGE,"E1.left")])]})});
            var Q561;
            Q561=makeQuery(id+"F3.boolean.opBoolean","INTERSECT",EDGE,{"derivedFrom":[makeQuery(id+"F1.opExtrude","CAP_FACE",FACE,{"disambiguationData":[OSD([sQuery(id+"F0.wireOp",EDGE,"E0.rect.bottom"),sQuery(id+"F0.wireOp",EDGE,"E0.rect.top"),sQuery(id+"F0.wireOp",EDGE,"E0.rect.left"),sQuery(id+"F0.wireOp",EDGE,"E0.rect.right")])],"isStart":true}),makeQuery(id+"F3.opExtrude","SWEPT_FACE",FACE,{"disambiguationData":[OSD([sQuery(id+"F2.wireOp",EDGE,"E2.3.0.0")])]})]});
            var Q562;
            Q562=makeQuery(id+"F3.boolean.opBoolean","INTERSECT",EDGE,{"derivedFrom":[makeQuery(id+"F1.opExtrude","CAP_FACE",FACE,{"disambiguationData":[OSD([sQuery(id+"F0.wireOp",EDGE,"E0.rect.bottom"),sQuery(id+"F0.wireOp",EDGE,"E0.rect.top"),sQuery(id+"F0.wireOp",EDGE,"E0.rect.left"),sQuery(id+"F0.wireOp",EDGE,"E0.rect.right")])],"isStart":true}),makeQuery(id+"F3.opExtrude","SWEPT_FACE",FACE,{"disambiguationData":[OSD([sQuery(id+"F2.wireOp",EDGE,"E2.2.1.0")])]})]});
            var Q563;
            Q563=makeQuery(id+"F3.boolean.opBoolean","COPY",EDGE,{"derivedFrom":makeQuery(id+"F3.opExtrude","SWEPT_EDGE",EDGE,{"disambiguationData":[OSD([sQuery(id+"F2.wireOp",EDGE,"E1.top"),sQuery(id+"F2.wireOp",EDGE,"E1.left")])]})});
            var Q564;
            Q564=makeQuery(id+"F3.boolean.opBoolean","INTERSECT",EDGE,{"derivedFrom":[makeQuery(id+"F1.opExtrude","CAP_FACE",FACE,{"disambiguationData":[OSD([sQuery(id+"F0.wireOp",EDGE,"E0.rect.bottom"),sQuery(id+"F0.wireOp",EDGE,"E0.rect.top"),sQuery(id+"F0.wireOp",EDGE,"E0.rect.left"),sQuery(id+"F0.wireOp",EDGE,"E0.rect.right")])],"isStart":true}),makeQuery(id+"F3.opExtrude","SWEPT_FACE",FACE,{"disambiguationData":[OSD([sQuery(id+"F2.wireOp",EDGE,"E2.5.2.0")])]})]});
            var Q565;
            Q565=makeQuery(id+"F3.boolean.opBoolean","COPY",EDGE,{"derivedFrom":makeQuery(id+"F3.opExtrude","SWEPT_EDGE",EDGE,{"disambiguationData":[OSD([sQuery(id+"F2.wireOp",EDGE,"E1.top"),sQuery(id+"F2.wireOp",EDGE,"E1.right")])]})});
            var Q566;
            Q566=makeQuery(id+"F3.boolean.opBoolean","COPY",EDGE,{"derivedFrom":makeQuery(id+"F3.opExtrude","SWEPT_EDGE",EDGE,{"disambiguationData":[OSD([sQuery(id+"F2.wireOp",EDGE,"E2.0.1.0"),sQuery(id+"F2.wireOp",EDGE,"E2.0.1.2")])]})});
            var Q567;
            Q567=makeQuery(id+"F3.boolean.opBoolean","COPY",EDGE,{"derivedFrom":makeQuery(id+"F3.opExtrude","SWEPT_EDGE",EDGE,{"disambiguationData":[OSD([sQuery(id+"F2.wireOp",EDGE,"E2.0.1.1"),sQuery(id+"F2.wireOp",EDGE,"E2.0.1.2")])]})});
            var Q568;
            Q568=makeQuery(id+"F3.boolean.opBoolean","COPY",EDGE,{"derivedFrom":makeQuery(id+"F3.opExtrude","SWEPT_EDGE",EDGE,{"disambiguationData":[OSD([sQuery(id+"F2.wireOp",EDGE,"E2.0.1.1"),sQuery(id+"F2.wireOp",EDGE,"E2.0.1.3")])]})});
            var Q569;
            Q569=makeQuery(id+"F3.boolean.opBoolean","COPY",EDGE,{"derivedFrom":makeQuery(id+"F3.opExtrude","SWEPT_EDGE",EDGE,{"disambiguationData":[OSD([sQuery(id+"F2.wireOp",EDGE,"E2.1.0.0"),sQuery(id+"F2.wireOp",EDGE,"E2.1.0.2")])]})});
            var Q570;
            Q570=makeQuery(id+"F3.boolean.opBoolean","COPY",EDGE,{"derivedFrom":makeQuery(id+"F3.opExtrude","SWEPT_EDGE",EDGE,{"disambiguationData":[OSD([sQuery(id+"F2.wireOp",EDGE,"E2.5.0.0"),sQuery(id+"F2.wireOp",EDGE,"E2.5.0.2")])]})});
            var Q571;
            Q571=makeQuery(id+"F3.boolean.opBoolean","COPY",EDGE,{"derivedFrom":makeQuery(id+"F3.opExtrude","SWEPT_EDGE",EDGE,{"disambiguationData":[OSD([sQuery(id+"F2.wireOp",EDGE,"E2.4.1.0"),sQuery(id+"F2.wireOp",EDGE,"E2.4.1.2")])]})});
            var Q572;
            Q572=makeQuery(id+"F3.boolean.opBoolean","COPY",EDGE,{"derivedFrom":makeQuery(id+"F3.opExtrude","SWEPT_EDGE",EDGE,{"disambiguationData":[OSD([sQuery(id+"F2.wireOp",EDGE,"E2.3.2.0"),sQuery(id+"F2.wireOp",EDGE,"E2.3.2.2")])]})});
            var Q573;
            Q573=makeQuery(id+"F3.boolean.opBoolean","COPY",EDGE,{"derivedFrom":makeQuery(id+"F3.opExtrude","CAP_EDGE",EDGE,{"disambiguationData":[OSD([sQuery(id+"F2.wireOp",EDGE,"E2.2.0.0")])],"isStart":true})});
            var Q574;
            Q574=makeQuery(id+"F3.boolean.opBoolean","COPY",EDGE,{"derivedFrom":makeQuery(id+"F3.opExtrude","CAP_EDGE",EDGE,{"disambiguationData":[OSD([sQuery(id+"F2.wireOp",EDGE,"E2.0.2.0")])],"isStart":true})});
            var Q575;
            Q575=makeQuery(id+"F3.boolean.opBoolean","COPY",EDGE,{"derivedFrom":makeQuery(id+"F3.opExtrude","CAP_EDGE",EDGE,{"disambiguationData":[OSD([sQuery(id+"F2.wireOp",EDGE,"E2.5.1.0")])],"isStart":true})});
            var Q576;
            Q576=makeQuery(id+"F3.boolean.opBoolean","COPY",EDGE,{"derivedFrom":makeQuery(id+"F3.opExtrude","CAP_EDGE",EDGE,{"disambiguationData":[OSD([sQuery(id+"F2.wireOp",EDGE,"E2.4.2.0")])],"isStart":true})});
            var Q577;
            Q577=makeQuery(id+"F3.boolean.opBoolean","INTERSECT",EDGE,{"derivedFrom":[makeQuery(id+"F1.opExtrude","CAP_FACE",FACE,{"disambiguationData":[OSD([sQuery(id+"F0.wireOp",EDGE,"E0.rect.bottom"),sQuery(id+"F0.wireOp",EDGE,"E0.rect.top"),sQuery(id+"F0.wireOp",EDGE,"E0.rect.left"),sQuery(id+"F0.wireOp",EDGE,"E0.rect.right")])],"isStart":true}),makeQuery(id+"F3.opExtrude","SWEPT_FACE",FACE,{"disambiguationData":[OSD([sQuery(id+"F2.wireOp",EDGE,"E2.5.1.2")])]})]});
            fillet(context, id + "F4", {"entities" : qUnion([Q0, Q1, Q2, Q3, Q4, Q5, Q6, Q7, Q8, Q9, Q10, Q11, Q12, Q13, Q14, Q15, Q16, Q17, Q18, Q19, Q20, Q21, Q22, Q23, Q24, Q25, Q26, Q27, Q28, Q29, Q30, Q31, Q32, Q33, Q34, Q35, Q36, Q37, Q38, Q39, Q40, Q41, Q42, Q43, Q44, Q45, Q46, Q47, Q48, Q49, Q50, Q51, Q52, Q53, Q54, Q55, Q56, Q57, Q58, Q59, Q60, Q61, Q62, Q63, Q64, Q65, Q66, Q67, Q68, Q69, Q70, Q71, Q72, Q73, Q74, Q75, Q76, Q77, Q78, Q79, Q80, Q81, Q82, Q83, Q84, Q85, Q86, Q87, Q88, Q89, Q90, Q91, Q92, Q93, Q94, Q95, Q96, Q97, Q98, Q99, Q100, Q101, Q102, Q103, Q104, Q105, Q106, Q107, Q108, Q109, Q110, Q111, Q112, Q113, Q114, Q115, Q116, Q117, Q118, Q119, Q120, Q121, Q122, Q123, Q124, Q125, Q126, Q127, Q128, Q129, Q130, Q131, Q132, Q133, Q134, Q135, Q136, Q137, Q138, Q139, Q140, Q141, Q142, Q143, Q144, Q145, Q146, Q147, Q148, Q149, Q150, Q151, Q152, Q153, Q154, Q155, Q156, Q157, Q158, Q159, Q160, Q161, Q162, Q163, Q164, Q165, Q166, Q167, Q168, Q169, Q170, Q171, Q172, Q173, Q174, Q175, Q176, Q177, Q178, Q179, Q180, Q181, Q182, Q183, Q184, Q185, Q186, Q187, Q188, Q189, Q190, Q191, Q192, Q193, Q194, Q195, Q196, Q197, Q198, Q199, Q200, Q201, Q202, Q203, Q204, Q205, Q206, Q207, Q208, Q209, Q210, Q211, Q212, Q213, Q214, Q215, Q216, Q217, Q218, Q219, Q220, Q221, Q222, Q223, Q224, Q225, Q226, Q227, Q228, Q229, Q230, Q231, Q232, Q233, Q234, Q235, Q236, Q237, Q238, Q239, Q240, Q241, Q242, Q243, Q244, Q245, Q246, Q247, Q248, Q249, Q250, Q251, Q252, Q253, Q254, Q255, Q256, Q257, Q258, Q259, Q260, Q261, Q262, Q263, Q264, Q265, Q266, Q267, Q268, Q269, Q270, Q271, Q272, Q273, Q274, Q275, Q276, Q277, Q278, Q279, Q280, Q281, Q282, Q283, Q284, Q285, Q286, Q287, Q288, Q289, Q290, Q291, Q292, Q293, Q294, Q295, Q296, Q297, Q298, Q299, Q300, Q301, Q302, Q303, Q304, Q305, Q306, Q307, Q308, Q309, Q310, Q311, Q312, Q313, Q314, Q315, Q316, Q317, Q318, Q319, Q320, Q321, Q322, Q323, Q324, Q325, Q326, Q327, Q328, Q329, Q330, Q331, Q332, Q333, Q334, Q335, Q336, Q337, Q338, Q339, Q340, Q341, Q342, Q343, Q344, Q345, Q346, Q347, Q348, Q349, Q350, Q351, Q352, Q353, Q354, Q355, Q356, Q357, Q358, Q359, Q360, Q361, Q362, Q363, Q364, Q365, Q366, Q367, Q368, Q369, Q370, Q371, Q372, Q373, Q374, Q375, Q376, Q377, Q378, Q379, Q380, Q381, Q382, Q383, Q384, Q385, Q386, Q387, Q388, Q389, Q390, Q391, Q392, Q393, Q394, Q395, Q396, Q397, Q398, Q399, Q400, Q401, Q402, Q403, Q404, Q405, Q406, Q407, Q408, Q409, Q410, Q411, Q412, Q413, Q414, Q415, Q416, Q417, Q418, Q419, Q420, Q421, Q422, Q423, Q424, Q425, Q426, Q427, Q428, Q429, Q430, Q431, Q432, Q433, Q434, Q435, Q436, Q437, Q438, Q439, Q440, Q441, Q442, Q443, Q444, Q445, Q446, Q447, Q448, Q449, Q450, Q451, Q452, Q453, Q454, Q455, Q456, Q457, Q458, Q459, Q460, Q461, Q462, Q463, Q464, Q465, Q466, Q467, Q468, Q469, Q470, Q471, Q472, Q473, Q474, Q475, Q476, Q477, Q478, Q479, Q480, Q481, Q482, Q483, Q484, Q485, Q486, Q487, Q488, Q489, Q490, Q491, Q492, Q493, Q494, Q495, Q496, Q497, Q498, Q499, Q500, Q501, Q502, Q503, Q504, Q505, Q506, Q507, Q508, Q509, Q510, Q511, Q512, Q513, Q514, Q515, Q516, Q517, Q518, Q519, Q520, Q521, Q522, Q523, Q524, Q525, Q526, Q527, Q528, Q529, Q530, Q531, Q532, Q533, Q534, Q535, Q536, Q537, Q538, Q539, Q540, Q541, Q542, Q543, Q544, Q545, Q546, Q547, Q548, Q549, Q550, Q551, Q552, Q553, Q554, Q555, Q556, Q557, Q558, Q559, Q560, Q561, Q562, Q563, Q564, Q565, Q566, Q567, Q568, Q569, Q570, Q571, Q572, Q573, Q574, Q575, Q576, Q577]), "radius" : 1.27 * mm, "tangentPropagation" : true, "allowEdgeOverflow" : false});
        }
    });
